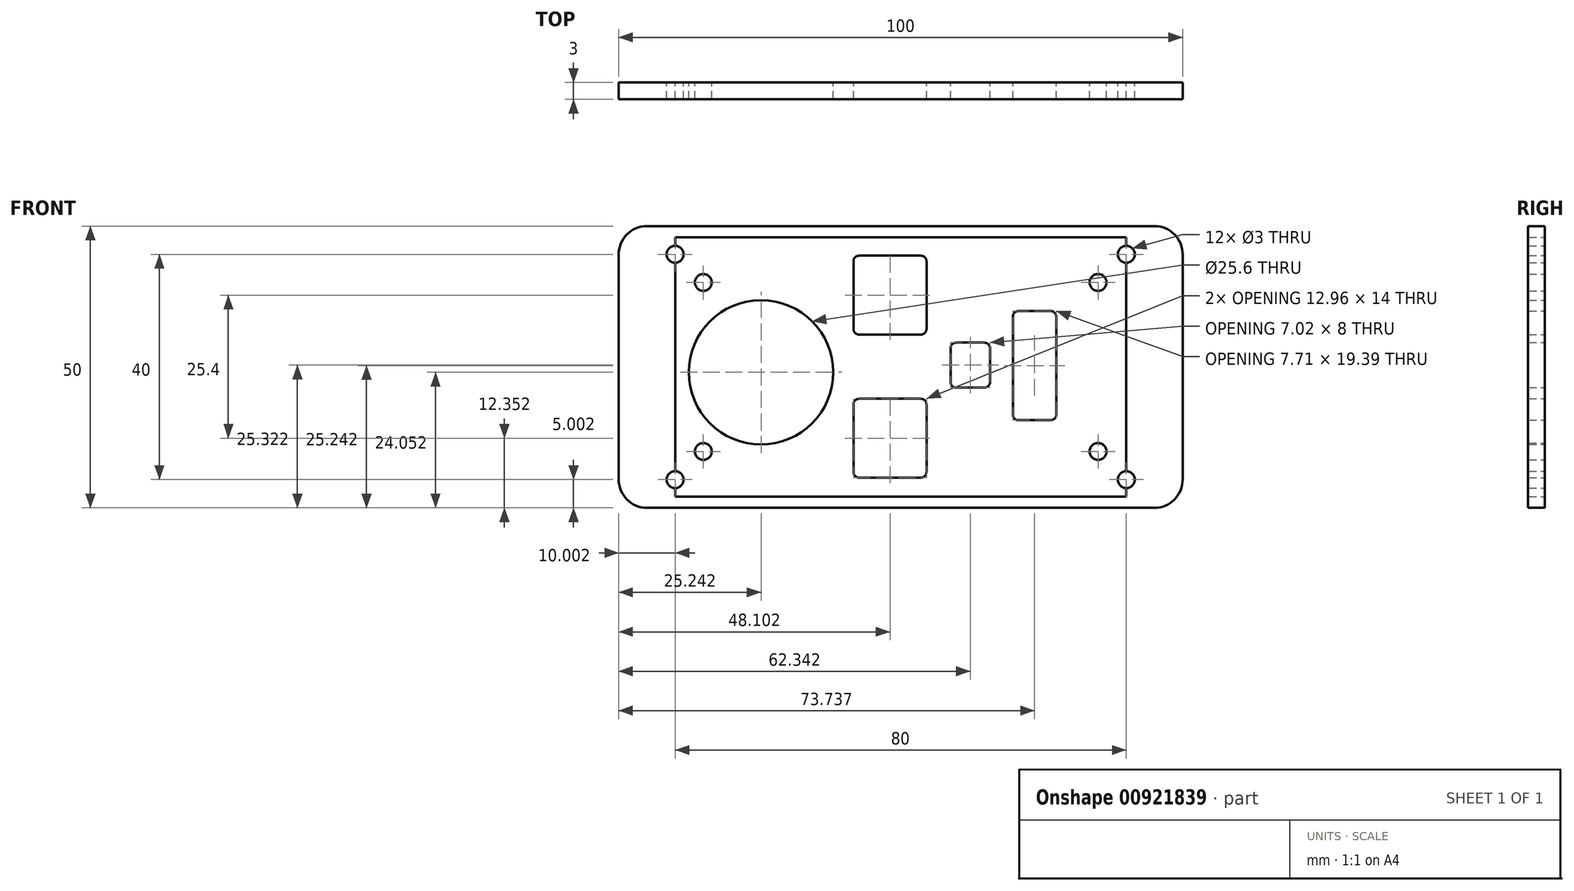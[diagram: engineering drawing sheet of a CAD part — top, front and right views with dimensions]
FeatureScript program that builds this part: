
annotation { "Feature Type Name" : "Feature", "Feature Type Description" : "" }
export const myFeature = defineFeature(function(context is Context, id is Id, definition is map)
    precondition{}
    {
        {
            var Q0;
            Q0=qCreatedBy(makeId("Front.planeOp"),FACE);
            var sketch = newSketch(context, id + "F0", { "sketchPlane" : qUnion([Q0])});
            skLineSegment(sketch, "E0", {"start": v(-79.7, -49.9) * mm, "end": v(-79.7, -9.9) * mm});
            skArc(sketch, "E1", {"start": v(-79.7, -9.9) * mm, "mid": v(-79.9, -9.7) * mm, "end": v(-80.1, -9.9) * mm});
            skLineSegment(sketch, "E2", {"start": v(-80.1, -9.9) * mm, "end": v(-80.1, -49.9) * mm});
            skArc(sketch, "E3", {"start": v(-80.1, -49.9) * mm, "mid": v(-79.9, -50.1) * mm, "end": v(-79.7, -49.9) * mm});
            skLineSegment(sketch, "E4", {"start": v(-79.9, -10.1) * mm, "end": v(0.1, -10.1) * mm});
            skArc(sketch, "E5", {"start": v(0.1, -10.1) * mm, "mid": v(0.3, -9.9) * mm, "end": v(0.1, -9.7) * mm});
            skLineSegment(sketch, "E6", {"start": v(0.1, -9.7) * mm, "end": v(-79.9, -9.7) * mm});
            skArc(sketch, "E7", {"start": v(-79.9, -9.7) * mm, "mid": v(-80.1, -9.9) * mm, "end": v(-79.9, -10.1) * mm});
            skLineSegment(sketch, "E8", {"start": v(-0.1, -9.9) * mm, "end": v(-0.1, -49.9) * mm});
            skArc(sketch, "E9", {"start": v(-0.1, -49.9) * mm, "mid": v(0.1, -50.1) * mm, "end": v(0.3, -49.9) * mm});
            skLineSegment(sketch, "E10", {"start": v(0.3, -49.9) * mm, "end": v(0.3, -9.9) * mm});
            skArc(sketch, "E11", {"start": v(0.3, -9.9) * mm, "mid": v(0.1, -9.7) * mm, "end": v(-0.1, -9.9) * mm});
            skLineSegment(sketch, "E12", {"start": v(0.1, -49.7) * mm, "end": v(-79.9, -49.7) * mm});
            skArc(sketch, "E13", {"start": v(-79.9, -49.7) * mm, "mid": v(-80.1, -49.9) * mm, "end": v(-79.9, -50.1) * mm});
            skLineSegment(sketch, "E14", {"start": v(-79.9, -50.1) * mm, "end": v(0.1, -50.1) * mm});
            skArc(sketch, "E15", {"start": v(0.1, -50.1) * mm, "mid": v(0.3, -49.9) * mm, "end": v(0.1, -49.7) * mm});
            skLineSegment(sketch, "E16", {"start": v(-11.34, -30.22) * mm, "end": v(-11.46, -30.1) * mm});
            skArc(sketch, "E17", {"start": v(-11.46, -30.1) * mm, "mid": v(-11.52, -30.1) * mm, "end": v(-11.52, -30.15) * mm});
            skLineSegment(sketch, "E18", {"start": v(-11.52, -30.15) * mm, "end": v(-11.4, -30.27) * mm});
            skArc(sketch, "E19", {"start": v(-11.4, -30.27) * mm, "mid": v(-11.34, -30.27) * mm, "end": v(-11.34, -30.22) * mm});
            skLineSegment(sketch, "E20", {"start": v(-11.5, -30.09) * mm, "end": v(-11.74, -30.09) * mm});
            skArc(sketch, "E21", {"start": v(-11.74, -30.09) * mm, "mid": v(-11.78, -30.12) * mm, "end": v(-11.74, -30.16) * mm});
            skLineSegment(sketch, "E22", {"start": v(-11.74, -30.16) * mm, "end": v(-11.5, -30.16) * mm});
            skArc(sketch, "E23", {"start": v(-11.5, -30.16) * mm, "mid": v(-11.45, -30.12) * mm, "end": v(-11.5, -30.09) * mm});
            skLineSegment(sketch, "E24", {"start": v(-11.76, -30.1) * mm, "end": v(-11.89, -30.22) * mm});
            skArc(sketch, "E25", {"start": v(-11.89, -30.22) * mm, "mid": v(-11.89, -30.27) * mm, "end": v(-11.83, -30.27) * mm});
            skLineSegment(sketch, "E26", {"start": v(-11.83, -30.27) * mm, "end": v(-11.71, -30.15) * mm});
            skArc(sketch, "E27", {"start": v(-11.71, -30.15) * mm, "mid": v(-11.71, -30.1) * mm, "end": v(-11.76, -30.1) * mm});
            skLineSegment(sketch, "E28", {"start": v(-11.9, -30.25) * mm, "end": v(-11.9, -30.74) * mm});
            skArc(sketch, "E29", {"start": v(-11.9, -30.74) * mm, "mid": v(-11.86, -30.78) * mm, "end": v(-11.82, -30.74) * mm});
            skLineSegment(sketch, "E30", {"start": v(-11.82, -30.74) * mm, "end": v(-11.82, -30.25) * mm});
            skArc(sketch, "E31", {"start": v(-11.82, -30.25) * mm, "mid": v(-11.86, -30.2) * mm, "end": v(-11.9, -30.25) * mm});
            skLineSegment(sketch, "E32", {"start": v(-11.89, -30.76) * mm, "end": v(-11.76, -30.89) * mm});
            skArc(sketch, "E33", {"start": v(-11.76, -30.89) * mm, "mid": v(-11.71, -30.89) * mm, "end": v(-11.71, -30.83) * mm});
            skLineSegment(sketch, "E34", {"start": v(-11.71, -30.83) * mm, "end": v(-11.83, -30.71) * mm});
            skArc(sketch, "E35", {"start": v(-11.83, -30.71) * mm, "mid": v(-11.89, -30.71) * mm, "end": v(-11.89, -30.76) * mm});
            skLineSegment(sketch, "E36", {"start": v(-11.74, -30.9) * mm, "end": v(-11.5, -30.9) * mm});
            skArc(sketch, "E37", {"start": v(-11.5, -30.9) * mm, "mid": v(-11.45, -30.86) * mm, "end": v(-11.5, -30.82) * mm});
            skLineSegment(sketch, "E38", {"start": v(-11.5, -30.82) * mm, "end": v(-11.74, -30.82) * mm});
            skArc(sketch, "E39", {"start": v(-11.74, -30.82) * mm, "mid": v(-11.78, -30.86) * mm, "end": v(-11.74, -30.9) * mm});
            skLineSegment(sketch, "E40", {"start": v(-11.46, -30.89) * mm, "end": v(-11.34, -30.76) * mm});
            skArc(sketch, "E41", {"start": v(-11.34, -30.76) * mm, "mid": v(-11.34, -30.71) * mm, "end": v(-11.4, -30.71) * mm});
            skLineSegment(sketch, "E42", {"start": v(-11.4, -30.71) * mm, "end": v(-11.52, -30.83) * mm});
            skArc(sketch, "E43", {"start": v(-11.52, -30.83) * mm, "mid": v(-11.52, -30.89) * mm, "end": v(-11.46, -30.89) * mm});
            skLineSegment(sketch, "E44", {"start": v(-11.33, -30.74) * mm, "end": v(-11.33, -30.5) * mm});
            skArc(sketch, "E45", {"start": v(-11.33, -30.5) * mm, "mid": v(-11.37, -30.45) * mm, "end": v(-11.4, -30.5) * mm});
            skLineSegment(sketch, "E46", {"start": v(-11.4, -30.5) * mm, "end": v(-11.4, -30.74) * mm});
            skArc(sketch, "E47", {"start": v(-11.4, -30.74) * mm, "mid": v(-11.37, -30.78) * mm, "end": v(-11.33, -30.74) * mm});
            skLineSegment(sketch, "E48", {"start": v(-11.37, -30.45) * mm, "end": v(-11.61, -30.45) * mm});
            skArc(sketch, "E49", {"start": v(-11.61, -30.45) * mm, "mid": v(-11.65, -30.5) * mm, "end": v(-11.61, -30.53) * mm});
            skLineSegment(sketch, "E50", {"start": v(-11.61, -30.53) * mm, "end": v(-11.37, -30.53) * mm});
            skArc(sketch, "E51", {"start": v(-11.37, -30.53) * mm, "mid": v(-11.33, -30.5) * mm, "end": v(-11.37, -30.45) * mm});
            skLineSegment(sketch, "E52", {"start": v(-11.07, -30.86) * mm, "end": v(-11.07, -30.12) * mm});
            skArc(sketch, "E53", {"start": v(-11.07, -30.12) * mm, "mid": v(-11.11, -30.09) * mm, "end": v(-11.15, -30.12) * mm});
            skLineSegment(sketch, "E54", {"start": v(-11.15, -30.12) * mm, "end": v(-11.15, -30.86) * mm});
            skArc(sketch, "E55", {"start": v(-11.15, -30.86) * mm, "mid": v(-11.11, -30.9) * mm, "end": v(-11.07, -30.86) * mm});
            skLineSegment(sketch, "E56", {"start": v(-11.14, -30.14) * mm, "end": v(-10.65, -30.88) * mm});
            skArc(sketch, "E57", {"start": v(-10.65, -30.88) * mm, "mid": v(-10.6, -30.9) * mm, "end": v(-10.59, -30.84) * mm});
            skLineSegment(sketch, "E58", {"start": v(-10.59, -30.84) * mm, "end": v(-11.08, -30.1) * mm});
            skArc(sketch, "E59", {"start": v(-11.08, -30.1) * mm, "mid": v(-11.13, -30.1) * mm, "end": v(-11.14, -30.14) * mm});
            skLineSegment(sketch, "E60", {"start": v(-10.58, -30.86) * mm, "end": v(-10.58, -30.12) * mm});
            skArc(sketch, "E61", {"start": v(-10.58, -30.12) * mm, "mid": v(-10.62, -30.09) * mm, "end": v(-10.66, -30.12) * mm});
            skLineSegment(sketch, "E62", {"start": v(-10.66, -30.12) * mm, "end": v(-10.66, -30.86) * mm});
            skArc(sketch, "E63", {"start": v(-10.66, -30.86) * mm, "mid": v(-10.62, -30.9) * mm, "end": v(-10.58, -30.86) * mm});
            skLineSegment(sketch, "E64", {"start": v(-10.4, -30.12) * mm, "end": v(-10.4, -30.86) * mm});
            skArc(sketch, "E65", {"start": v(-10.4, -30.86) * mm, "mid": v(-10.36, -30.9) * mm, "end": v(-10.33, -30.86) * mm});
            skLineSegment(sketch, "E66", {"start": v(-10.33, -30.86) * mm, "end": v(-10.33, -30.12) * mm});
            skArc(sketch, "E67", {"start": v(-10.33, -30.12) * mm, "mid": v(-10.36, -30.09) * mm, "end": v(-10.4, -30.12) * mm});
            skLineSegment(sketch, "E68", {"start": v(-10.36, -30.9) * mm, "end": v(-10, -30.9) * mm});
            skArc(sketch, "E69", {"start": v(-10, -30.9) * mm, "mid": v(-9.96, -30.86) * mm, "end": v(-10, -30.82) * mm});
            skLineSegment(sketch, "E70", {"start": v(-10, -30.82) * mm, "end": v(-10.36, -30.82) * mm});
            skArc(sketch, "E71", {"start": v(-10.36, -30.82) * mm, "mid": v(-10.4, -30.86) * mm, "end": v(-10.36, -30.9) * mm});
            skLineSegment(sketch, "E72", {"start": v(-9.97, -30.89) * mm, "end": v(-9.84, -30.76) * mm});
            skArc(sketch, "E73", {"start": v(-9.85, -30.76) * mm, "mid": v(-9.85, -30.71) * mm, "end": v(-9.9, -30.71) * mm});
            skLineSegment(sketch, "E74", {"start": v(-9.9, -30.71) * mm, "end": v(-10.02, -30.83) * mm});
            skArc(sketch, "E75", {"start": v(-10.02, -30.83) * mm, "mid": v(-10.02, -30.89) * mm, "end": v(-9.97, -30.89) * mm});
            skLineSegment(sketch, "E76", {"start": v(-9.83, -30.74) * mm, "end": v(-9.83, -30.25) * mm});
            skArc(sketch, "E77", {"start": v(-9.83, -30.25) * mm, "mid": v(-9.87, -30.2) * mm, "end": v(-9.91, -30.25) * mm});
            skLineSegment(sketch, "E78", {"start": v(-9.91, -30.25) * mm, "end": v(-9.91, -30.74) * mm});
            skArc(sketch, "E79", {"start": v(-9.91, -30.74) * mm, "mid": v(-9.87, -30.78) * mm, "end": v(-9.83, -30.74) * mm});
            skLineSegment(sketch, "E80", {"start": v(-9.84, -30.22) * mm, "end": v(-9.97, -30.1) * mm});
            skArc(sketch, "E81", {"start": v(-9.97, -30.1) * mm, "mid": v(-10.02, -30.1) * mm, "end": v(-10.02, -30.15) * mm});
            skLineSegment(sketch, "E82", {"start": v(-10.02, -30.15) * mm, "end": v(-9.9, -30.27) * mm});
            skArc(sketch, "E83", {"start": v(-9.9, -30.27) * mm, "mid": v(-9.85, -30.27) * mm, "end": v(-9.85, -30.22) * mm});
            skLineSegment(sketch, "E84", {"start": v(-10, -30.09) * mm, "end": v(-10.36, -30.09) * mm});
            skArc(sketch, "E85", {"start": v(-10.36, -30.09) * mm, "mid": v(-10.4, -30.12) * mm, "end": v(-10.36, -30.16) * mm});
            skLineSegment(sketch, "E86", {"start": v(-10.36, -30.16) * mm, "end": v(-10, -30.16) * mm});
            skArc(sketch, "E87", {"start": v(-10, -30.16) * mm, "mid": v(-9.96, -30.12) * mm, "end": v(-10, -30.09) * mm});
            skLineSegment(sketch, "E88", {"start": v(-11.9, -22.12) * mm, "end": v(-11.9, -22.61) * mm});
            skArc(sketch, "E89", {"start": v(-11.9, -22.61) * mm, "mid": v(-11.86, -22.65) * mm, "end": v(-11.82, -22.61) * mm});
            skLineSegment(sketch, "E90", {"start": v(-11.82, -22.61) * mm, "end": v(-11.82, -22.12) * mm});
            skArc(sketch, "E91", {"start": v(-11.82, -22.12) * mm, "mid": v(-11.86, -22.09) * mm, "end": v(-11.9, -22.12) * mm});
            skLineSegment(sketch, "E92", {"start": v(-11.89, -22.64) * mm, "end": v(-11.64, -22.89) * mm});
            skArc(sketch, "E93", {"start": v(-11.64, -22.89) * mm, "mid": v(-11.59, -22.89) * mm, "end": v(-11.59, -22.83) * mm});
            skLineSegment(sketch, "E94", {"start": v(-11.59, -22.83) * mm, "end": v(-11.83, -22.59) * mm});
            skArc(sketch, "E95", {"start": v(-11.83, -22.59) * mm, "mid": v(-11.89, -22.59) * mm, "end": v(-11.89, -22.64) * mm});
            skLineSegment(sketch, "E96", {"start": v(-11.59, -22.89) * mm, "end": v(-11.34, -22.64) * mm});
            skArc(sketch, "E97", {"start": v(-11.34, -22.64) * mm, "mid": v(-11.34, -22.59) * mm, "end": v(-11.4, -22.59) * mm});
            skLineSegment(sketch, "E98", {"start": v(-11.4, -22.59) * mm, "end": v(-11.64, -22.83) * mm});
            skArc(sketch, "E99", {"start": v(-11.64, -22.83) * mm, "mid": v(-11.64, -22.89) * mm, "end": v(-11.59, -22.89) * mm});
            skLineSegment(sketch, "E100", {"start": v(-11.33, -22.61) * mm, "end": v(-11.33, -22.12) * mm});
            skArc(sketch, "E101", {"start": v(-11.33, -22.12) * mm, "mid": v(-11.37, -22.09) * mm, "end": v(-11.4, -22.12) * mm});
            skLineSegment(sketch, "E102", {"start": v(-11.4, -22.12) * mm, "end": v(-11.4, -22.61) * mm});
            skArc(sketch, "E103", {"start": v(-11.4, -22.61) * mm, "mid": v(-11.37, -22.65) * mm, "end": v(-11.33, -22.61) * mm});
            skLineSegment(sketch, "E104", {"start": v(-10.6, -22.22) * mm, "end": v(-10.72, -22.1) * mm});
            skArc(sketch, "E105", {"start": v(-10.72, -22.1) * mm, "mid": v(-10.77, -22.1) * mm, "end": v(-10.77, -22.15) * mm});
            skLineSegment(sketch, "E106", {"start": v(-10.77, -22.15) * mm, "end": v(-10.65, -22.27) * mm});
            skArc(sketch, "E107", {"start": v(-10.65, -22.27) * mm, "mid": v(-10.6, -22.27) * mm, "end": v(-10.6, -22.22) * mm});
            skLineSegment(sketch, "E108", {"start": v(-10.74, -22.09) * mm, "end": v(-10.99, -22.09) * mm});
            skArc(sketch, "E109", {"start": v(-10.99, -22.09) * mm, "mid": v(-11.03, -22.12) * mm, "end": v(-10.99, -22.16) * mm});
            skLineSegment(sketch, "E110", {"start": v(-10.99, -22.16) * mm, "end": v(-10.74, -22.16) * mm});
            skArc(sketch, "E111", {"start": v(-10.74, -22.16) * mm, "mid": v(-10.7, -22.12) * mm, "end": v(-10.74, -22.09) * mm});
            skLineSegment(sketch, "E112", {"start": v(-11.02, -22.1) * mm, "end": v(-11.14, -22.22) * mm});
            skArc(sketch, "E113", {"start": v(-11.14, -22.22) * mm, "mid": v(-11.14, -22.27) * mm, "end": v(-11.08, -22.27) * mm});
            skLineSegment(sketch, "E114", {"start": v(-11.08, -22.27) * mm, "end": v(-10.96, -22.15) * mm});
            skArc(sketch, "E115", {"start": v(-10.96, -22.15) * mm, "mid": v(-10.96, -22.1) * mm, "end": v(-11.02, -22.1) * mm});
            skLineSegment(sketch, "E116", {"start": v(-11.15, -22.25) * mm, "end": v(-11.15, -22.74) * mm});
            skArc(sketch, "E117", {"start": v(-11.15, -22.74) * mm, "mid": v(-11.11, -22.78) * mm, "end": v(-11.07, -22.74) * mm});
            skLineSegment(sketch, "E118", {"start": v(-11.07, -22.74) * mm, "end": v(-11.07, -22.25) * mm});
            skArc(sketch, "E119", {"start": v(-11.07, -22.25) * mm, "mid": v(-11.11, -22.2) * mm, "end": v(-11.15, -22.25) * mm});
            skLineSegment(sketch, "E120", {"start": v(-11.14, -22.76) * mm, "end": v(-11.02, -22.89) * mm});
            skArc(sketch, "E121", {"start": v(-11.02, -22.89) * mm, "mid": v(-10.96, -22.89) * mm, "end": v(-10.96, -22.83) * mm});
            skLineSegment(sketch, "E122", {"start": v(-10.96, -22.83) * mm, "end": v(-11.08, -22.71) * mm});
            skArc(sketch, "E123", {"start": v(-11.08, -22.71) * mm, "mid": v(-11.14, -22.71) * mm, "end": v(-11.14, -22.76) * mm});
            skLineSegment(sketch, "E124", {"start": v(-10.99, -22.9) * mm, "end": v(-10.74, -22.9) * mm});
            skArc(sketch, "E125", {"start": v(-10.74, -22.9) * mm, "mid": v(-10.7, -22.86) * mm, "end": v(-10.74, -22.82) * mm});
            skLineSegment(sketch, "E126", {"start": v(-10.74, -22.82) * mm, "end": v(-10.99, -22.82) * mm});
            skArc(sketch, "E127", {"start": v(-10.99, -22.82) * mm, "mid": v(-11.03, -22.86) * mm, "end": v(-10.99, -22.9) * mm});
            skLineSegment(sketch, "E128", {"start": v(-10.72, -22.89) * mm, "end": v(-10.6, -22.76) * mm});
            skArc(sketch, "E129", {"start": v(-10.6, -22.76) * mm, "mid": v(-10.6, -22.71) * mm, "end": v(-10.65, -22.71) * mm});
            skLineSegment(sketch, "E130", {"start": v(-10.65, -22.71) * mm, "end": v(-10.77, -22.83) * mm});
            skArc(sketch, "E131", {"start": v(-10.77, -22.83) * mm, "mid": v(-10.77, -22.89) * mm, "end": v(-10.72, -22.89) * mm});
            skLineSegment(sketch, "E132", {"start": v(-9.84, -22.22) * mm, "end": v(-9.97, -22.1) * mm});
            skArc(sketch, "E133", {"start": v(-9.97, -22.1) * mm, "mid": v(-10.02, -22.1) * mm, "end": v(-10.02, -22.15) * mm});
            skLineSegment(sketch, "E134", {"start": v(-10.02, -22.15) * mm, "end": v(-9.9, -22.27) * mm});
            skArc(sketch, "E135", {"start": v(-9.9, -22.27) * mm, "mid": v(-9.85, -22.27) * mm, "end": v(-9.85, -22.22) * mm});
            skLineSegment(sketch, "E136", {"start": v(-10, -22.09) * mm, "end": v(-10.24, -22.09) * mm});
            skArc(sketch, "E137", {"start": v(-10.24, -22.09) * mm, "mid": v(-10.28, -22.12) * mm, "end": v(-10.24, -22.16) * mm});
            skLineSegment(sketch, "E138", {"start": v(-10.24, -22.16) * mm, "end": v(-10, -22.16) * mm});
            skArc(sketch, "E139", {"start": v(-10, -22.16) * mm, "mid": v(-9.96, -22.12) * mm, "end": v(-10, -22.09) * mm});
            skLineSegment(sketch, "E140", {"start": v(-10.27, -22.1) * mm, "end": v(-10.4, -22.22) * mm});
            skArc(sketch, "E141", {"start": v(-10.4, -22.22) * mm, "mid": v(-10.4, -22.27) * mm, "end": v(-10.34, -22.27) * mm});
            skLineSegment(sketch, "E142", {"start": v(-10.34, -22.27) * mm, "end": v(-10.21, -22.15) * mm});
            skArc(sketch, "E143", {"start": v(-10.21, -22.15) * mm, "mid": v(-10.21, -22.1) * mm, "end": v(-10.27, -22.1) * mm});
            skLineSegment(sketch, "E144", {"start": v(-10.4, -22.25) * mm, "end": v(-10.4, -22.74) * mm});
            skArc(sketch, "E145", {"start": v(-10.4, -22.74) * mm, "mid": v(-10.36, -22.78) * mm, "end": v(-10.33, -22.74) * mm});
            skLineSegment(sketch, "E146", {"start": v(-10.33, -22.74) * mm, "end": v(-10.33, -22.25) * mm});
            skArc(sketch, "E147", {"start": v(-10.33, -22.25) * mm, "mid": v(-10.36, -22.2) * mm, "end": v(-10.4, -22.25) * mm});
            skLineSegment(sketch, "E148", {"start": v(-10.4, -22.76) * mm, "end": v(-10.27, -22.89) * mm});
            skArc(sketch, "E149", {"start": v(-10.27, -22.89) * mm, "mid": v(-10.21, -22.89) * mm, "end": v(-10.21, -22.83) * mm});
            skLineSegment(sketch, "E150", {"start": v(-10.21, -22.83) * mm, "end": v(-10.34, -22.71) * mm});
            skArc(sketch, "E151", {"start": v(-10.34, -22.71) * mm, "mid": v(-10.4, -22.71) * mm, "end": v(-10.4, -22.76) * mm});
            skLineSegment(sketch, "E152", {"start": v(-10.24, -22.9) * mm, "end": v(-10, -22.9) * mm});
            skArc(sketch, "E153", {"start": v(-10, -22.9) * mm, "mid": v(-9.96, -22.86) * mm, "end": v(-10, -22.82) * mm});
            skLineSegment(sketch, "E154", {"start": v(-10, -22.82) * mm, "end": v(-10.24, -22.82) * mm});
            skArc(sketch, "E155", {"start": v(-10.24, -22.82) * mm, "mid": v(-10.28, -22.86) * mm, "end": v(-10.24, -22.9) * mm});
            skLineSegment(sketch, "E156", {"start": v(-9.97, -22.89) * mm, "end": v(-9.84, -22.76) * mm});
            skArc(sketch, "E157", {"start": v(-9.85, -22.76) * mm, "mid": v(-9.85, -22.71) * mm, "end": v(-9.9, -22.71) * mm});
            skLineSegment(sketch, "E158", {"start": v(-9.9, -22.71) * mm, "end": v(-10.02, -22.83) * mm});
            skArc(sketch, "E159", {"start": v(-10.02, -22.83) * mm, "mid": v(-10.02, -22.89) * mm, "end": v(-9.97, -22.89) * mm});
            skLineSegment(sketch, "E160", {"start": v(-11.9, -25.12) * mm, "end": v(-11.9, -25.61) * mm});
            skArc(sketch, "E161", {"start": v(-11.9, -25.61) * mm, "mid": v(-11.86, -25.65) * mm, "end": v(-11.82, -25.61) * mm});
            skLineSegment(sketch, "E162", {"start": v(-11.82, -25.61) * mm, "end": v(-11.82, -25.12) * mm});
            skArc(sketch, "E163", {"start": v(-11.82, -25.12) * mm, "mid": v(-11.86, -25.09) * mm, "end": v(-11.9, -25.12) * mm});
            skLineSegment(sketch, "E164", {"start": v(-11.89, -25.64) * mm, "end": v(-11.64, -25.89) * mm});
            skArc(sketch, "E165", {"start": v(-11.64, -25.89) * mm, "mid": v(-11.59, -25.89) * mm, "end": v(-11.59, -25.83) * mm});
            skLineSegment(sketch, "E166", {"start": v(-11.59, -25.83) * mm, "end": v(-11.83, -25.59) * mm});
            skArc(sketch, "E167", {"start": v(-11.83, -25.59) * mm, "mid": v(-11.89, -25.59) * mm, "end": v(-11.89, -25.64) * mm});
            skLineSegment(sketch, "E168", {"start": v(-11.59, -25.89) * mm, "end": v(-11.34, -25.64) * mm});
            skArc(sketch, "E169", {"start": v(-11.34, -25.64) * mm, "mid": v(-11.34, -25.59) * mm, "end": v(-11.4, -25.59) * mm});
            skLineSegment(sketch, "E170", {"start": v(-11.4, -25.59) * mm, "end": v(-11.64, -25.83) * mm});
            skArc(sketch, "E171", {"start": v(-11.64, -25.83) * mm, "mid": v(-11.64, -25.89) * mm, "end": v(-11.59, -25.89) * mm});
            skLineSegment(sketch, "E172", {"start": v(-11.33, -25.61) * mm, "end": v(-11.33, -25.12) * mm});
            skArc(sketch, "E173", {"start": v(-11.33, -25.12) * mm, "mid": v(-11.37, -25.09) * mm, "end": v(-11.4, -25.12) * mm});
            skLineSegment(sketch, "E174", {"start": v(-11.4, -25.12) * mm, "end": v(-11.4, -25.61) * mm});
            skArc(sketch, "E175", {"start": v(-11.4, -25.61) * mm, "mid": v(-11.37, -25.65) * mm, "end": v(-11.33, -25.61) * mm});
            skLineSegment(sketch, "E176", {"start": v(-10.62, -25.09) * mm, "end": v(-11.11, -25.09) * mm});
            skArc(sketch, "E177", {"start": v(-11.11, -25.09) * mm, "mid": v(-11.15, -25.12) * mm, "end": v(-11.11, -25.16) * mm});
            skLineSegment(sketch, "E178", {"start": v(-11.11, -25.16) * mm, "end": v(-10.62, -25.16) * mm});
            skArc(sketch, "E179", {"start": v(-10.62, -25.16) * mm, "mid": v(-10.58, -25.12) * mm, "end": v(-10.62, -25.09) * mm});
            skLineSegment(sketch, "E180", {"start": v(-11.15, -25.12) * mm, "end": v(-11.15, -25.86) * mm});
            skArc(sketch, "E181", {"start": v(-11.15, -25.86) * mm, "mid": v(-11.11, -25.9) * mm, "end": v(-11.07, -25.86) * mm});
            skLineSegment(sketch, "E182", {"start": v(-11.07, -25.86) * mm, "end": v(-11.07, -25.12) * mm});
            skArc(sketch, "E183", {"start": v(-11.07, -25.12) * mm, "mid": v(-11.11, -25.09) * mm, "end": v(-11.15, -25.12) * mm});
            skLineSegment(sketch, "E184", {"start": v(-11.11, -25.9) * mm, "end": v(-10.62, -25.9) * mm});
            skArc(sketch, "E185", {"start": v(-10.62, -25.9) * mm, "mid": v(-10.58, -25.86) * mm, "end": v(-10.62, -25.82) * mm});
            skLineSegment(sketch, "E186", {"start": v(-10.62, -25.82) * mm, "end": v(-11.11, -25.82) * mm});
            skArc(sketch, "E187", {"start": v(-11.11, -25.82) * mm, "mid": v(-11.15, -25.86) * mm, "end": v(-11.11, -25.9) * mm});
            skLineSegment(sketch, "E188", {"start": v(-11.11, -25.53) * mm, "end": v(-10.87, -25.53) * mm});
            skArc(sketch, "E189", {"start": v(-10.87, -25.53) * mm, "mid": v(-10.83, -25.5) * mm, "end": v(-10.87, -25.45) * mm});
            skLineSegment(sketch, "E190", {"start": v(-10.87, -25.45) * mm, "end": v(-11.11, -25.45) * mm});
            skArc(sketch, "E191", {"start": v(-11.11, -25.45) * mm, "mid": v(-11.15, -25.5) * mm, "end": v(-11.11, -25.53) * mm});
            skLineSegment(sketch, "E192", {"start": v(-10.33, -25.86) * mm, "end": v(-10.33, -25.12) * mm});
            skArc(sketch, "E193", {"start": v(-10.33, -25.12) * mm, "mid": v(-10.36, -25.09) * mm, "end": v(-10.4, -25.12) * mm});
            skLineSegment(sketch, "E194", {"start": v(-10.4, -25.12) * mm, "end": v(-10.4, -25.86) * mm});
            skArc(sketch, "E195", {"start": v(-10.4, -25.86) * mm, "mid": v(-10.36, -25.9) * mm, "end": v(-10.33, -25.86) * mm});
            skLineSegment(sketch, "E196", {"start": v(-10.36, -25.16) * mm, "end": v(-10, -25.16) * mm});
            skArc(sketch, "E197", {"start": v(-10, -25.16) * mm, "mid": v(-9.96, -25.12) * mm, "end": v(-10, -25.09) * mm});
            skLineSegment(sketch, "E198", {"start": v(-10, -25.09) * mm, "end": v(-10.36, -25.09) * mm});
            skArc(sketch, "E199", {"start": v(-10.36, -25.09) * mm, "mid": v(-10.4, -25.12) * mm, "end": v(-10.36, -25.16) * mm});
            skLineSegment(sketch, "E200", {"start": v(-10.02, -25.15) * mm, "end": v(-9.9, -25.27) * mm});
            skArc(sketch, "E201", {"start": v(-9.9, -25.27) * mm, "mid": v(-9.85, -25.27) * mm, "end": v(-9.85, -25.22) * mm});
            skLineSegment(sketch, "E202", {"start": v(-9.84, -25.22) * mm, "end": v(-9.97, -25.1) * mm});
            skArc(sketch, "E203", {"start": v(-9.97, -25.1) * mm, "mid": v(-10.02, -25.1) * mm, "end": v(-10.02, -25.15) * mm});
            skLineSegment(sketch, "E204", {"start": v(-9.91, -25.25) * mm, "end": v(-9.91, -25.5) * mm});
            skArc(sketch, "E205", {"start": v(-9.91, -25.5) * mm, "mid": v(-9.87, -25.53) * mm, "end": v(-9.83, -25.5) * mm});
            skLineSegment(sketch, "E206", {"start": v(-9.83, -25.5) * mm, "end": v(-9.83, -25.25) * mm});
            skArc(sketch, "E207", {"start": v(-9.83, -25.25) * mm, "mid": v(-9.87, -25.2) * mm, "end": v(-9.91, -25.25) * mm});
            skLineSegment(sketch, "E208", {"start": v(-9.9, -25.46) * mm, "end": v(-10.02, -25.59) * mm});
            skArc(sketch, "E209", {"start": v(-10.02, -25.59) * mm, "mid": v(-10.02, -25.64) * mm, "end": v(-9.97, -25.64) * mm});
            skLineSegment(sketch, "E210", {"start": v(-9.97, -25.64) * mm, "end": v(-9.84, -25.52) * mm});
            skArc(sketch, "E211", {"start": v(-9.85, -25.52) * mm, "mid": v(-9.85, -25.46) * mm, "end": v(-9.9, -25.46) * mm});
            skLineSegment(sketch, "E212", {"start": v(-10, -25.58) * mm, "end": v(-10.36, -25.58) * mm});
            skArc(sketch, "E213", {"start": v(-10.36, -25.58) * mm, "mid": v(-10.4, -25.61) * mm, "end": v(-10.36, -25.65) * mm});
            skLineSegment(sketch, "E214", {"start": v(-10.36, -25.65) * mm, "end": v(-10, -25.65) * mm});
            skArc(sketch, "E215", {"start": v(-10, -25.65) * mm, "mid": v(-9.96, -25.61) * mm, "end": v(-10, -25.58) * mm});
            skLineSegment(sketch, "E216", {"start": v(-10.14, -25.64) * mm, "end": v(-9.9, -25.89) * mm});
            skArc(sketch, "E217", {"start": v(-9.9, -25.89) * mm, "mid": v(-9.85, -25.89) * mm, "end": v(-9.84, -25.83) * mm});
            skLineSegment(sketch, "E218", {"start": v(-9.84, -25.83) * mm, "end": v(-10.1, -25.59) * mm});
            skArc(sketch, "E219", {"start": v(-10.1, -25.59) * mm, "mid": v(-10.14, -25.59) * mm, "end": v(-10.14, -25.64) * mm});
            skLineSegment(sketch, "E220", {"start": v(-11.82, -28.86) * mm, "end": v(-11.82, -28.12) * mm});
            skArc(sketch, "E221", {"start": v(-11.82, -28.12) * mm, "mid": v(-11.86, -28.09) * mm, "end": v(-11.9, -28.12) * mm});
            skLineSegment(sketch, "E222", {"start": v(-11.9, -28.12) * mm, "end": v(-11.9, -28.86) * mm});
            skArc(sketch, "E223", {"start": v(-11.9, -28.86) * mm, "mid": v(-11.86, -28.9) * mm, "end": v(-11.82, -28.86) * mm});
            skLineSegment(sketch, "E224", {"start": v(-11.86, -28.53) * mm, "end": v(-11.37, -28.53) * mm});
            skArc(sketch, "E225", {"start": v(-11.37, -28.53) * mm, "mid": v(-11.33, -28.5) * mm, "end": v(-11.37, -28.45) * mm});
            skLineSegment(sketch, "E226", {"start": v(-11.37, -28.45) * mm, "end": v(-11.86, -28.45) * mm});
            skArc(sketch, "E227", {"start": v(-11.86, -28.45) * mm, "mid": v(-11.9, -28.5) * mm, "end": v(-11.86, -28.53) * mm});
            skLineSegment(sketch, "E228", {"start": v(-11.4, -28.12) * mm, "end": v(-11.4, -28.86) * mm});
            skArc(sketch, "E229", {"start": v(-11.4, -28.86) * mm, "mid": v(-11.37, -28.9) * mm, "end": v(-11.33, -28.86) * mm});
            skLineSegment(sketch, "E230", {"start": v(-11.33, -28.86) * mm, "end": v(-11.33, -28.12) * mm});
            skArc(sketch, "E231", {"start": v(-11.33, -28.12) * mm, "mid": v(-11.37, -28.09) * mm, "end": v(-11.4, -28.12) * mm});
            skLineSegment(sketch, "E232", {"start": v(-10.74, -28.09) * mm, "end": v(-10.99, -28.09) * mm});
            skArc(sketch, "E233", {"start": v(-10.99, -28.09) * mm, "mid": v(-11.03, -28.12) * mm, "end": v(-10.99, -28.16) * mm});
            skLineSegment(sketch, "E234", {"start": v(-10.99, -28.16) * mm, "end": v(-10.74, -28.16) * mm});
            skArc(sketch, "E235", {"start": v(-10.74, -28.16) * mm, "mid": v(-10.7, -28.12) * mm, "end": v(-10.74, -28.09) * mm});
            skLineSegment(sketch, "E236", {"start": v(-11.02, -28.1) * mm, "end": v(-11.14, -28.22) * mm});
            skArc(sketch, "E237", {"start": v(-11.14, -28.22) * mm, "mid": v(-11.14, -28.27) * mm, "end": v(-11.08, -28.27) * mm});
            skLineSegment(sketch, "E238", {"start": v(-11.08, -28.27) * mm, "end": v(-10.96, -28.15) * mm});
            skArc(sketch, "E239", {"start": v(-10.96, -28.15) * mm, "mid": v(-10.96, -28.1) * mm, "end": v(-11.02, -28.1) * mm});
            skLineSegment(sketch, "E240", {"start": v(-11.15, -28.25) * mm, "end": v(-11.15, -28.74) * mm});
            skArc(sketch, "E241", {"start": v(-11.15, -28.74) * mm, "mid": v(-11.11, -28.78) * mm, "end": v(-11.07, -28.74) * mm});
            skLineSegment(sketch, "E242", {"start": v(-11.07, -28.74) * mm, "end": v(-11.07, -28.25) * mm});
            skArc(sketch, "E243", {"start": v(-11.07, -28.25) * mm, "mid": v(-11.11, -28.2) * mm, "end": v(-11.15, -28.25) * mm});
            skLineSegment(sketch, "E244", {"start": v(-11.14, -28.76) * mm, "end": v(-11.02, -28.89) * mm});
            skArc(sketch, "E245", {"start": v(-11.02, -28.89) * mm, "mid": v(-10.96, -28.89) * mm, "end": v(-10.96, -28.83) * mm});
            skLineSegment(sketch, "E246", {"start": v(-10.96, -28.83) * mm, "end": v(-11.08, -28.71) * mm});
            skArc(sketch, "E247", {"start": v(-11.08, -28.71) * mm, "mid": v(-11.14, -28.71) * mm, "end": v(-11.14, -28.76) * mm});
            skLineSegment(sketch, "E248", {"start": v(-10.99, -28.9) * mm, "end": v(-10.74, -28.9) * mm});
            skArc(sketch, "E249", {"start": v(-10.74, -28.9) * mm, "mid": v(-10.7, -28.86) * mm, "end": v(-10.74, -28.82) * mm});
            skLineSegment(sketch, "E250", {"start": v(-10.74, -28.82) * mm, "end": v(-10.99, -28.82) * mm});
            skArc(sketch, "E251", {"start": v(-10.99, -28.82) * mm, "mid": v(-11.03, -28.86) * mm, "end": v(-10.99, -28.9) * mm});
            skLineSegment(sketch, "E252", {"start": v(-10.72, -28.89) * mm, "end": v(-10.6, -28.76) * mm});
            skArc(sketch, "E253", {"start": v(-10.6, -28.76) * mm, "mid": v(-10.6, -28.71) * mm, "end": v(-10.65, -28.71) * mm});
            skLineSegment(sketch, "E254", {"start": v(-10.65, -28.71) * mm, "end": v(-10.77, -28.83) * mm});
            skArc(sketch, "E255", {"start": v(-10.77, -28.83) * mm, "mid": v(-10.77, -28.89) * mm, "end": v(-10.72, -28.89) * mm});
            skLineSegment(sketch, "E256", {"start": v(-10.58, -28.74) * mm, "end": v(-10.58, -28.25) * mm});
            skArc(sketch, "E257", {"start": v(-10.58, -28.25) * mm, "mid": v(-10.62, -28.2) * mm, "end": v(-10.66, -28.25) * mm});
            skLineSegment(sketch, "E258", {"start": v(-10.66, -28.25) * mm, "end": v(-10.66, -28.74) * mm});
            skArc(sketch, "E259", {"start": v(-10.66, -28.74) * mm, "mid": v(-10.62, -28.78) * mm, "end": v(-10.58, -28.74) * mm});
            skLineSegment(sketch, "E260", {"start": v(-10.6, -28.22) * mm, "end": v(-10.72, -28.1) * mm});
            skArc(sketch, "E261", {"start": v(-10.72, -28.1) * mm, "mid": v(-10.77, -28.1) * mm, "end": v(-10.77, -28.15) * mm});
            skLineSegment(sketch, "E262", {"start": v(-10.77, -28.15) * mm, "end": v(-10.65, -28.27) * mm});
            skArc(sketch, "E263", {"start": v(-10.65, -28.27) * mm, "mid": v(-10.6, -28.27) * mm, "end": v(-10.6, -28.22) * mm});
            skLineSegment(sketch, "E264", {"start": v(-10.33, -28.86) * mm, "end": v(-10.33, -28.12) * mm});
            skArc(sketch, "E265", {"start": v(-10.33, -28.12) * mm, "mid": v(-10.36, -28.09) * mm, "end": v(-10.4, -28.12) * mm});
            skLineSegment(sketch, "E266", {"start": v(-10.4, -28.12) * mm, "end": v(-10.4, -28.86) * mm});
            skArc(sketch, "E267", {"start": v(-10.4, -28.86) * mm, "mid": v(-10.36, -28.9) * mm, "end": v(-10.33, -28.86) * mm});
            skLineSegment(sketch, "E268", {"start": v(-10.36, -28.16) * mm, "end": v(-10, -28.16) * mm});
            skArc(sketch, "E269", {"start": v(-10, -28.16) * mm, "mid": v(-9.96, -28.12) * mm, "end": v(-10, -28.09) * mm});
            skLineSegment(sketch, "E270", {"start": v(-10, -28.09) * mm, "end": v(-10.36, -28.09) * mm});
            skArc(sketch, "E271", {"start": v(-10.36, -28.09) * mm, "mid": v(-10.4, -28.12) * mm, "end": v(-10.36, -28.16) * mm});
            skLineSegment(sketch, "E272", {"start": v(-10.02, -28.15) * mm, "end": v(-9.9, -28.27) * mm});
            skArc(sketch, "E273", {"start": v(-9.9, -28.27) * mm, "mid": v(-9.85, -28.27) * mm, "end": v(-9.85, -28.22) * mm});
            skLineSegment(sketch, "E274", {"start": v(-9.84, -28.22) * mm, "end": v(-9.97, -28.1) * mm});
            skArc(sketch, "E275", {"start": v(-9.97, -28.1) * mm, "mid": v(-10.02, -28.1) * mm, "end": v(-10.02, -28.15) * mm});
            skLineSegment(sketch, "E276", {"start": v(-9.91, -28.25) * mm, "end": v(-9.91, -28.5) * mm});
            skArc(sketch, "E277", {"start": v(-9.91, -28.5) * mm, "mid": v(-9.87, -28.53) * mm, "end": v(-9.83, -28.5) * mm});
            skLineSegment(sketch, "E278", {"start": v(-9.83, -28.5) * mm, "end": v(-9.83, -28.25) * mm});
            skArc(sketch, "E279", {"start": v(-9.83, -28.25) * mm, "mid": v(-9.87, -28.2) * mm, "end": v(-9.91, -28.25) * mm});
            skLineSegment(sketch, "E280", {"start": v(-9.9, -28.46) * mm, "end": v(-10.02, -28.59) * mm});
            skArc(sketch, "E281", {"start": v(-10.02, -28.59) * mm, "mid": v(-10.02, -28.64) * mm, "end": v(-9.97, -28.64) * mm});
            skLineSegment(sketch, "E282", {"start": v(-9.97, -28.64) * mm, "end": v(-9.84, -28.52) * mm});
            skArc(sketch, "E283", {"start": v(-9.85, -28.52) * mm, "mid": v(-9.85, -28.46) * mm, "end": v(-9.9, -28.46) * mm});
            skLineSegment(sketch, "E284", {"start": v(-10, -28.58) * mm, "end": v(-10.36, -28.58) * mm});
            skArc(sketch, "E285", {"start": v(-10.36, -28.58) * mm, "mid": v(-10.4, -28.61) * mm, "end": v(-10.36, -28.65) * mm});
            skLineSegment(sketch, "E286", {"start": v(-10.36, -28.65) * mm, "end": v(-10, -28.65) * mm});
            skArc(sketch, "E287", {"start": v(-10, -28.65) * mm, "mid": v(-9.96, -28.61) * mm, "end": v(-10, -28.58) * mm});
            skLineSegment(sketch, "E288", {"start": v(-10.14, -28.64) * mm, "end": v(-9.9, -28.89) * mm});
            skArc(sketch, "E289", {"start": v(-9.9, -28.89) * mm, "mid": v(-9.85, -28.89) * mm, "end": v(-9.84, -28.83) * mm});
            skLineSegment(sketch, "E290", {"start": v(-9.84, -28.83) * mm, "end": v(-10.1, -28.59) * mm});
            skArc(sketch, "E291", {"start": v(-10.1, -28.59) * mm, "mid": v(-10.14, -28.59) * mm, "end": v(-10.14, -28.64) * mm});
            skLineSegment(sketch, "E292", {"start": v(-11.34, -36.22) * mm, "end": v(-11.46, -36.1) * mm});
            skArc(sketch, "E293", {"start": v(-11.46, -36.1) * mm, "mid": v(-11.52, -36.1) * mm, "end": v(-11.52, -36.15) * mm});
            skLineSegment(sketch, "E294", {"start": v(-11.52, -36.15) * mm, "end": v(-11.4, -36.27) * mm});
            skArc(sketch, "E295", {"start": v(-11.4, -36.27) * mm, "mid": v(-11.34, -36.27) * mm, "end": v(-11.34, -36.22) * mm});
            skLineSegment(sketch, "E296", {"start": v(-11.5, -36.09) * mm, "end": v(-11.74, -36.09) * mm});
            skArc(sketch, "E297", {"start": v(-11.74, -36.09) * mm, "mid": v(-11.78, -36.12) * mm, "end": v(-11.74, -36.16) * mm});
            skLineSegment(sketch, "E298", {"start": v(-11.74, -36.16) * mm, "end": v(-11.5, -36.16) * mm});
            skArc(sketch, "E299", {"start": v(-11.5, -36.16) * mm, "mid": v(-11.45, -36.12) * mm, "end": v(-11.5, -36.09) * mm});
            skLineSegment(sketch, "E300", {"start": v(-11.76, -36.1) * mm, "end": v(-11.89, -36.22) * mm});
            skArc(sketch, "E301", {"start": v(-11.89, -36.22) * mm, "mid": v(-11.89, -36.27) * mm, "end": v(-11.83, -36.27) * mm});
            skLineSegment(sketch, "E302", {"start": v(-11.83, -36.27) * mm, "end": v(-11.71, -36.15) * mm});
            skArc(sketch, "E303", {"start": v(-11.71, -36.15) * mm, "mid": v(-11.71, -36.1) * mm, "end": v(-11.76, -36.1) * mm});
            skLineSegment(sketch, "E304", {"start": v(-11.9, -36.25) * mm, "end": v(-11.9, -36.37) * mm});
            skArc(sketch, "E305", {"start": v(-11.9, -36.37) * mm, "mid": v(-11.86, -36.4) * mm, "end": v(-11.82, -36.37) * mm});
            skLineSegment(sketch, "E306", {"start": v(-11.82, -36.37) * mm, "end": v(-11.82, -36.25) * mm});
            skArc(sketch, "E307", {"start": v(-11.82, -36.25) * mm, "mid": v(-11.86, -36.2) * mm, "end": v(-11.9, -36.25) * mm});
            skLineSegment(sketch, "E308", {"start": v(-11.89, -36.4) * mm, "end": v(-11.76, -36.52) * mm});
            skArc(sketch, "E309", {"start": v(-11.76, -36.52) * mm, "mid": v(-11.71, -36.52) * mm, "end": v(-11.71, -36.46) * mm});
            skLineSegment(sketch, "E310", {"start": v(-11.71, -36.46) * mm, "end": v(-11.83, -36.34) * mm});
            skArc(sketch, "E311", {"start": v(-11.83, -36.34) * mm, "mid": v(-11.89, -36.34) * mm, "end": v(-11.89, -36.4) * mm});
            skLineSegment(sketch, "E312", {"start": v(-11.74, -36.53) * mm, "end": v(-11.5, -36.53) * mm});
            skArc(sketch, "E313", {"start": v(-11.5, -36.53) * mm, "mid": v(-11.45, -36.5) * mm, "end": v(-11.5, -36.45) * mm});
            skLineSegment(sketch, "E314", {"start": v(-11.5, -36.45) * mm, "end": v(-11.74, -36.45) * mm});
            skArc(sketch, "E315", {"start": v(-11.74, -36.45) * mm, "mid": v(-11.78, -36.5) * mm, "end": v(-11.74, -36.53) * mm});
            skLineSegment(sketch, "E316", {"start": v(-11.52, -36.52) * mm, "end": v(-11.4, -36.64) * mm});
            skArc(sketch, "E317", {"start": v(-11.4, -36.64) * mm, "mid": v(-11.34, -36.64) * mm, "end": v(-11.34, -36.59) * mm});
            skLineSegment(sketch, "E318", {"start": v(-11.34, -36.59) * mm, "end": v(-11.46, -36.46) * mm});
            skArc(sketch, "E319", {"start": v(-11.46, -36.46) * mm, "mid": v(-11.52, -36.46) * mm, "end": v(-11.52, -36.52) * mm});
            skLineSegment(sketch, "E320", {"start": v(-11.4, -36.61) * mm, "end": v(-11.4, -36.74) * mm});
            skArc(sketch, "E321", {"start": v(-11.4, -36.74) * mm, "mid": v(-11.37, -36.78) * mm, "end": v(-11.33, -36.74) * mm});
            skLineSegment(sketch, "E322", {"start": v(-11.33, -36.74) * mm, "end": v(-11.33, -36.61) * mm});
            skArc(sketch, "E323", {"start": v(-11.33, -36.61) * mm, "mid": v(-11.37, -36.58) * mm, "end": v(-11.4, -36.61) * mm});
            skLineSegment(sketch, "E324", {"start": v(-11.4, -36.71) * mm, "end": v(-11.52, -36.83) * mm});
            skArc(sketch, "E325", {"start": v(-11.52, -36.83) * mm, "mid": v(-11.52, -36.89) * mm, "end": v(-11.46, -36.89) * mm});
            skLineSegment(sketch, "E326", {"start": v(-11.46, -36.89) * mm, "end": v(-11.34, -36.76) * mm});
            skArc(sketch, "E327", {"start": v(-11.34, -36.76) * mm, "mid": v(-11.34, -36.71) * mm, "end": v(-11.4, -36.71) * mm});
            skLineSegment(sketch, "E328", {"start": v(-11.5, -36.82) * mm, "end": v(-11.74, -36.82) * mm});
            skArc(sketch, "E329", {"start": v(-11.74, -36.82) * mm, "mid": v(-11.78, -36.86) * mm, "end": v(-11.74, -36.9) * mm});
            skLineSegment(sketch, "E330", {"start": v(-11.74, -36.9) * mm, "end": v(-11.5, -36.9) * mm});
            skArc(sketch, "E331", {"start": v(-11.5, -36.9) * mm, "mid": v(-11.45, -36.86) * mm, "end": v(-11.5, -36.82) * mm});
            skLineSegment(sketch, "E332", {"start": v(-11.71, -36.83) * mm, "end": v(-11.83, -36.71) * mm});
            skArc(sketch, "E333", {"start": v(-11.83, -36.71) * mm, "mid": v(-11.89, -36.71) * mm, "end": v(-11.89, -36.76) * mm});
            skLineSegment(sketch, "E334", {"start": v(-11.89, -36.76) * mm, "end": v(-11.76, -36.89) * mm});
            skArc(sketch, "E335", {"start": v(-11.76, -36.89) * mm, "mid": v(-11.71, -36.89) * mm, "end": v(-11.71, -36.83) * mm});
            skLineSegment(sketch, "E336", {"start": v(-10.83, -36.86) * mm, "end": v(-10.83, -36.12) * mm});
            skArc(sketch, "E337", {"start": v(-10.83, -36.12) * mm, "mid": v(-10.87, -36.09) * mm, "end": v(-10.9, -36.12) * mm});
            skLineSegment(sketch, "E338", {"start": v(-10.9, -36.12) * mm, "end": v(-10.9, -36.86) * mm});
            skArc(sketch, "E339", {"start": v(-10.9, -36.86) * mm, "mid": v(-10.87, -36.9) * mm, "end": v(-10.83, -36.86) * mm});
            skLineSegment(sketch, "E340", {"start": v(-11.11, -36.16) * mm, "end": v(-10.62, -36.16) * mm});
            skArc(sketch, "E341", {"start": v(-10.62, -36.16) * mm, "mid": v(-10.58, -36.12) * mm, "end": v(-10.62, -36.09) * mm});
            skLineSegment(sketch, "E342", {"start": v(-10.62, -36.09) * mm, "end": v(-11.11, -36.09) * mm});
            skArc(sketch, "E343", {"start": v(-11.11, -36.09) * mm, "mid": v(-11.15, -36.12) * mm, "end": v(-11.11, -36.16) * mm});
            skLineSegment(sketch, "E344", {"start": v(-10, -36.09) * mm, "end": v(-10.24, -36.09) * mm});
            skArc(sketch, "E345", {"start": v(-10.24, -36.09) * mm, "mid": v(-10.28, -36.12) * mm, "end": v(-10.24, -36.16) * mm});
            skLineSegment(sketch, "E346", {"start": v(-10.24, -36.16) * mm, "end": v(-10, -36.16) * mm});
            skArc(sketch, "E347", {"start": v(-10, -36.16) * mm, "mid": v(-9.96, -36.12) * mm, "end": v(-10, -36.09) * mm});
            skLineSegment(sketch, "E348", {"start": v(-10.27, -36.1) * mm, "end": v(-10.4, -36.22) * mm});
            skArc(sketch, "E349", {"start": v(-10.4, -36.22) * mm, "mid": v(-10.4, -36.27) * mm, "end": v(-10.34, -36.27) * mm});
            skLineSegment(sketch, "E350", {"start": v(-10.34, -36.27) * mm, "end": v(-10.21, -36.15) * mm});
            skArc(sketch, "E351", {"start": v(-10.21, -36.15) * mm, "mid": v(-10.21, -36.1) * mm, "end": v(-10.27, -36.1) * mm});
            skLineSegment(sketch, "E352", {"start": v(-10.4, -36.25) * mm, "end": v(-10.4, -36.74) * mm});
            skArc(sketch, "E353", {"start": v(-10.4, -36.74) * mm, "mid": v(-10.36, -36.78) * mm, "end": v(-10.33, -36.74) * mm});
            skLineSegment(sketch, "E354", {"start": v(-10.33, -36.74) * mm, "end": v(-10.33, -36.25) * mm});
            skArc(sketch, "E355", {"start": v(-10.33, -36.25) * mm, "mid": v(-10.36, -36.2) * mm, "end": v(-10.4, -36.25) * mm});
            skLineSegment(sketch, "E356", {"start": v(-10.4, -36.76) * mm, "end": v(-10.27, -36.89) * mm});
            skArc(sketch, "E357", {"start": v(-10.27, -36.89) * mm, "mid": v(-10.21, -36.89) * mm, "end": v(-10.21, -36.83) * mm});
            skLineSegment(sketch, "E358", {"start": v(-10.21, -36.83) * mm, "end": v(-10.34, -36.71) * mm});
            skArc(sketch, "E359", {"start": v(-10.34, -36.71) * mm, "mid": v(-10.4, -36.71) * mm, "end": v(-10.4, -36.76) * mm});
            skLineSegment(sketch, "E360", {"start": v(-10.24, -36.9) * mm, "end": v(-10, -36.9) * mm});
            skArc(sketch, "E361", {"start": v(-10, -36.9) * mm, "mid": v(-9.96, -36.86) * mm, "end": v(-10, -36.82) * mm});
            skLineSegment(sketch, "E362", {"start": v(-10, -36.82) * mm, "end": v(-10.24, -36.82) * mm});
            skArc(sketch, "E363", {"start": v(-10.24, -36.82) * mm, "mid": v(-10.28, -36.86) * mm, "end": v(-10.24, -36.9) * mm});
            skLineSegment(sketch, "E364", {"start": v(-9.97, -36.89) * mm, "end": v(-9.84, -36.76) * mm});
            skArc(sketch, "E365", {"start": v(-9.85, -36.76) * mm, "mid": v(-9.85, -36.71) * mm, "end": v(-9.9, -36.71) * mm});
            skLineSegment(sketch, "E366", {"start": v(-9.9, -36.71) * mm, "end": v(-10.02, -36.83) * mm});
            skArc(sketch, "E367", {"start": v(-10.02, -36.83) * mm, "mid": v(-10.02, -36.89) * mm, "end": v(-9.97, -36.89) * mm});
            skLineSegment(sketch, "E368", {"start": v(-9.83, -36.74) * mm, "end": v(-9.83, -36.25) * mm});
            skArc(sketch, "E369", {"start": v(-9.83, -36.25) * mm, "mid": v(-9.87, -36.2) * mm, "end": v(-9.91, -36.25) * mm});
            skLineSegment(sketch, "E370", {"start": v(-9.91, -36.25) * mm, "end": v(-9.91, -36.74) * mm});
            skArc(sketch, "E371", {"start": v(-9.91, -36.74) * mm, "mid": v(-9.87, -36.78) * mm, "end": v(-9.83, -36.74) * mm});
            skLineSegment(sketch, "E372", {"start": v(-9.84, -36.22) * mm, "end": v(-9.97, -36.1) * mm});
            skArc(sketch, "E373", {"start": v(-9.97, -36.1) * mm, "mid": v(-10.02, -36.1) * mm, "end": v(-10.02, -36.15) * mm});
            skLineSegment(sketch, "E374", {"start": v(-10.02, -36.15) * mm, "end": v(-9.9, -36.27) * mm});
            skArc(sketch, "E375", {"start": v(-9.9, -36.27) * mm, "mid": v(-9.85, -36.27) * mm, "end": v(-9.85, -36.22) * mm});
            skLineSegment(sketch, "E376", {"start": v(-9.58, -36.86) * mm, "end": v(-9.58, -36.12) * mm});
            skArc(sketch, "E377", {"start": v(-9.58, -36.12) * mm, "mid": v(-9.62, -36.09) * mm, "end": v(-9.65, -36.12) * mm});
            skLineSegment(sketch, "E378", {"start": v(-9.65, -36.12) * mm, "end": v(-9.65, -36.86) * mm});
            skArc(sketch, "E379", {"start": v(-9.65, -36.86) * mm, "mid": v(-9.62, -36.9) * mm, "end": v(-9.58, -36.86) * mm});
            skLineSegment(sketch, "E380", {"start": v(-9.62, -36.16) * mm, "end": v(-9.25, -36.16) * mm});
            skArc(sketch, "E381", {"start": v(-9.25, -36.16) * mm, "mid": v(-9.2, -36.12) * mm, "end": v(-9.25, -36.09) * mm});
            skLineSegment(sketch, "E382", {"start": v(-9.25, -36.09) * mm, "end": v(-9.62, -36.09) * mm});
            skArc(sketch, "E383", {"start": v(-9.62, -36.09) * mm, "mid": v(-9.65, -36.12) * mm, "end": v(-9.62, -36.16) * mm});
            skLineSegment(sketch, "E384", {"start": v(-9.27, -36.15) * mm, "end": v(-9.15, -36.27) * mm});
            skArc(sketch, "E385", {"start": v(-9.15, -36.27) * mm, "mid": v(-9.1, -36.27) * mm, "end": v(-9.1, -36.22) * mm});
            skLineSegment(sketch, "E386", {"start": v(-9.1, -36.22) * mm, "end": v(-9.22, -36.1) * mm});
            skArc(sketch, "E387", {"start": v(-9.22, -36.1) * mm, "mid": v(-9.27, -36.1) * mm, "end": v(-9.27, -36.15) * mm});
            skLineSegment(sketch, "E388", {"start": v(-9.16, -36.25) * mm, "end": v(-9.16, -36.5) * mm});
            skArc(sketch, "E389", {"start": v(-9.16, -36.5) * mm, "mid": v(-9.12, -36.53) * mm, "end": v(-9.09, -36.5) * mm});
            skLineSegment(sketch, "E390", {"start": v(-9.09, -36.5) * mm, "end": v(-9.09, -36.25) * mm});
            skArc(sketch, "E391", {"start": v(-9.09, -36.25) * mm, "mid": v(-9.12, -36.2) * mm, "end": v(-9.16, -36.25) * mm});
            skLineSegment(sketch, "E392", {"start": v(-9.15, -36.46) * mm, "end": v(-9.27, -36.59) * mm});
            skArc(sketch, "E393", {"start": v(-9.27, -36.59) * mm, "mid": v(-9.27, -36.64) * mm, "end": v(-9.22, -36.64) * mm});
            skLineSegment(sketch, "E394", {"start": v(-9.22, -36.64) * mm, "end": v(-9.1, -36.52) * mm});
            skArc(sketch, "E395", {"start": v(-9.1, -36.52) * mm, "mid": v(-9.1, -36.46) * mm, "end": v(-9.15, -36.46) * mm});
            skLineSegment(sketch, "E396", {"start": v(-9.25, -36.58) * mm, "end": v(-9.62, -36.58) * mm});
            skArc(sketch, "E397", {"start": v(-9.62, -36.58) * mm, "mid": v(-9.65, -36.61) * mm, "end": v(-9.62, -36.65) * mm});
            skLineSegment(sketch, "E398", {"start": v(-9.62, -36.65) * mm, "end": v(-9.25, -36.65) * mm});
            skArc(sketch, "E399", {"start": v(-9.25, -36.65) * mm, "mid": v(-9.2, -36.61) * mm, "end": v(-9.25, -36.58) * mm});
            skLineSegment(sketch, "E400", {"start": v(-11.82, -34.86) * mm, "end": v(-11.82, -34.12) * mm});
            skArc(sketch, "E401", {"start": v(-11.82, -34.12) * mm, "mid": v(-11.86, -34.09) * mm, "end": v(-11.9, -34.12) * mm});
            skLineSegment(sketch, "E402", {"start": v(-11.9, -34.12) * mm, "end": v(-11.9, -34.86) * mm});
            skArc(sketch, "E403", {"start": v(-11.9, -34.86) * mm, "mid": v(-11.86, -34.9) * mm, "end": v(-11.82, -34.86) * mm});
            skLineSegment(sketch, "E404", {"start": v(-11.9, -34.14) * mm, "end": v(-11.4, -34.88) * mm});
            skArc(sketch, "E405", {"start": v(-11.4, -34.88) * mm, "mid": v(-11.35, -34.9) * mm, "end": v(-11.34, -34.84) * mm});
            skLineSegment(sketch, "E406", {"start": v(-11.34, -34.84) * mm, "end": v(-11.83, -34.1) * mm});
            skArc(sketch, "E407", {"start": v(-11.83, -34.1) * mm, "mid": v(-11.88, -34.1) * mm, "end": v(-11.9, -34.14) * mm});
            skLineSegment(sketch, "E408", {"start": v(-11.33, -34.86) * mm, "end": v(-11.33, -34.12) * mm});
            skArc(sketch, "E409", {"start": v(-11.33, -34.12) * mm, "mid": v(-11.37, -34.09) * mm, "end": v(-11.4, -34.12) * mm});
            skLineSegment(sketch, "E410", {"start": v(-11.4, -34.12) * mm, "end": v(-11.4, -34.86) * mm});
            skArc(sketch, "E411", {"start": v(-11.4, -34.86) * mm, "mid": v(-11.37, -34.9) * mm, "end": v(-11.33, -34.86) * mm});
            skLineSegment(sketch, "E412", {"start": v(-11.07, -34.86) * mm, "end": v(-11.07, -34.37) * mm});
            skArc(sketch, "E413", {"start": v(-11.07, -34.37) * mm, "mid": v(-11.11, -34.33) * mm, "end": v(-11.15, -34.37) * mm});
            skLineSegment(sketch, "E414", {"start": v(-11.15, -34.37) * mm, "end": v(-11.15, -34.86) * mm});
            skArc(sketch, "E415", {"start": v(-11.15, -34.86) * mm, "mid": v(-11.11, -34.9) * mm, "end": v(-11.07, -34.86) * mm});
            skLineSegment(sketch, "E416", {"start": v(-11.08, -34.4) * mm, "end": v(-10.84, -34.15) * mm});
            skArc(sketch, "E417", {"start": v(-10.84, -34.15) * mm, "mid": v(-10.84, -34.1) * mm, "end": v(-10.9, -34.1) * mm});
            skLineSegment(sketch, "E418", {"start": v(-10.9, -34.1) * mm, "end": v(-11.14, -34.34) * mm});
            skArc(sketch, "E419", {"start": v(-11.14, -34.34) * mm, "mid": v(-11.14, -34.4) * mm, "end": v(-11.08, -34.4) * mm});
            skLineSegment(sketch, "E420", {"start": v(-10.9, -34.15) * mm, "end": v(-10.65, -34.4) * mm});
            skArc(sketch, "E421", {"start": v(-10.65, -34.4) * mm, "mid": v(-10.6, -34.4) * mm, "end": v(-10.6, -34.34) * mm});
            skLineSegment(sketch, "E422", {"start": v(-10.6, -34.34) * mm, "end": v(-10.84, -34.1) * mm});
            skArc(sketch, "E423", {"start": v(-10.84, -34.1) * mm, "mid": v(-10.9, -34.1) * mm, "end": v(-10.9, -34.15) * mm});
            skLineSegment(sketch, "E424", {"start": v(-10.66, -34.37) * mm, "end": v(-10.66, -34.86) * mm});
            skArc(sketch, "E425", {"start": v(-10.66, -34.86) * mm, "mid": v(-10.62, -34.9) * mm, "end": v(-10.58, -34.86) * mm});
            skLineSegment(sketch, "E426", {"start": v(-10.58, -34.86) * mm, "end": v(-10.58, -34.37) * mm});
            skArc(sketch, "E427", {"start": v(-10.58, -34.37) * mm, "mid": v(-10.62, -34.33) * mm, "end": v(-10.66, -34.37) * mm});
            skLineSegment(sketch, "E428", {"start": v(-11.11, -34.53) * mm, "end": v(-10.62, -34.53) * mm});
            skArc(sketch, "E429", {"start": v(-10.62, -34.53) * mm, "mid": v(-10.58, -34.5) * mm, "end": v(-10.62, -34.45) * mm});
            skLineSegment(sketch, "E430", {"start": v(-10.62, -34.45) * mm, "end": v(-11.11, -34.45) * mm});
            skArc(sketch, "E431", {"start": v(-11.11, -34.45) * mm, "mid": v(-11.15, -34.5) * mm, "end": v(-11.11, -34.53) * mm});
            skLineSegment(sketch, "E432", {"start": v(-10.36, -34.9) * mm, "end": v(-10.12, -34.9) * mm});
            skArc(sketch, "E433", {"start": v(-10.12, -34.9) * mm, "mid": v(-10.08, -34.86) * mm, "end": v(-10.12, -34.82) * mm});
            skLineSegment(sketch, "E434", {"start": v(-10.12, -34.82) * mm, "end": v(-10.36, -34.82) * mm});
            skArc(sketch, "E435", {"start": v(-10.36, -34.82) * mm, "mid": v(-10.4, -34.86) * mm, "end": v(-10.36, -34.9) * mm});
            skLineSegment(sketch, "E436", {"start": v(-10.2, -34.86) * mm, "end": v(-10.2, -34.12) * mm});
            skArc(sketch, "E437", {"start": v(-10.2, -34.12) * mm, "mid": v(-10.24, -34.09) * mm, "end": v(-10.28, -34.12) * mm});
            skLineSegment(sketch, "E438", {"start": v(-10.28, -34.12) * mm, "end": v(-10.28, -34.86) * mm});
            skArc(sketch, "E439", {"start": v(-10.28, -34.86) * mm, "mid": v(-10.24, -34.9) * mm, "end": v(-10.2, -34.86) * mm});
            skLineSegment(sketch, "E440", {"start": v(-10.36, -34.16) * mm, "end": v(-10.12, -34.16) * mm});
            skArc(sketch, "E441", {"start": v(-10.12, -34.16) * mm, "mid": v(-10.08, -34.12) * mm, "end": v(-10.12, -34.09) * mm});
            skLineSegment(sketch, "E442", {"start": v(-10.12, -34.09) * mm, "end": v(-10.36, -34.09) * mm});
            skArc(sketch, "E443", {"start": v(-10.36, -34.09) * mm, "mid": v(-10.4, -34.12) * mm, "end": v(-10.36, -34.16) * mm});
            skLineSegment(sketch, "E444", {"start": v(-9.9, -34.12) * mm, "end": v(-9.9, -34.86) * mm});
            skArc(sketch, "E445", {"start": v(-9.9, -34.86) * mm, "mid": v(-9.86, -34.9) * mm, "end": v(-9.83, -34.86) * mm});
            skLineSegment(sketch, "E446", {"start": v(-9.83, -34.86) * mm, "end": v(-9.83, -34.12) * mm});
            skArc(sketch, "E447", {"start": v(-9.83, -34.12) * mm, "mid": v(-9.86, -34.09) * mm, "end": v(-9.9, -34.12) * mm});
            skLineSegment(sketch, "E448", {"start": v(-9.84, -34.64) * mm, "end": v(-9.35, -34.15) * mm});
            skArc(sketch, "E449", {"start": v(-9.35, -34.15) * mm, "mid": v(-9.35, -34.1) * mm, "end": v(-9.4, -34.1) * mm});
            skLineSegment(sketch, "E450", {"start": v(-9.4, -34.1) * mm, "end": v(-9.9, -34.59) * mm});
            skArc(sketch, "E451", {"start": v(-9.9, -34.59) * mm, "mid": v(-9.9, -34.64) * mm, "end": v(-9.84, -34.64) * mm});
            skLineSegment(sketch, "E452", {"start": v(-9.77, -34.52) * mm, "end": v(-9.4, -34.89) * mm});
            skArc(sketch, "E453", {"start": v(-9.4, -34.89) * mm, "mid": v(-9.35, -34.89) * mm, "end": v(-9.35, -34.83) * mm});
            skLineSegment(sketch, "E454", {"start": v(-9.35, -34.83) * mm, "end": v(-9.71, -34.46) * mm});
            skArc(sketch, "E455", {"start": v(-9.71, -34.46) * mm, "mid": v(-9.77, -34.46) * mm, "end": v(-9.77, -34.52) * mm});
            skLineSegment(sketch, "E456", {"start": v(-37.99, -25.78) * mm, "end": v(-38.88, -25.78) * mm});
            skArc(sketch, "E457", {"start": v(-38.88, -25.78) * mm, "mid": v(-39.13, -26.04) * mm, "end": v(-38.88, -26.3) * mm});
            skLineSegment(sketch, "E458", {"start": v(-38.88, -26.3) * mm, "end": v(-37.99, -26.3) * mm});
            skArc(sketch, "E459", {"start": v(-37.99, -26.3) * mm, "mid": v(-37.73, -26.04) * mm, "end": v(-37.99, -25.78) * mm});
            skLineSegment(sketch, "E460", {"start": v(-45.6, -26.3) * mm, "end": v(-44.72, -26.3) * mm});
            skArc(sketch, "E461", {"start": v(-44.72, -26.3) * mm, "mid": v(-44.47, -26.04) * mm, "end": v(-44.72, -25.78) * mm});
            skLineSegment(sketch, "E462", {"start": v(-44.72, -25.78) * mm, "end": v(-45.6, -25.78) * mm});
            skArc(sketch, "E463", {"start": v(-45.6, -25.78) * mm, "mid": v(-45.86, -26.04) * mm, "end": v(-45.6, -26.3) * mm});
            skArc(sketch, "E464", {"start": v(-44.08, -25.1) * mm, "mid": v(-44, -25.02) * mm, "end": v(-44.08, -24.95) * mm});
            skArc(sketch, "E465", {"start": v(-44.08, -24.95) * mm, "mid": v(-44.32, -25.04) * mm, "end": v(-44.41, -25.28) * mm});
            skArc(sketch, "E466", {"start": v(-44.41, -25.28) * mm, "mid": v(-44.34, -25.35) * mm, "end": v(-44.26, -25.28) * mm});
            skArc(sketch, "E467", {"start": v(-44.26, -25.28) * mm, "mid": v(-44.21, -25.15) * mm, "end": v(-44.08, -25.1) * mm});
            skArc(sketch, "E468", {"start": v(-44.26, -26.8) * mm, "mid": v(-44.34, -26.72) * mm, "end": v(-44.41, -26.8) * mm});
            skArc(sketch, "E469", {"start": v(-44.41, -26.8) * mm, "mid": v(-44.32, -27.03) * mm, "end": v(-44.08, -27.13) * mm});
            skArc(sketch, "E470", {"start": v(-44.08, -27.13) * mm, "mid": v(-44, -27.05) * mm, "end": v(-44.08, -26.98) * mm});
            skArc(sketch, "E471", {"start": v(-44.08, -26.98) * mm, "mid": v(-44.21, -26.93) * mm, "end": v(-44.26, -26.8) * mm});
            skArc(sketch, "E472", {"start": v(-39.51, -26.98) * mm, "mid": v(-39.59, -27.05) * mm, "end": v(-39.51, -27.13) * mm});
            skArc(sketch, "E473", {"start": v(-39.51, -27.13) * mm, "mid": v(-39.28, -27.03) * mm, "end": v(-39.18, -26.8) * mm});
            skArc(sketch, "E474", {"start": v(-39.18, -26.8) * mm, "mid": v(-39.26, -26.72) * mm, "end": v(-39.33, -26.8) * mm});
            skArc(sketch, "E475", {"start": v(-39.33, -26.8) * mm, "mid": v(-39.39, -26.93) * mm, "end": v(-39.51, -26.98) * mm});
            skArc(sketch, "E476", {"start": v(-39.33, -25.28) * mm, "mid": v(-39.26, -25.35) * mm, "end": v(-39.18, -25.28) * mm});
            skArc(sketch, "E477", {"start": v(-39.18, -25.28) * mm, "mid": v(-39.28, -25.04) * mm, "end": v(-39.51, -24.95) * mm});
            skArc(sketch, "E478", {"start": v(-39.51, -24.95) * mm, "mid": v(-39.59, -25.02) * mm, "end": v(-39.51, -25.1) * mm});
            skArc(sketch, "E479", {"start": v(-39.51, -25.1) * mm, "mid": v(-39.39, -25.15) * mm, "end": v(-39.33, -25.28) * mm});
            skLineSegment(sketch, "E480", {"start": v(-44.26, -26.8) * mm, "end": v(-44.26, -25.28) * mm});
            skArc(sketch, "E481", {"start": v(-44.26, -25.28) * mm, "mid": v(-44.34, -25.2) * mm, "end": v(-44.41, -25.28) * mm});
            skLineSegment(sketch, "E482", {"start": v(-44.41, -25.28) * mm, "end": v(-44.41, -26.8) * mm});
            skArc(sketch, "E483", {"start": v(-44.41, -26.8) * mm, "mid": v(-44.34, -26.88) * mm, "end": v(-44.26, -26.8) * mm});
            skLineSegment(sketch, "E484", {"start": v(-44.08, -25.1) * mm, "end": v(-43.7, -25.1) * mm});
            skArc(sketch, "E485", {"start": v(-43.7, -25.1) * mm, "mid": v(-43.63, -25.02) * mm, "end": v(-43.7, -24.95) * mm});
            skLineSegment(sketch, "E486", {"start": v(-43.7, -24.95) * mm, "end": v(-44.08, -24.95) * mm});
            skArc(sketch, "E487", {"start": v(-44.08, -24.95) * mm, "mid": v(-44.16, -25.02) * mm, "end": v(-44.08, -25.1) * mm});
            skLineSegment(sketch, "E488", {"start": v(-43.52, -25.1) * mm, "end": v(-43.65, -24.97) * mm});
            skArc(sketch, "E489", {"start": v(-43.65, -24.97) * mm, "mid": v(-43.76, -24.97) * mm, "end": v(-43.76, -25.08) * mm});
            skLineSegment(sketch, "E490", {"start": v(-43.76, -25.08) * mm, "end": v(-43.63, -25.2) * mm});
            skArc(sketch, "E491", {"start": v(-43.63, -25.2) * mm, "mid": v(-43.52, -25.2) * mm, "end": v(-43.52, -25.1) * mm});
            skLineSegment(sketch, "E492", {"start": v(-44.08, -27.13) * mm, "end": v(-43.7, -27.13) * mm});
            skArc(sketch, "E493", {"start": v(-43.7, -27.13) * mm, "mid": v(-43.63, -27.05) * mm, "end": v(-43.7, -26.98) * mm});
            skLineSegment(sketch, "E494", {"start": v(-43.7, -26.98) * mm, "end": v(-44.08, -26.98) * mm});
            skArc(sketch, "E495", {"start": v(-44.08, -26.98) * mm, "mid": v(-44.16, -27.05) * mm, "end": v(-44.08, -27.13) * mm});
            skLineSegment(sketch, "E496", {"start": v(-43.63, -26.87) * mm, "end": v(-43.76, -27) * mm});
            skArc(sketch, "E497", {"start": v(-43.76, -27) * mm, "mid": v(-43.76, -27.1) * mm, "end": v(-43.65, -27.1) * mm});
            skLineSegment(sketch, "E498", {"start": v(-43.65, -27.1) * mm, "end": v(-43.52, -26.98) * mm});
            skArc(sketch, "E499", {"start": v(-43.52, -26.98) * mm, "mid": v(-43.52, -26.87) * mm, "end": v(-43.63, -26.87) * mm});
            skLineSegment(sketch, "E500", {"start": v(-39.97, -25.2) * mm, "end": v(-39.84, -25.08) * mm});
            skArc(sketch, "E501", {"start": v(-39.84, -25.08) * mm, "mid": v(-39.84, -24.97) * mm, "end": v(-39.95, -24.97) * mm});
            skLineSegment(sketch, "E502", {"start": v(-39.95, -24.97) * mm, "end": v(-40.07, -25.1) * mm});
            skArc(sketch, "E503", {"start": v(-40.07, -25.1) * mm, "mid": v(-40.07, -25.2) * mm, "end": v(-39.97, -25.2) * mm});
            skLineSegment(sketch, "E504", {"start": v(-40.02, -25.07) * mm, "end": v(-43.58, -25.07) * mm});
            skArc(sketch, "E505", {"start": v(-43.58, -25.07) * mm, "mid": v(-43.65, -25.15) * mm, "end": v(-43.58, -25.23) * mm});
            skLineSegment(sketch, "E506", {"start": v(-43.58, -25.23) * mm, "end": v(-40.02, -25.23) * mm});
            skArc(sketch, "E507", {"start": v(-40.02, -25.23) * mm, "mid": v(-39.94, -25.15) * mm, "end": v(-40.02, -25.07) * mm});
            skLineSegment(sketch, "E508", {"start": v(-40.07, -26.98) * mm, "end": v(-39.95, -27.1) * mm});
            skArc(sketch, "E509", {"start": v(-39.95, -27.1) * mm, "mid": v(-39.84, -27.1) * mm, "end": v(-39.84, -27) * mm});
            skLineSegment(sketch, "E510", {"start": v(-39.84, -27) * mm, "end": v(-39.97, -26.87) * mm});
            skArc(sketch, "E511", {"start": v(-39.97, -26.87) * mm, "mid": v(-40.07, -26.87) * mm, "end": v(-40.07, -26.98) * mm});
            skLineSegment(sketch, "E512", {"start": v(-40.02, -26.85) * mm, "end": v(-43.58, -26.85) * mm});
            skArc(sketch, "E513", {"start": v(-43.58, -26.85) * mm, "mid": v(-43.65, -26.93) * mm, "end": v(-43.58, -27) * mm});
            skLineSegment(sketch, "E514", {"start": v(-43.58, -27) * mm, "end": v(-40.02, -27) * mm});
            skArc(sketch, "E515", {"start": v(-40.02, -27) * mm, "mid": v(-39.94, -26.93) * mm, "end": v(-40.02, -26.85) * mm});
            skLineSegment(sketch, "E516", {"start": v(-39.51, -24.95) * mm, "end": v(-39.9, -24.95) * mm});
            skArc(sketch, "E517", {"start": v(-39.9, -24.95) * mm, "mid": v(-39.97, -25.02) * mm, "end": v(-39.9, -25.1) * mm});
            skLineSegment(sketch, "E518", {"start": v(-39.9, -25.1) * mm, "end": v(-39.51, -25.1) * mm});
            skArc(sketch, "E519", {"start": v(-39.51, -25.1) * mm, "mid": v(-39.44, -25.02) * mm, "end": v(-39.51, -24.95) * mm});
            skLineSegment(sketch, "E520", {"start": v(-39.51, -26.98) * mm, "end": v(-39.9, -26.98) * mm});
            skArc(sketch, "E521", {"start": v(-39.9, -26.98) * mm, "mid": v(-39.97, -27.05) * mm, "end": v(-39.9, -27.13) * mm});
            skLineSegment(sketch, "E522", {"start": v(-39.9, -27.13) * mm, "end": v(-39.51, -27.13) * mm});
            skArc(sketch, "E523", {"start": v(-39.51, -27.13) * mm, "mid": v(-39.44, -27.05) * mm, "end": v(-39.51, -26.98) * mm});
            skLineSegment(sketch, "E524", {"start": v(-39.18, -26.8) * mm, "end": v(-39.18, -25.28) * mm});
            skArc(sketch, "E525", {"start": v(-39.18, -25.28) * mm, "mid": v(-39.26, -25.2) * mm, "end": v(-39.33, -25.28) * mm});
            skLineSegment(sketch, "E526", {"start": v(-39.33, -25.28) * mm, "end": v(-39.33, -26.8) * mm});
            skArc(sketch, "E527", {"start": v(-39.33, -26.8) * mm, "mid": v(-39.26, -26.88) * mm, "end": v(-39.18, -26.8) * mm});
            skLineSegment(sketch, "E528", {"start": v(-46.27, -26.31) * mm, "end": v(-46.27, -25.76) * mm});
            skLineSegment(sketch, "E529", {"start": v(-46.27, -25.76) * mm, "end": v(-45.88, -25.38) * mm});
            skLineSegment(sketch, "E530", {"start": v(-45.88, -25.38) * mm, "end": v(-45.33, -25.38) * mm});
            skLineSegment(sketch, "E531", {"start": v(-45.33, -25.38) * mm, "end": v(-44.95, -25.76) * mm});
            skLineSegment(sketch, "E532", {"start": v(-44.95, -25.76) * mm, "end": v(-44.95, -26.31) * mm});
            skLineSegment(sketch, "E533", {"start": v(-44.95, -26.31) * mm, "end": v(-45.33, -26.7) * mm});
            skLineSegment(sketch, "E534", {"start": v(-45.33, -26.7) * mm, "end": v(-45.88, -26.7) * mm});
            skLineSegment(sketch, "E535", {"start": v(-45.88, -26.7) * mm, "end": v(-46.27, -26.31) * mm});
            skLineSegment(sketch, "E536", {"start": v(-38.65, -26.31) * mm, "end": v(-38.65, -25.76) * mm});
            skLineSegment(sketch, "E537", {"start": v(-38.65, -25.76) * mm, "end": v(-38.26, -25.38) * mm});
            skLineSegment(sketch, "E538", {"start": v(-38.26, -25.38) * mm, "end": v(-37.71, -25.38) * mm});
            skLineSegment(sketch, "E539", {"start": v(-37.71, -25.38) * mm, "end": v(-37.33, -25.76) * mm});
            skLineSegment(sketch, "E540", {"start": v(-37.33, -25.76) * mm, "end": v(-37.33, -26.31) * mm});
            skLineSegment(sketch, "E541", {"start": v(-37.33, -26.31) * mm, "end": v(-37.71, -26.7) * mm});
            skLineSegment(sketch, "E542", {"start": v(-37.71, -26.7) * mm, "end": v(-38.26, -26.7) * mm});
            skLineSegment(sketch, "E543", {"start": v(-38.26, -26.7) * mm, "end": v(-38.65, -26.31) * mm});
            skLineSegment(sketch, "E544", {"start": v(-37.99, -29.6) * mm, "end": v(-38.88, -29.6) * mm});
            skArc(sketch, "E545", {"start": v(-38.88, -29.6) * mm, "mid": v(-39.13, -29.85) * mm, "end": v(-38.88, -30.1) * mm});
            skLineSegment(sketch, "E546", {"start": v(-38.88, -30.1) * mm, "end": v(-37.99, -30.1) * mm});
            skArc(sketch, "E547", {"start": v(-37.99, -30.1) * mm, "mid": v(-37.73, -29.85) * mm, "end": v(-37.99, -29.6) * mm});
            skLineSegment(sketch, "E548", {"start": v(-45.6, -30.1) * mm, "end": v(-44.72, -30.1) * mm});
            skArc(sketch, "E549", {"start": v(-44.72, -30.1) * mm, "mid": v(-44.47, -29.85) * mm, "end": v(-44.72, -29.6) * mm});
            skLineSegment(sketch, "E550", {"start": v(-44.72, -29.6) * mm, "end": v(-45.6, -29.6) * mm});
            skArc(sketch, "E551", {"start": v(-45.6, -29.6) * mm, "mid": v(-45.86, -29.85) * mm, "end": v(-45.6, -30.1) * mm});
            skArc(sketch, "E552", {"start": v(-44.08, -28.9) * mm, "mid": v(-44, -28.83) * mm, "end": v(-44.08, -28.76) * mm});
            skArc(sketch, "E553", {"start": v(-44.08, -28.76) * mm, "mid": v(-44.32, -28.85) * mm, "end": v(-44.41, -29.09) * mm});
            skArc(sketch, "E554", {"start": v(-44.41, -29.09) * mm, "mid": v(-44.34, -29.16) * mm, "end": v(-44.26, -29.09) * mm});
            skArc(sketch, "E555", {"start": v(-44.26, -29.09) * mm, "mid": v(-44.21, -28.96) * mm, "end": v(-44.08, -28.9) * mm});
            skArc(sketch, "E556", {"start": v(-44.26, -30.61) * mm, "mid": v(-44.34, -30.53) * mm, "end": v(-44.41, -30.61) * mm});
            skArc(sketch, "E557", {"start": v(-44.41, -30.61) * mm, "mid": v(-44.32, -30.84) * mm, "end": v(-44.08, -30.94) * mm});
            skArc(sketch, "E558", {"start": v(-44.08, -30.94) * mm, "mid": v(-44, -30.86) * mm, "end": v(-44.08, -30.79) * mm});
            skArc(sketch, "E559", {"start": v(-44.08, -30.79) * mm, "mid": v(-44.21, -30.74) * mm, "end": v(-44.26, -30.61) * mm});
            skArc(sketch, "E560", {"start": v(-39.51, -30.79) * mm, "mid": v(-39.59, -30.86) * mm, "end": v(-39.51, -30.94) * mm});
            skArc(sketch, "E561", {"start": v(-39.51, -30.94) * mm, "mid": v(-39.28, -30.84) * mm, "end": v(-39.18, -30.61) * mm});
            skArc(sketch, "E562", {"start": v(-39.18, -30.61) * mm, "mid": v(-39.26, -30.53) * mm, "end": v(-39.33, -30.61) * mm});
            skArc(sketch, "E563", {"start": v(-39.33, -30.61) * mm, "mid": v(-39.39, -30.74) * mm, "end": v(-39.51, -30.79) * mm});
            skArc(sketch, "E564", {"start": v(-39.33, -29.09) * mm, "mid": v(-39.26, -29.16) * mm, "end": v(-39.18, -29.09) * mm});
            skArc(sketch, "E565", {"start": v(-39.18, -29.09) * mm, "mid": v(-39.28, -28.85) * mm, "end": v(-39.51, -28.76) * mm});
            skArc(sketch, "E566", {"start": v(-39.51, -28.76) * mm, "mid": v(-39.59, -28.83) * mm, "end": v(-39.51, -28.9) * mm});
            skArc(sketch, "E567", {"start": v(-39.51, -28.9) * mm, "mid": v(-39.39, -28.96) * mm, "end": v(-39.33, -29.09) * mm});
            skLineSegment(sketch, "E568", {"start": v(-44.26, -30.61) * mm, "end": v(-44.26, -29.09) * mm});
            skArc(sketch, "E569", {"start": v(-44.26, -29.09) * mm, "mid": v(-44.34, -29.01) * mm, "end": v(-44.41, -29.09) * mm});
            skLineSegment(sketch, "E570", {"start": v(-44.41, -29.09) * mm, "end": v(-44.41, -30.61) * mm});
            skArc(sketch, "E571", {"start": v(-44.41, -30.61) * mm, "mid": v(-44.34, -30.69) * mm, "end": v(-44.26, -30.61) * mm});
            skLineSegment(sketch, "E572", {"start": v(-44.08, -28.9) * mm, "end": v(-43.7, -28.9) * mm});
            skArc(sketch, "E573", {"start": v(-43.7, -28.9) * mm, "mid": v(-43.63, -28.83) * mm, "end": v(-43.7, -28.76) * mm});
            skLineSegment(sketch, "E574", {"start": v(-43.7, -28.76) * mm, "end": v(-44.08, -28.76) * mm});
            skArc(sketch, "E575", {"start": v(-44.08, -28.76) * mm, "mid": v(-44.16, -28.83) * mm, "end": v(-44.08, -28.9) * mm});
            skLineSegment(sketch, "E576", {"start": v(-43.52, -28.9) * mm, "end": v(-43.65, -28.78) * mm});
            skArc(sketch, "E577", {"start": v(-43.65, -28.78) * mm, "mid": v(-43.76, -28.78) * mm, "end": v(-43.76, -28.89) * mm});
            skLineSegment(sketch, "E578", {"start": v(-43.76, -28.89) * mm, "end": v(-43.63, -29.01) * mm});
            skArc(sketch, "E579", {"start": v(-43.63, -29.01) * mm, "mid": v(-43.52, -29.01) * mm, "end": v(-43.52, -28.9) * mm});
            skLineSegment(sketch, "E580", {"start": v(-44.08, -30.94) * mm, "end": v(-43.7, -30.94) * mm});
            skArc(sketch, "E581", {"start": v(-43.7, -30.94) * mm, "mid": v(-43.63, -30.86) * mm, "end": v(-43.7, -30.79) * mm});
            skLineSegment(sketch, "E582", {"start": v(-43.7, -30.79) * mm, "end": v(-44.08, -30.79) * mm});
            skArc(sketch, "E583", {"start": v(-44.08, -30.79) * mm, "mid": v(-44.16, -30.86) * mm, "end": v(-44.08, -30.94) * mm});
            skLineSegment(sketch, "E584", {"start": v(-43.63, -30.68) * mm, "end": v(-43.76, -30.81) * mm});
            skArc(sketch, "E585", {"start": v(-43.76, -30.81) * mm, "mid": v(-43.76, -30.92) * mm, "end": v(-43.65, -30.92) * mm});
            skLineSegment(sketch, "E586", {"start": v(-43.65, -30.92) * mm, "end": v(-43.52, -30.8) * mm});
            skArc(sketch, "E587", {"start": v(-43.52, -30.8) * mm, "mid": v(-43.52, -30.68) * mm, "end": v(-43.63, -30.68) * mm});
            skLineSegment(sketch, "E588", {"start": v(-39.97, -29.01) * mm, "end": v(-39.84, -28.89) * mm});
            skArc(sketch, "E589", {"start": v(-39.84, -28.89) * mm, "mid": v(-39.84, -28.78) * mm, "end": v(-39.95, -28.78) * mm});
            skLineSegment(sketch, "E590", {"start": v(-39.95, -28.78) * mm, "end": v(-40.07, -28.9) * mm});
            skArc(sketch, "E591", {"start": v(-40.07, -28.9) * mm, "mid": v(-40.07, -29.01) * mm, "end": v(-39.97, -29.01) * mm});
            skLineSegment(sketch, "E592", {"start": v(-40.02, -28.88) * mm, "end": v(-43.58, -28.88) * mm});
            skArc(sketch, "E593", {"start": v(-43.58, -28.88) * mm, "mid": v(-43.65, -28.96) * mm, "end": v(-43.58, -29.04) * mm});
            skLineSegment(sketch, "E594", {"start": v(-43.58, -29.04) * mm, "end": v(-40.02, -29.04) * mm});
            skArc(sketch, "E595", {"start": v(-40.02, -29.04) * mm, "mid": v(-39.94, -28.96) * mm, "end": v(-40.02, -28.88) * mm});
            skLineSegment(sketch, "E596", {"start": v(-40.07, -30.8) * mm, "end": v(-39.95, -30.92) * mm});
            skArc(sketch, "E597", {"start": v(-39.95, -30.92) * mm, "mid": v(-39.84, -30.92) * mm, "end": v(-39.84, -30.81) * mm});
            skLineSegment(sketch, "E598", {"start": v(-39.84, -30.81) * mm, "end": v(-39.97, -30.68) * mm});
            skArc(sketch, "E599", {"start": v(-39.97, -30.68) * mm, "mid": v(-40.07, -30.68) * mm, "end": v(-40.07, -30.8) * mm});
            skLineSegment(sketch, "E600", {"start": v(-40.02, -30.66) * mm, "end": v(-43.58, -30.66) * mm});
            skArc(sketch, "E601", {"start": v(-43.58, -30.66) * mm, "mid": v(-43.65, -30.74) * mm, "end": v(-43.58, -30.81) * mm});
            skLineSegment(sketch, "E602", {"start": v(-43.58, -30.81) * mm, "end": v(-40.02, -30.81) * mm});
            skArc(sketch, "E603", {"start": v(-40.02, -30.81) * mm, "mid": v(-39.94, -30.74) * mm, "end": v(-40.02, -30.66) * mm});
            skLineSegment(sketch, "E604", {"start": v(-39.51, -28.76) * mm, "end": v(-39.9, -28.76) * mm});
            skArc(sketch, "E605", {"start": v(-39.9, -28.76) * mm, "mid": v(-39.97, -28.83) * mm, "end": v(-39.9, -28.9) * mm});
            skLineSegment(sketch, "E606", {"start": v(-39.9, -28.9) * mm, "end": v(-39.51, -28.9) * mm});
            skArc(sketch, "E607", {"start": v(-39.51, -28.9) * mm, "mid": v(-39.44, -28.83) * mm, "end": v(-39.51, -28.76) * mm});
            skLineSegment(sketch, "E608", {"start": v(-39.51, -30.79) * mm, "end": v(-39.9, -30.79) * mm});
            skArc(sketch, "E609", {"start": v(-39.9, -30.79) * mm, "mid": v(-39.97, -30.86) * mm, "end": v(-39.9, -30.94) * mm});
            skLineSegment(sketch, "E610", {"start": v(-39.9, -30.94) * mm, "end": v(-39.51, -30.94) * mm});
            skArc(sketch, "E611", {"start": v(-39.51, -30.94) * mm, "mid": v(-39.44, -30.86) * mm, "end": v(-39.51, -30.79) * mm});
            skLineSegment(sketch, "E612", {"start": v(-39.18, -30.61) * mm, "end": v(-39.18, -29.09) * mm});
            skArc(sketch, "E613", {"start": v(-39.18, -29.09) * mm, "mid": v(-39.26, -29.01) * mm, "end": v(-39.33, -29.09) * mm});
            skLineSegment(sketch, "E614", {"start": v(-39.33, -29.09) * mm, "end": v(-39.33, -30.61) * mm});
            skArc(sketch, "E615", {"start": v(-39.33, -30.61) * mm, "mid": v(-39.26, -30.69) * mm, "end": v(-39.18, -30.61) * mm});
            skLineSegment(sketch, "E616", {"start": v(-46.27, -30.12) * mm, "end": v(-46.27, -29.57) * mm});
            skLineSegment(sketch, "E617", {"start": v(-46.27, -29.57) * mm, "end": v(-45.88, -29.19) * mm});
            skLineSegment(sketch, "E618", {"start": v(-45.88, -29.19) * mm, "end": v(-45.33, -29.19) * mm});
            skLineSegment(sketch, "E619", {"start": v(-45.33, -29.19) * mm, "end": v(-44.95, -29.57) * mm});
            skLineSegment(sketch, "E620", {"start": v(-44.95, -29.57) * mm, "end": v(-44.95, -30.12) * mm});
            skLineSegment(sketch, "E621", {"start": v(-44.95, -30.12) * mm, "end": v(-45.33, -30.5) * mm});
            skLineSegment(sketch, "E622", {"start": v(-45.33, -30.5) * mm, "end": v(-45.88, -30.5) * mm});
            skLineSegment(sketch, "E623", {"start": v(-45.88, -30.5) * mm, "end": v(-46.27, -30.12) * mm});
            skLineSegment(sketch, "E624", {"start": v(-38.65, -30.12) * mm, "end": v(-38.65, -29.57) * mm});
            skLineSegment(sketch, "E625", {"start": v(-38.65, -29.57) * mm, "end": v(-38.26, -29.19) * mm});
            skLineSegment(sketch, "E626", {"start": v(-38.26, -29.19) * mm, "end": v(-37.71, -29.19) * mm});
            skLineSegment(sketch, "E627", {"start": v(-37.71, -29.19) * mm, "end": v(-37.33, -29.57) * mm});
            skLineSegment(sketch, "E628", {"start": v(-37.33, -29.57) * mm, "end": v(-37.33, -30.12) * mm});
            skLineSegment(sketch, "E629", {"start": v(-37.33, -30.12) * mm, "end": v(-37.71, -30.5) * mm});
            skLineSegment(sketch, "E630", {"start": v(-37.71, -30.5) * mm, "end": v(-38.26, -30.5) * mm});
            skLineSegment(sketch, "E631", {"start": v(-38.26, -30.5) * mm, "end": v(-38.65, -30.12) * mm});
            skLineSegment(sketch, "E632", {"start": v(-37.99, -33.4) * mm, "end": v(-38.88, -33.4) * mm});
            skArc(sketch, "E633", {"start": v(-38.88, -33.4) * mm, "mid": v(-39.13, -33.66) * mm, "end": v(-38.88, -33.91) * mm});
            skLineSegment(sketch, "E634", {"start": v(-38.88, -33.91) * mm, "end": v(-37.99, -33.91) * mm});
            skArc(sketch, "E635", {"start": v(-37.99, -33.91) * mm, "mid": v(-37.73, -33.66) * mm, "end": v(-37.99, -33.4) * mm});
            skLineSegment(sketch, "E636", {"start": v(-45.6, -33.91) * mm, "end": v(-44.72, -33.91) * mm});
            skArc(sketch, "E637", {"start": v(-44.72, -33.91) * mm, "mid": v(-44.47, -33.66) * mm, "end": v(-44.72, -33.4) * mm});
            skLineSegment(sketch, "E638", {"start": v(-44.72, -33.4) * mm, "end": v(-45.6, -33.4) * mm});
            skArc(sketch, "E639", {"start": v(-45.6, -33.4) * mm, "mid": v(-45.86, -33.66) * mm, "end": v(-45.6, -33.91) * mm});
            skArc(sketch, "E640", {"start": v(-44.08, -32.72) * mm, "mid": v(-44, -32.64) * mm, "end": v(-44.08, -32.57) * mm});
            skArc(sketch, "E641", {"start": v(-44.08, -32.57) * mm, "mid": v(-44.32, -32.66) * mm, "end": v(-44.41, -32.9) * mm});
            skArc(sketch, "E642", {"start": v(-44.41, -32.9) * mm, "mid": v(-44.34, -32.97) * mm, "end": v(-44.26, -32.9) * mm});
            skArc(sketch, "E643", {"start": v(-44.26, -32.9) * mm, "mid": v(-44.21, -32.77) * mm, "end": v(-44.08, -32.72) * mm});
            skArc(sketch, "E644", {"start": v(-44.26, -34.42) * mm, "mid": v(-44.34, -34.34) * mm, "end": v(-44.41, -34.42) * mm});
            skArc(sketch, "E645", {"start": v(-44.41, -34.42) * mm, "mid": v(-44.32, -34.65) * mm, "end": v(-44.08, -34.75) * mm});
            skArc(sketch, "E646", {"start": v(-44.08, -34.75) * mm, "mid": v(-44, -34.67) * mm, "end": v(-44.08, -34.6) * mm});
            skArc(sketch, "E647", {"start": v(-44.08, -34.6) * mm, "mid": v(-44.21, -34.55) * mm, "end": v(-44.26, -34.42) * mm});
            skArc(sketch, "E648", {"start": v(-39.51, -34.6) * mm, "mid": v(-39.59, -34.67) * mm, "end": v(-39.51, -34.75) * mm});
            skArc(sketch, "E649", {"start": v(-39.51, -34.75) * mm, "mid": v(-39.28, -34.65) * mm, "end": v(-39.18, -34.42) * mm});
            skArc(sketch, "E650", {"start": v(-39.18, -34.42) * mm, "mid": v(-39.26, -34.34) * mm, "end": v(-39.33, -34.42) * mm});
            skArc(sketch, "E651", {"start": v(-39.33, -34.42) * mm, "mid": v(-39.39, -34.55) * mm, "end": v(-39.51, -34.6) * mm});
            skArc(sketch, "E652", {"start": v(-39.33, -32.9) * mm, "mid": v(-39.26, -32.97) * mm, "end": v(-39.18, -32.9) * mm});
            skArc(sketch, "E653", {"start": v(-39.18, -32.9) * mm, "mid": v(-39.28, -32.66) * mm, "end": v(-39.51, -32.57) * mm});
            skArc(sketch, "E654", {"start": v(-39.51, -32.57) * mm, "mid": v(-39.59, -32.64) * mm, "end": v(-39.51, -32.72) * mm});
            skArc(sketch, "E655", {"start": v(-39.51, -32.72) * mm, "mid": v(-39.39, -32.77) * mm, "end": v(-39.33, -32.9) * mm});
            skLineSegment(sketch, "E656", {"start": v(-44.26, -34.42) * mm, "end": v(-44.26, -32.9) * mm});
            skArc(sketch, "E657", {"start": v(-44.26, -32.9) * mm, "mid": v(-44.34, -32.82) * mm, "end": v(-44.41, -32.9) * mm});
            skLineSegment(sketch, "E658", {"start": v(-44.41, -32.9) * mm, "end": v(-44.41, -34.42) * mm});
            skArc(sketch, "E659", {"start": v(-44.41, -34.42) * mm, "mid": v(-44.34, -34.5) * mm, "end": v(-44.26, -34.42) * mm});
            skLineSegment(sketch, "E660", {"start": v(-44.08, -32.72) * mm, "end": v(-43.7, -32.72) * mm});
            skArc(sketch, "E661", {"start": v(-43.7, -32.72) * mm, "mid": v(-43.63, -32.64) * mm, "end": v(-43.7, -32.57) * mm});
            skLineSegment(sketch, "E662", {"start": v(-43.7, -32.57) * mm, "end": v(-44.08, -32.57) * mm});
            skArc(sketch, "E663", {"start": v(-44.08, -32.57) * mm, "mid": v(-44.16, -32.64) * mm, "end": v(-44.08, -32.72) * mm});
            skLineSegment(sketch, "E664", {"start": v(-43.52, -32.72) * mm, "end": v(-43.65, -32.59) * mm});
            skArc(sketch, "E665", {"start": v(-43.65, -32.59) * mm, "mid": v(-43.76, -32.59) * mm, "end": v(-43.76, -32.7) * mm});
            skLineSegment(sketch, "E666", {"start": v(-43.76, -32.7) * mm, "end": v(-43.63, -32.82) * mm});
            skArc(sketch, "E667", {"start": v(-43.63, -32.82) * mm, "mid": v(-43.52, -32.82) * mm, "end": v(-43.52, -32.72) * mm});
            skLineSegment(sketch, "E668", {"start": v(-44.08, -34.75) * mm, "end": v(-43.7, -34.75) * mm});
            skArc(sketch, "E669", {"start": v(-43.7, -34.75) * mm, "mid": v(-43.63, -34.67) * mm, "end": v(-43.7, -34.6) * mm});
            skLineSegment(sketch, "E670", {"start": v(-43.7, -34.6) * mm, "end": v(-44.08, -34.6) * mm});
            skArc(sketch, "E671", {"start": v(-44.08, -34.6) * mm, "mid": v(-44.16, -34.67) * mm, "end": v(-44.08, -34.75) * mm});
            skLineSegment(sketch, "E672", {"start": v(-43.63, -34.5) * mm, "end": v(-43.76, -34.62) * mm});
            skArc(sketch, "E673", {"start": v(-43.76, -34.62) * mm, "mid": v(-43.76, -34.73) * mm, "end": v(-43.65, -34.73) * mm});
            skLineSegment(sketch, "E674", {"start": v(-43.65, -34.73) * mm, "end": v(-43.52, -34.6) * mm});
            skArc(sketch, "E675", {"start": v(-43.52, -34.6) * mm, "mid": v(-43.52, -34.5) * mm, "end": v(-43.63, -34.5) * mm});
            skLineSegment(sketch, "E676", {"start": v(-39.97, -32.82) * mm, "end": v(-39.84, -32.7) * mm});
            skArc(sketch, "E677", {"start": v(-39.84, -32.7) * mm, "mid": v(-39.84, -32.59) * mm, "end": v(-39.95, -32.59) * mm});
            skLineSegment(sketch, "E678", {"start": v(-39.95, -32.59) * mm, "end": v(-40.07, -32.72) * mm});
            skArc(sketch, "E679", {"start": v(-40.07, -32.72) * mm, "mid": v(-40.07, -32.82) * mm, "end": v(-39.97, -32.82) * mm});
            skLineSegment(sketch, "E680", {"start": v(-40.02, -32.7) * mm, "end": v(-43.58, -32.7) * mm});
            skArc(sketch, "E681", {"start": v(-43.58, -32.7) * mm, "mid": v(-43.65, -32.77) * mm, "end": v(-43.58, -32.85) * mm});
            skLineSegment(sketch, "E682", {"start": v(-43.58, -32.85) * mm, "end": v(-40.02, -32.85) * mm});
            skArc(sketch, "E683", {"start": v(-40.02, -32.85) * mm, "mid": v(-39.94, -32.77) * mm, "end": v(-40.02, -32.7) * mm});
            skLineSegment(sketch, "E684", {"start": v(-40.07, -34.6) * mm, "end": v(-39.95, -34.73) * mm});
            skArc(sketch, "E685", {"start": v(-39.95, -34.73) * mm, "mid": v(-39.84, -34.73) * mm, "end": v(-39.84, -34.62) * mm});
            skLineSegment(sketch, "E686", {"start": v(-39.84, -34.62) * mm, "end": v(-39.97, -34.5) * mm});
            skArc(sketch, "E687", {"start": v(-39.97, -34.5) * mm, "mid": v(-40.07, -34.5) * mm, "end": v(-40.07, -34.6) * mm});
            skLineSegment(sketch, "E688", {"start": v(-40.02, -34.47) * mm, "end": v(-43.58, -34.47) * mm});
            skArc(sketch, "E689", {"start": v(-43.58, -34.47) * mm, "mid": v(-43.65, -34.55) * mm, "end": v(-43.58, -34.62) * mm});
            skLineSegment(sketch, "E690", {"start": v(-43.58, -34.62) * mm, "end": v(-40.02, -34.62) * mm});
            skArc(sketch, "E691", {"start": v(-40.02, -34.62) * mm, "mid": v(-39.94, -34.55) * mm, "end": v(-40.02, -34.47) * mm});
            skLineSegment(sketch, "E692", {"start": v(-39.51, -32.57) * mm, "end": v(-39.9, -32.57) * mm});
            skArc(sketch, "E693", {"start": v(-39.9, -32.57) * mm, "mid": v(-39.97, -32.64) * mm, "end": v(-39.9, -32.72) * mm});
            skLineSegment(sketch, "E694", {"start": v(-39.9, -32.72) * mm, "end": v(-39.51, -32.72) * mm});
            skArc(sketch, "E695", {"start": v(-39.51, -32.72) * mm, "mid": v(-39.44, -32.64) * mm, "end": v(-39.51, -32.57) * mm});
            skLineSegment(sketch, "E696", {"start": v(-39.51, -34.6) * mm, "end": v(-39.9, -34.6) * mm});
            skArc(sketch, "E697", {"start": v(-39.9, -34.6) * mm, "mid": v(-39.97, -34.67) * mm, "end": v(-39.9, -34.75) * mm});
            skLineSegment(sketch, "E698", {"start": v(-39.9, -34.75) * mm, "end": v(-39.51, -34.75) * mm});
            skArc(sketch, "E699", {"start": v(-39.51, -34.75) * mm, "mid": v(-39.44, -34.67) * mm, "end": v(-39.51, -34.6) * mm});
            skLineSegment(sketch, "E700", {"start": v(-39.18, -34.42) * mm, "end": v(-39.18, -32.9) * mm});
            skArc(sketch, "E701", {"start": v(-39.18, -32.9) * mm, "mid": v(-39.26, -32.82) * mm, "end": v(-39.33, -32.9) * mm});
            skLineSegment(sketch, "E702", {"start": v(-39.33, -32.9) * mm, "end": v(-39.33, -34.42) * mm});
            skArc(sketch, "E703", {"start": v(-39.33, -34.42) * mm, "mid": v(-39.26, -34.5) * mm, "end": v(-39.18, -34.42) * mm});
            skLineSegment(sketch, "E704", {"start": v(-46.27, -33.93) * mm, "end": v(-46.27, -33.38) * mm});
            skLineSegment(sketch, "E705", {"start": v(-46.27, -33.38) * mm, "end": v(-45.88, -33) * mm});
            skLineSegment(sketch, "E706", {"start": v(-45.88, -33) * mm, "end": v(-45.33, -33) * mm});
            skLineSegment(sketch, "E707", {"start": v(-45.33, -33) * mm, "end": v(-44.95, -33.38) * mm});
            skLineSegment(sketch, "E708", {"start": v(-44.95, -33.38) * mm, "end": v(-44.95, -33.93) * mm});
            skLineSegment(sketch, "E709", {"start": v(-44.95, -33.93) * mm, "end": v(-45.33, -34.32) * mm});
            skLineSegment(sketch, "E710", {"start": v(-45.33, -34.32) * mm, "end": v(-45.88, -34.32) * mm});
            skLineSegment(sketch, "E711", {"start": v(-45.88, -34.32) * mm, "end": v(-46.27, -33.93) * mm});
            skLineSegment(sketch, "E712", {"start": v(-38.65, -33.93) * mm, "end": v(-38.65, -33.38) * mm});
            skLineSegment(sketch, "E713", {"start": v(-38.65, -33.38) * mm, "end": v(-38.26, -33) * mm});
            skLineSegment(sketch, "E714", {"start": v(-38.26, -33) * mm, "end": v(-37.71, -33) * mm});
            skLineSegment(sketch, "E715", {"start": v(-37.71, -33) * mm, "end": v(-37.33, -33.38) * mm});
            skLineSegment(sketch, "E716", {"start": v(-37.33, -33.38) * mm, "end": v(-37.33, -33.93) * mm});
            skLineSegment(sketch, "E717", {"start": v(-37.33, -33.93) * mm, "end": v(-37.71, -34.32) * mm});
            skLineSegment(sketch, "E718", {"start": v(-37.71, -34.32) * mm, "end": v(-38.26, -34.32) * mm});
            skLineSegment(sketch, "E719", {"start": v(-38.26, -34.32) * mm, "end": v(-38.65, -33.93) * mm});
            skLineSegment(sketch, "E720", {"start": v(-59.07, -16.78) * mm, "end": v(-70.25, -16.78) * mm});
            skArc(sketch, "E721", {"start": v(-70.25, -16.78) * mm, "mid": v(-70.35, -16.88) * mm, "end": v(-70.25, -16.98) * mm});
            skLineSegment(sketch, "E722", {"start": v(-70.25, -16.98) * mm, "end": v(-59.07, -16.98) * mm});
            skArc(sketch, "E723", {"start": v(-59.07, -16.98) * mm, "mid": v(-58.97, -16.88) * mm, "end": v(-59.07, -16.78) * mm});
            skLineSegment(sketch, "E724", {"start": v(-59.83, -42.18) * mm, "end": v(-69.48, -42.18) * mm});
            skArc(sketch, "E725", {"start": v(-69.48, -42.18) * mm, "mid": v(-69.59, -42.28) * mm, "end": v(-69.48, -42.38) * mm});
            skLineSegment(sketch, "E726", {"start": v(-69.48, -42.38) * mm, "end": v(-59.83, -42.38) * mm});
            skArc(sketch, "E727", {"start": v(-59.83, -42.38) * mm, "mid": v(-59.73, -42.28) * mm, "end": v(-59.83, -42.18) * mm});
            skLineSegment(sketch, "E728", {"start": v(-59.73, -42.28) * mm, "end": v(-59.73, -39.74) * mm});
            skArc(sketch, "E729", {"start": v(-59.73, -39.74) * mm, "mid": v(-59.83, -39.64) * mm, "end": v(-59.93, -39.74) * mm});
            skLineSegment(sketch, "E730", {"start": v(-59.93, -39.74) * mm, "end": v(-59.93, -42.28) * mm});
            skArc(sketch, "E731", {"start": v(-59.93, -42.28) * mm, "mid": v(-59.83, -42.38) * mm, "end": v(-59.73, -42.28) * mm});
            skLineSegment(sketch, "E732", {"start": v(-69.38, -42.28) * mm, "end": v(-69.38, -39.74) * mm});
            skArc(sketch, "E733", {"start": v(-69.38, -39.74) * mm, "mid": v(-69.48, -39.64) * mm, "end": v(-69.59, -39.74) * mm});
            skLineSegment(sketch, "E734", {"start": v(-69.59, -39.74) * mm, "end": v(-69.59, -42.28) * mm});
            skArc(sketch, "E735", {"start": v(-69.59, -42.28) * mm, "mid": v(-69.48, -42.38) * mm, "end": v(-69.38, -42.28) * mm});
            skLineSegment(sketch, "E736", {"start": v(-59.83, -39.84) * mm, "end": v(-57.04, -39.84) * mm});
            skArc(sketch, "E737", {"start": v(-57.04, -39.84) * mm, "mid": v(-56.94, -39.74) * mm, "end": v(-57.04, -39.64) * mm});
            skLineSegment(sketch, "E738", {"start": v(-57.04, -39.64) * mm, "end": v(-59.83, -39.64) * mm});
            skArc(sketch, "E739", {"start": v(-59.83, -39.64) * mm, "mid": v(-59.93, -39.74) * mm, "end": v(-59.83, -39.84) * mm});
            skLineSegment(sketch, "E740", {"start": v(-69.48, -39.64) * mm, "end": v(-72.28, -39.64) * mm});
            skArc(sketch, "E741", {"start": v(-72.28, -39.64) * mm, "mid": v(-72.38, -39.74) * mm, "end": v(-72.28, -39.84) * mm});
            skLineSegment(sketch, "E742", {"start": v(-72.28, -39.84) * mm, "end": v(-69.48, -39.84) * mm});
            skArc(sketch, "E743", {"start": v(-69.48, -39.84) * mm, "mid": v(-69.38, -39.74) * mm, "end": v(-69.48, -39.64) * mm});
            skLineSegment(sketch, "E744", {"start": v(-55.23, -26.78) * mm, "end": v(-55.23, -34.91) * mm});
            skArc(sketch, "E745", {"start": v(-55.23, -34.91) * mm, "mid": v(-55.13, -35.01) * mm, "end": v(-55.03, -34.91) * mm});
            skLineSegment(sketch, "E746", {"start": v(-55.03, -34.91) * mm, "end": v(-55.03, -26.78) * mm});
            skArc(sketch, "E747", {"start": v(-55.03, -26.78) * mm, "mid": v(-55.13, -26.68) * mm, "end": v(-55.23, -26.78) * mm});
            skLineSegment(sketch, "E748", {"start": v(-56.94, -26.78) * mm, "end": v(-56.94, -23.86) * mm});
            skArc(sketch, "E749", {"start": v(-56.94, -23.86) * mm, "mid": v(-57.04, -23.76) * mm, "end": v(-57.14, -23.86) * mm});
            skLineSegment(sketch, "E750", {"start": v(-57.14, -23.86) * mm, "end": v(-57.14, -26.78) * mm});
            skArc(sketch, "E751", {"start": v(-57.14, -26.78) * mm, "mid": v(-57.04, -26.89) * mm, "end": v(-56.94, -26.78) * mm});
            skLineSegment(sketch, "E752", {"start": v(-57.14, -34.91) * mm, "end": v(-57.14, -39.74) * mm});
            skArc(sketch, "E753", {"start": v(-57.14, -39.74) * mm, "mid": v(-57.04, -39.84) * mm, "end": v(-56.94, -39.74) * mm});
            skLineSegment(sketch, "E754", {"start": v(-56.94, -39.74) * mm, "end": v(-56.94, -34.91) * mm});
            skArc(sketch, "E755", {"start": v(-56.94, -34.91) * mm, "mid": v(-57.04, -34.81) * mm, "end": v(-57.14, -34.91) * mm});
            skLineSegment(sketch, "E756", {"start": v(-57.04, -26.89) * mm, "end": v(-55.13, -26.89) * mm});
            skArc(sketch, "E757", {"start": v(-55.13, -26.89) * mm, "mid": v(-55.03, -26.78) * mm, "end": v(-55.13, -26.68) * mm});
            skLineSegment(sketch, "E758", {"start": v(-55.13, -26.68) * mm, "end": v(-57.04, -26.68) * mm});
            skArc(sketch, "E759", {"start": v(-57.04, -26.68) * mm, "mid": v(-57.14, -26.78) * mm, "end": v(-57.04, -26.89) * mm});
            skLineSegment(sketch, "E760", {"start": v(-57.04, -35.01) * mm, "end": v(-55.13, -35.01) * mm});
            skArc(sketch, "E761", {"start": v(-55.13, -35.01) * mm, "mid": v(-55.03, -34.91) * mm, "end": v(-55.13, -34.81) * mm});
            skLineSegment(sketch, "E762", {"start": v(-55.13, -34.81) * mm, "end": v(-57.04, -34.81) * mm});
            skArc(sketch, "E763", {"start": v(-57.04, -34.81) * mm, "mid": v(-57.14, -34.91) * mm, "end": v(-57.04, -35.01) * mm});
            skLineSegment(sketch, "E764", {"start": v(-57.04, -23.76) * mm, "end": v(-59.07, -23.76) * mm});
            skArc(sketch, "E765", {"start": v(-59.07, -23.76) * mm, "mid": v(-59.17, -23.86) * mm, "end": v(-59.07, -23.97) * mm});
            skLineSegment(sketch, "E766", {"start": v(-59.07, -23.97) * mm, "end": v(-57.04, -23.97) * mm});
            skArc(sketch, "E767", {"start": v(-57.04, -23.97) * mm, "mid": v(-56.94, -23.86) * mm, "end": v(-57.04, -23.76) * mm});
            skLineSegment(sketch, "E768", {"start": v(-70.25, -23.76) * mm, "end": v(-72.28, -23.76) * mm});
            skArc(sketch, "E769", {"start": v(-72.28, -23.76) * mm, "mid": v(-72.38, -23.86) * mm, "end": v(-72.28, -23.97) * mm});
            skLineSegment(sketch, "E770", {"start": v(-72.28, -23.97) * mm, "end": v(-70.25, -23.97) * mm});
            skArc(sketch, "E771", {"start": v(-70.25, -23.97) * mm, "mid": v(-70.14, -23.86) * mm, "end": v(-70.25, -23.76) * mm});
            skLineSegment(sketch, "E772", {"start": v(-59.17, -16.88) * mm, "end": v(-59.17, -23.86) * mm});
            skArc(sketch, "E773", {"start": v(-59.17, -23.86) * mm, "mid": v(-59.07, -23.97) * mm, "end": v(-58.97, -23.86) * mm});
            skLineSegment(sketch, "E774", {"start": v(-58.97, -23.86) * mm, "end": v(-58.97, -16.88) * mm});
            skArc(sketch, "E775", {"start": v(-58.97, -16.88) * mm, "mid": v(-59.07, -16.78) * mm, "end": v(-59.17, -16.88) * mm});
            skLineSegment(sketch, "E776", {"start": v(-70.35, -16.88) * mm, "end": v(-70.35, -23.86) * mm});
            skArc(sketch, "E777", {"start": v(-70.35, -23.86) * mm, "mid": v(-70.25, -23.97) * mm, "end": v(-70.14, -23.86) * mm});
            skLineSegment(sketch, "E778", {"start": v(-70.14, -23.86) * mm, "end": v(-70.14, -16.88) * mm});
            skArc(sketch, "E779", {"start": v(-70.14, -16.88) * mm, "mid": v(-70.25, -16.78) * mm, "end": v(-70.35, -16.88) * mm});
            skLineSegment(sketch, "E780", {"start": v(-72.28, -25.92) * mm, "end": v(-75.83, -25.92) * mm});
            skArc(sketch, "E781", {"start": v(-75.83, -25.92) * mm, "mid": v(-75.94, -26.02) * mm, "end": v(-75.83, -26.12) * mm});
            skLineSegment(sketch, "E782", {"start": v(-75.83, -26.12) * mm, "end": v(-72.28, -26.12) * mm});
            skArc(sketch, "E783", {"start": v(-72.28, -26.12) * mm, "mid": v(-72.18, -26.02) * mm, "end": v(-72.28, -25.92) * mm});
            skLineSegment(sketch, "E784", {"start": v(-72.28, -35.57) * mm, "end": v(-75.83, -35.57) * mm});
            skArc(sketch, "E785", {"start": v(-75.83, -35.57) * mm, "mid": v(-75.94, -35.67) * mm, "end": v(-75.83, -35.78) * mm});
            skLineSegment(sketch, "E786", {"start": v(-75.83, -35.78) * mm, "end": v(-72.28, -35.78) * mm});
            skArc(sketch, "E787", {"start": v(-72.28, -35.78) * mm, "mid": v(-72.18, -35.67) * mm, "end": v(-72.28, -35.57) * mm});
            skLineSegment(sketch, "E788", {"start": v(-75.94, -26.02) * mm, "end": v(-75.94, -35.67) * mm});
            skArc(sketch, "E789", {"start": v(-75.94, -35.67) * mm, "mid": v(-75.83, -35.78) * mm, "end": v(-75.73, -35.67) * mm});
            skLineSegment(sketch, "E790", {"start": v(-75.73, -35.67) * mm, "end": v(-75.73, -26.02) * mm});
            skArc(sketch, "E791", {"start": v(-75.73, -26.02) * mm, "mid": v(-75.83, -25.92) * mm, "end": v(-75.94, -26.02) * mm});
            skLineSegment(sketch, "E792", {"start": v(-72.18, -26.02) * mm, "end": v(-72.18, -23.86) * mm});
            skArc(sketch, "E793", {"start": v(-72.18, -23.86) * mm, "mid": v(-72.28, -23.76) * mm, "end": v(-72.38, -23.86) * mm});
            skLineSegment(sketch, "E794", {"start": v(-72.38, -23.86) * mm, "end": v(-72.38, -26.02) * mm});
            skArc(sketch, "E795", {"start": v(-72.38, -26.02) * mm, "mid": v(-72.28, -26.12) * mm, "end": v(-72.18, -26.02) * mm});
            skLineSegment(sketch, "E796", {"start": v(-72.38, -35.67) * mm, "end": v(-72.38, -39.74) * mm});
            skArc(sketch, "E797", {"start": v(-72.38, -39.74) * mm, "mid": v(-72.28, -39.84) * mm, "end": v(-72.18, -39.74) * mm});
            skLineSegment(sketch, "E798", {"start": v(-72.18, -39.74) * mm, "end": v(-72.18, -35.67) * mm});
            skArc(sketch, "E799", {"start": v(-72.18, -35.67) * mm, "mid": v(-72.28, -35.57) * mm, "end": v(-72.38, -35.67) * mm});
            skLineSegment(sketch, "E800", {"start": v(-66.56, -23.33) * mm, "end": v(-65.3, -23.33) * mm});
            skArc(sketch, "E801", {"start": v(-65.3, -23.33) * mm, "mid": v(-65.2, -23.23) * mm, "end": v(-65.3, -23.13) * mm});
            skLineSegment(sketch, "E802", {"start": v(-65.3, -23.13) * mm, "end": v(-66.56, -23.13) * mm});
            skArc(sketch, "E803", {"start": v(-66.56, -23.13) * mm, "mid": v(-66.67, -23.23) * mm, "end": v(-66.56, -23.33) * mm});
            skLineSegment(sketch, "E804", {"start": v(-65.25, -23.32) * mm, "end": v(-63.98, -22.68) * mm});
            skArc(sketch, "E805", {"start": v(-63.98, -22.68) * mm, "mid": v(-63.93, -22.55) * mm, "end": v(-64.07, -22.5) * mm});
            skLineSegment(sketch, "E806", {"start": v(-64.07, -22.5) * mm, "end": v(-65.34, -23.14) * mm});
            skArc(sketch, "E807", {"start": v(-65.34, -23.14) * mm, "mid": v(-65.38, -23.27) * mm, "end": v(-65.25, -23.32) * mm});
            skLineSegment(sketch, "E808", {"start": v(-64.02, -23.33) * mm, "end": v(-62.75, -23.33) * mm});
            skArc(sketch, "E809", {"start": v(-62.75, -23.33) * mm, "mid": v(-62.65, -23.23) * mm, "end": v(-62.75, -23.13) * mm});
            skLineSegment(sketch, "E810", {"start": v(-62.75, -23.13) * mm, "end": v(-64.02, -23.13) * mm});
            skArc(sketch, "E811", {"start": v(-64.02, -23.13) * mm, "mid": v(-64.12, -23.23) * mm, "end": v(-64.02, -23.33) * mm});
            skCircle(sketch, "E812", {"center": v(-64.66, -30.85) * mm, "radius": 0.53 * mm});
            skCircle(sketch, "E813", {"center": v(-64.66, -30.85) * mm, "radius": 0.74 * mm});
            skCircle(sketch, "E814", {"center": v(-64.66, -30.85) * mm, "radius": 12.6 * mm});
            skCircle(sketch, "E815", {"center": v(-64.66, -30.85) * mm, "radius": 12.8 * mm});
            skCircle(sketch, "E816", {"center": v(-67.83, -18.15) * mm, "radius": 0.5 * mm});
            skCircle(sketch, "E817", {"center": v(-61.48, -18.15) * mm, "radius": 0.5 * mm});
            skCircle(sketch, "E818", {"center": v(-67.83, -23.23) * mm, "radius": 0.5 * mm});
            skCircle(sketch, "E819", {"center": v(-61.48, -23.23) * mm, "radius": 0.5 * mm});
            skCircle(sketch, "E820", {"center": v(-67.2, -41) * mm, "radius": 0.5 * mm});
            skCircle(sketch, "E821", {"center": v(-64.66, -41) * mm, "radius": 0.5 * mm});
            skCircle(sketch, "E822", {"center": v(-62.12, -41) * mm, "radius": 0.5 * mm});
            skCircle(sketch, "E823", {"center": v(-72.28, -24.18) * mm, "radius": 0.5 * mm});
            skCircle(sketch, "E824", {"center": v(-72.28, -37.52) * mm, "radius": 0.5 * mm});
            skCircle(sketch, "E825", {"center": v(-57.04, -37.52) * mm, "radius": 0.5 * mm});
            skCircle(sketch, "E826", {"center": v(-57.04, -24.18) * mm, "radius": 0.5 * mm});
            skCircle(sketch, "E827", {"center": v(-74.82, -28.3) * mm, "radius": 0.5 * mm});
            skCircle(sketch, "E828", {"center": v(-74.82, -30.85) * mm, "radius": 0.5 * mm});
            skCircle(sketch, "E829", {"center": v(-74.82, -33.39) * mm, "radius": 0.5 * mm});
            skLineSegment(sketch, "E830", {"start": v(-43.7, -15.32) * mm, "end": v(-39.9, -15.32) * mm});
            skArc(sketch, "E831", {"start": v(-39.9, -15.32) * mm, "mid": v(-39.82, -15.24) * mm, "end": v(-39.9, -15.17) * mm});
            skLineSegment(sketch, "E832", {"start": v(-39.9, -15.17) * mm, "end": v(-43.7, -15.17) * mm});
            skArc(sketch, "E833", {"start": v(-43.7, -15.17) * mm, "mid": v(-43.78, -15.24) * mm, "end": v(-43.7, -15.32) * mm});
            skLineSegment(sketch, "E834", {"start": v(-39.82, -19.05) * mm, "end": v(-39.82, -15.24) * mm});
            skArc(sketch, "E835", {"start": v(-39.82, -15.24) * mm, "mid": v(-39.9, -15.17) * mm, "end": v(-39.97, -15.24) * mm});
            skLineSegment(sketch, "E836", {"start": v(-39.97, -15.24) * mm, "end": v(-39.97, -19.05) * mm});
            skArc(sketch, "E837", {"start": v(-39.97, -19.05) * mm, "mid": v(-39.9, -19.13) * mm, "end": v(-39.82, -19.05) * mm});
            skLineSegment(sketch, "E838", {"start": v(-39.9, -18.98) * mm, "end": v(-43.7, -18.98) * mm});
            skArc(sketch, "E839", {"start": v(-43.7, -18.98) * mm, "mid": v(-43.78, -19.05) * mm, "end": v(-43.7, -19.13) * mm});
            skLineSegment(sketch, "E840", {"start": v(-43.7, -19.13) * mm, "end": v(-39.9, -19.13) * mm});
            skArc(sketch, "E841", {"start": v(-39.9, -19.13) * mm, "mid": v(-39.82, -19.05) * mm, "end": v(-39.9, -18.98) * mm});
            skLineSegment(sketch, "E842", {"start": v(-43.78, -15.24) * mm, "end": v(-43.78, -19.05) * mm});
            skArc(sketch, "E843", {"start": v(-43.78, -19.05) * mm, "mid": v(-43.7, -19.13) * mm, "end": v(-43.63, -19.05) * mm});
            skLineSegment(sketch, "E844", {"start": v(-43.63, -19.05) * mm, "end": v(-43.63, -15.24) * mm});
            skArc(sketch, "E845", {"start": v(-43.63, -15.24) * mm, "mid": v(-43.7, -15.17) * mm, "end": v(-43.78, -15.24) * mm});
            skLineSegment(sketch, "E846", {"start": v(-43.45, -15.52) * mm, "end": v(-40.15, -15.52) * mm});
            skArc(sketch, "E847", {"start": v(-40.15, -15.52) * mm, "mid": v(-40.12, -15.5) * mm, "end": v(-40.15, -15.47) * mm});
            skLineSegment(sketch, "E848", {"start": v(-40.15, -15.47) * mm, "end": v(-43.45, -15.47) * mm});
            skArc(sketch, "E849", {"start": v(-43.45, -15.47) * mm, "mid": v(-43.47, -15.5) * mm, "end": v(-43.45, -15.52) * mm});
            skLineSegment(sketch, "E850", {"start": v(-40.12, -18.8) * mm, "end": v(-40.12, -15.5) * mm});
            skArc(sketch, "E851", {"start": v(-40.12, -15.5) * mm, "mid": v(-40.15, -15.47) * mm, "end": v(-40.17, -15.5) * mm});
            skLineSegment(sketch, "E852", {"start": v(-40.17, -15.5) * mm, "end": v(-40.17, -18.8) * mm});
            skArc(sketch, "E853", {"start": v(-40.17, -18.8) * mm, "mid": v(-40.15, -18.82) * mm, "end": v(-40.12, -18.8) * mm});
            skLineSegment(sketch, "E854", {"start": v(-40.15, -18.77) * mm, "end": v(-43.45, -18.77) * mm});
            skArc(sketch, "E855", {"start": v(-43.45, -18.77) * mm, "mid": v(-43.47, -18.8) * mm, "end": v(-43.45, -18.82) * mm});
            skLineSegment(sketch, "E856", {"start": v(-43.45, -18.82) * mm, "end": v(-40.15, -18.82) * mm});
            skArc(sketch, "E857", {"start": v(-40.15, -18.82) * mm, "mid": v(-40.12, -18.8) * mm, "end": v(-40.15, -18.77) * mm});
            skLineSegment(sketch, "E858", {"start": v(-43.47, -15.5) * mm, "end": v(-43.47, -18.8) * mm});
            skArc(sketch, "E859", {"start": v(-43.47, -18.8) * mm, "mid": v(-43.45, -18.82) * mm, "end": v(-43.42, -18.8) * mm});
            skLineSegment(sketch, "E860", {"start": v(-43.42, -18.8) * mm, "end": v(-43.42, -15.5) * mm});
            skArc(sketch, "E861", {"start": v(-43.42, -15.5) * mm, "mid": v(-43.45, -15.47) * mm, "end": v(-43.47, -15.5) * mm});
            skLineSegment(sketch, "E862", {"start": v(-42.74, -11.05) * mm, "end": v(-42.74, -10.67) * mm});
            skArc(sketch, "E863", {"start": v(-42.74, -10.67) * mm, "mid": v(-42.81, -10.6) * mm, "end": v(-42.9, -10.67) * mm});
            skLineSegment(sketch, "E864", {"start": v(-42.9, -10.67) * mm, "end": v(-42.9, -11.05) * mm});
            skArc(sketch, "E865", {"start": v(-42.9, -11.05) * mm, "mid": v(-42.81, -11.13) * mm, "end": v(-42.74, -11.05) * mm});
            skLineSegment(sketch, "E866", {"start": v(-42.81, -11.13) * mm, "end": v(-40.78, -11.13) * mm});
            skArc(sketch, "E867", {"start": v(-40.78, -11.13) * mm, "mid": v(-40.7, -11.05) * mm, "end": v(-40.78, -10.98) * mm});
            skLineSegment(sketch, "E868", {"start": v(-40.78, -10.98) * mm, "end": v(-42.81, -10.98) * mm});
            skArc(sketch, "E869", {"start": v(-42.81, -10.98) * mm, "mid": v(-42.9, -11.05) * mm, "end": v(-42.81, -11.13) * mm});
            skLineSegment(sketch, "E870", {"start": v(-42.81, -10.75) * mm, "end": v(-40.78, -10.75) * mm});
            skArc(sketch, "E871", {"start": v(-40.78, -10.75) * mm, "mid": v(-40.7, -10.67) * mm, "end": v(-40.78, -10.6) * mm});
            skLineSegment(sketch, "E872", {"start": v(-40.78, -10.6) * mm, "end": v(-42.81, -10.6) * mm});
            skArc(sketch, "E873", {"start": v(-42.81, -10.6) * mm, "mid": v(-42.9, -10.67) * mm, "end": v(-42.81, -10.75) * mm});
            skLineSegment(sketch, "E874", {"start": v(-40.86, -10.67) * mm, "end": v(-40.86, -11.05) * mm});
            skArc(sketch, "E875", {"start": v(-40.86, -11.05) * mm, "mid": v(-40.78, -11.13) * mm, "end": v(-40.7, -11.05) * mm});
            skLineSegment(sketch, "E876", {"start": v(-40.7, -11.05) * mm, "end": v(-40.7, -10.67) * mm});
            skArc(sketch, "E877", {"start": v(-40.7, -10.67) * mm, "mid": v(-40.78, -10.6) * mm, "end": v(-40.86, -10.67) * mm});
            skLineSegment(sketch, "E878", {"start": v(-35.65, -12.01) * mm, "end": v(-36.66, -11) * mm});
            skArc(sketch, "E879", {"start": v(-36.66, -11) * mm, "mid": v(-36.77, -11) * mm, "end": v(-36.77, -11.1) * mm});
            skLineSegment(sketch, "E880", {"start": v(-36.77, -11.1) * mm, "end": v(-35.76, -12.12) * mm});
            skArc(sketch, "E881", {"start": v(-35.76, -12.12) * mm, "mid": v(-35.65, -12.12) * mm, "end": v(-35.65, -12.01) * mm});
            skLineSegment(sketch, "E882", {"start": v(-36.72, -10.98) * mm, "end": v(-40.02, -10.98) * mm});
            skArc(sketch, "E883", {"start": v(-40.02, -10.98) * mm, "mid": v(-40.1, -11.05) * mm, "end": v(-40.02, -11.13) * mm});
            skLineSegment(sketch, "E884", {"start": v(-40.02, -11.13) * mm, "end": v(-36.72, -11.13) * mm});
            skArc(sketch, "E885", {"start": v(-36.72, -11.13) * mm, "mid": v(-36.64, -11.05) * mm, "end": v(-36.72, -10.98) * mm});
            skLineSegment(sketch, "E886", {"start": v(-35.78, -12.07) * mm, "end": v(-35.78, -13.34) * mm});
            skArc(sketch, "E887", {"start": v(-35.78, -13.34) * mm, "mid": v(-35.7, -13.41) * mm, "end": v(-35.63, -13.34) * mm});
            skLineSegment(sketch, "E888", {"start": v(-35.63, -13.34) * mm, "end": v(-35.63, -12.07) * mm});
            skArc(sketch, "E889", {"start": v(-35.63, -12.07) * mm, "mid": v(-35.7, -12) * mm, "end": v(-35.78, -12.07) * mm});
            skLineSegment(sketch, "E890", {"start": v(-35.63, -16) * mm, "end": v(-35.63, -13.34) * mm});
            skArc(sketch, "E891", {"start": v(-35.63, -13.34) * mm, "mid": v(-35.7, -13.26) * mm, "end": v(-35.78, -13.34) * mm});
            skLineSegment(sketch, "E892", {"start": v(-35.78, -13.34) * mm, "end": v(-35.78, -16) * mm});
            skArc(sketch, "E893", {"start": v(-35.78, -16) * mm, "mid": v(-35.7, -16.08) * mm, "end": v(-35.63, -16) * mm});
            skLineSegment(sketch, "E894", {"start": v(-35.78, -16) * mm, "end": v(-35.78, -18.3) * mm});
            skArc(sketch, "E895", {"start": v(-35.78, -18.3) * mm, "mid": v(-35.7, -18.37) * mm, "end": v(-35.63, -18.3) * mm});
            skLineSegment(sketch, "E896", {"start": v(-35.63, -18.3) * mm, "end": v(-35.63, -16) * mm});
            skArc(sketch, "E897", {"start": v(-35.63, -16) * mm, "mid": v(-35.7, -15.93) * mm, "end": v(-35.78, -16) * mm});
            skLineSegment(sketch, "E898", {"start": v(-35.63, -20.96) * mm, "end": v(-35.63, -18.3) * mm});
            skArc(sketch, "E899", {"start": v(-35.63, -18.3) * mm, "mid": v(-35.7, -18.22) * mm, "end": v(-35.78, -18.3) * mm});
            skLineSegment(sketch, "E900", {"start": v(-35.78, -18.3) * mm, "end": v(-35.78, -20.96) * mm});
            skArc(sketch, "E901", {"start": v(-35.78, -20.96) * mm, "mid": v(-35.7, -21.03) * mm, "end": v(-35.63, -20.96) * mm});
            skLineSegment(sketch, "E902", {"start": v(-36.66, -23.3) * mm, "end": v(-35.65, -22.28) * mm});
            skArc(sketch, "E903", {"start": v(-35.65, -22.28) * mm, "mid": v(-35.65, -22.17) * mm, "end": v(-35.76, -22.17) * mm});
            skLineSegment(sketch, "E904", {"start": v(-35.76, -22.17) * mm, "end": v(-36.77, -23.2) * mm});
            skArc(sketch, "E905", {"start": v(-36.77, -23.2) * mm, "mid": v(-36.77, -23.3) * mm, "end": v(-36.66, -23.3) * mm});
            skLineSegment(sketch, "E906", {"start": v(-35.63, -22.23) * mm, "end": v(-35.63, -20.96) * mm});
            skArc(sketch, "E907", {"start": v(-35.63, -20.96) * mm, "mid": v(-35.7, -20.88) * mm, "end": v(-35.78, -20.96) * mm});
            skLineSegment(sketch, "E908", {"start": v(-35.78, -20.96) * mm, "end": v(-35.78, -22.23) * mm});
            skArc(sketch, "E909", {"start": v(-35.78, -22.23) * mm, "mid": v(-35.7, -22.3) * mm, "end": v(-35.63, -22.23) * mm});
            skLineSegment(sketch, "E910", {"start": v(-47.82, -16) * mm, "end": v(-47.82, -13.34) * mm});
            skArc(sketch, "E911", {"start": v(-47.82, -13.34) * mm, "mid": v(-47.9, -13.26) * mm, "end": v(-47.97, -13.34) * mm});
            skLineSegment(sketch, "E912", {"start": v(-47.97, -13.34) * mm, "end": v(-47.97, -16) * mm});
            skArc(sketch, "E913", {"start": v(-47.97, -16) * mm, "mid": v(-47.9, -16.08) * mm, "end": v(-47.82, -16) * mm});
            skLineSegment(sketch, "E914", {"start": v(-47.97, -16) * mm, "end": v(-47.97, -18.3) * mm});
            skArc(sketch, "E915", {"start": v(-47.97, -18.3) * mm, "mid": v(-47.9, -18.37) * mm, "end": v(-47.82, -18.3) * mm});
            skLineSegment(sketch, "E916", {"start": v(-47.82, -18.3) * mm, "end": v(-47.82, -16) * mm});
            skArc(sketch, "E917", {"start": v(-47.82, -16) * mm, "mid": v(-47.9, -15.93) * mm, "end": v(-47.97, -16) * mm});
            skLineSegment(sketch, "E918", {"start": v(-47.82, -20.96) * mm, "end": v(-47.82, -18.3) * mm});
            skArc(sketch, "E919", {"start": v(-47.82, -18.3) * mm, "mid": v(-47.9, -18.22) * mm, "end": v(-47.97, -18.3) * mm});
            skLineSegment(sketch, "E920", {"start": v(-47.97, -18.3) * mm, "end": v(-47.97, -20.96) * mm});
            skArc(sketch, "E921", {"start": v(-47.97, -20.96) * mm, "mid": v(-47.9, -21.03) * mm, "end": v(-47.82, -20.96) * mm});
            skLineSegment(sketch, "E922", {"start": v(-47.97, -20.96) * mm, "end": v(-47.97, -22.23) * mm});
            skArc(sketch, "E923", {"start": v(-47.97, -22.23) * mm, "mid": v(-47.9, -22.3) * mm, "end": v(-47.82, -22.23) * mm});
            skLineSegment(sketch, "E924", {"start": v(-47.82, -22.23) * mm, "end": v(-47.82, -20.96) * mm});
            skArc(sketch, "E925", {"start": v(-47.82, -20.96) * mm, "mid": v(-47.9, -20.88) * mm, "end": v(-47.97, -20.96) * mm});
            skLineSegment(sketch, "E926", {"start": v(-47.95, -22.28) * mm, "end": v(-46.93, -23.3) * mm});
            skArc(sketch, "E927", {"start": v(-46.93, -23.3) * mm, "mid": v(-46.82, -23.3) * mm, "end": v(-46.82, -23.2) * mm});
            skLineSegment(sketch, "E928", {"start": v(-46.82, -23.2) * mm, "end": v(-47.84, -22.17) * mm});
            skArc(sketch, "E929", {"start": v(-47.84, -22.17) * mm, "mid": v(-47.95, -22.17) * mm, "end": v(-47.95, -22.28) * mm});
            skLineSegment(sketch, "E930", {"start": v(-46.88, -23.32) * mm, "end": v(-43.58, -23.32) * mm});
            skArc(sketch, "E931", {"start": v(-43.58, -23.32) * mm, "mid": v(-43.5, -23.24) * mm, "end": v(-43.58, -23.17) * mm});
            skLineSegment(sketch, "E932", {"start": v(-43.58, -23.17) * mm, "end": v(-46.88, -23.17) * mm});
            skArc(sketch, "E933", {"start": v(-46.88, -23.17) * mm, "mid": v(-46.95, -23.24) * mm, "end": v(-46.88, -23.32) * mm});
            skLineSegment(sketch, "E934", {"start": v(-46.88, -11.13) * mm, "end": v(-43.58, -11.13) * mm});
            skArc(sketch, "E935", {"start": v(-43.58, -11.13) * mm, "mid": v(-43.5, -11.05) * mm, "end": v(-43.58, -10.98) * mm});
            skLineSegment(sketch, "E936", {"start": v(-43.58, -10.98) * mm, "end": v(-46.88, -10.98) * mm});
            skArc(sketch, "E937", {"start": v(-46.88, -10.98) * mm, "mid": v(-46.95, -11.05) * mm, "end": v(-46.88, -11.13) * mm});
            skLineSegment(sketch, "E938", {"start": v(-46.93, -11) * mm, "end": v(-47.95, -12.01) * mm});
            skArc(sketch, "E939", {"start": v(-47.95, -12.01) * mm, "mid": v(-47.95, -12.12) * mm, "end": v(-47.84, -12.12) * mm});
            skLineSegment(sketch, "E940", {"start": v(-47.84, -12.12) * mm, "end": v(-46.82, -11.1) * mm});
            skArc(sketch, "E941", {"start": v(-46.82, -11.1) * mm, "mid": v(-46.82, -11) * mm, "end": v(-46.93, -11) * mm});
            skLineSegment(sketch, "E942", {"start": v(-47.97, -12.07) * mm, "end": v(-47.97, -13.34) * mm});
            skArc(sketch, "E943", {"start": v(-47.97, -13.34) * mm, "mid": v(-47.9, -13.41) * mm, "end": v(-47.82, -13.34) * mm});
            skLineSegment(sketch, "E944", {"start": v(-47.82, -13.34) * mm, "end": v(-47.82, -12.07) * mm});
            skArc(sketch, "E945", {"start": v(-47.82, -12.07) * mm, "mid": v(-47.9, -12) * mm, "end": v(-47.97, -12.07) * mm});
            skLineSegment(sketch, "E946", {"start": v(-42.81, -23.7) * mm, "end": v(-40.78, -23.7) * mm});
            skArc(sketch, "E947", {"start": v(-40.78, -23.7) * mm, "mid": v(-40.7, -23.63) * mm, "end": v(-40.78, -23.55) * mm});
            skLineSegment(sketch, "E948", {"start": v(-40.78, -23.55) * mm, "end": v(-42.81, -23.55) * mm});
            skArc(sketch, "E949", {"start": v(-42.81, -23.55) * mm, "mid": v(-42.9, -23.63) * mm, "end": v(-42.81, -23.7) * mm});
            skLineSegment(sketch, "E950", {"start": v(-42.74, -23.63) * mm, "end": v(-42.74, -23.24) * mm});
            skArc(sketch, "E951", {"start": v(-42.74, -23.24) * mm, "mid": v(-42.81, -23.17) * mm, "end": v(-42.9, -23.24) * mm});
            skLineSegment(sketch, "E952", {"start": v(-42.9, -23.24) * mm, "end": v(-42.9, -23.63) * mm});
            skArc(sketch, "E953", {"start": v(-42.9, -23.63) * mm, "mid": v(-42.81, -23.7) * mm, "end": v(-42.74, -23.63) * mm});
            skLineSegment(sketch, "E954", {"start": v(-40.86, -23.24) * mm, "end": v(-40.86, -23.63) * mm});
            skArc(sketch, "E955", {"start": v(-40.86, -23.63) * mm, "mid": v(-40.78, -23.7) * mm, "end": v(-40.7, -23.63) * mm});
            skLineSegment(sketch, "E956", {"start": v(-40.7, -23.63) * mm, "end": v(-40.7, -23.24) * mm});
            skArc(sketch, "E957", {"start": v(-40.7, -23.24) * mm, "mid": v(-40.78, -23.17) * mm, "end": v(-40.86, -23.24) * mm});
            skLineSegment(sketch, "E958", {"start": v(-36.66, -11) * mm, "end": v(-36.92, -10.74) * mm});
            skArc(sketch, "E959", {"start": v(-36.92, -10.74) * mm, "mid": v(-37.03, -10.74) * mm, "end": v(-37.03, -10.85) * mm});
            skLineSegment(sketch, "E960", {"start": v(-37.03, -10.85) * mm, "end": v(-36.77, -11.1) * mm});
            skArc(sketch, "E961", {"start": v(-36.77, -11.1) * mm, "mid": v(-36.66, -11.1) * mm, "end": v(-36.66, -11) * mm});
            skLineSegment(sketch, "E962", {"start": v(-36.97, -10.72) * mm, "end": v(-40.02, -10.72) * mm});
            skArc(sketch, "E963", {"start": v(-40.02, -10.72) * mm, "mid": v(-40.1, -10.8) * mm, "end": v(-40.02, -10.87) * mm});
            skLineSegment(sketch, "E964", {"start": v(-40.02, -10.87) * mm, "end": v(-36.97, -10.87) * mm});
            skArc(sketch, "E965", {"start": v(-36.97, -10.87) * mm, "mid": v(-36.9, -10.8) * mm, "end": v(-36.97, -10.72) * mm});
            skLineSegment(sketch, "E966", {"start": v(-40.1, -10.8) * mm, "end": v(-40.1, -11.05) * mm});
            skArc(sketch, "E967", {"start": v(-40.1, -11.05) * mm, "mid": v(-40.02, -11.13) * mm, "end": v(-39.94, -11.05) * mm});
            skLineSegment(sketch, "E968", {"start": v(-39.94, -11.05) * mm, "end": v(-39.94, -10.8) * mm});
            skArc(sketch, "E969", {"start": v(-39.94, -10.8) * mm, "mid": v(-40.02, -10.72) * mm, "end": v(-40.1, -10.8) * mm});
            skLineSegment(sketch, "E970", {"start": v(-40.02, -10.98) * mm, "end": v(-40.78, -10.98) * mm});
            skArc(sketch, "E971", {"start": v(-40.78, -10.98) * mm, "mid": v(-40.86, -11.05) * mm, "end": v(-40.78, -11.13) * mm});
            skLineSegment(sketch, "E972", {"start": v(-40.78, -11.13) * mm, "end": v(-40.02, -11.13) * mm});
            skArc(sketch, "E973", {"start": v(-40.02, -11.13) * mm, "mid": v(-39.94, -11.05) * mm, "end": v(-40.02, -10.98) * mm});
            skLineSegment(sketch, "E974", {"start": v(-43.65, -10.8) * mm, "end": v(-43.65, -11.05) * mm});
            skArc(sketch, "E975", {"start": v(-43.65, -11.05) * mm, "mid": v(-43.58, -11.13) * mm, "end": v(-43.5, -11.05) * mm});
            skLineSegment(sketch, "E976", {"start": v(-43.5, -11.05) * mm, "end": v(-43.5, -10.8) * mm});
            skArc(sketch, "E977", {"start": v(-43.5, -10.8) * mm, "mid": v(-43.58, -10.72) * mm, "end": v(-43.65, -10.8) * mm});
            skLineSegment(sketch, "E978", {"start": v(-43.58, -11.13) * mm, "end": v(-42.81, -11.13) * mm});
            skArc(sketch, "E979", {"start": v(-42.81, -11.13) * mm, "mid": v(-42.74, -11.05) * mm, "end": v(-42.81, -10.98) * mm});
            skLineSegment(sketch, "E980", {"start": v(-42.81, -10.98) * mm, "end": v(-43.58, -10.98) * mm});
            skArc(sketch, "E981", {"start": v(-43.58, -10.98) * mm, "mid": v(-43.65, -11.05) * mm, "end": v(-43.58, -11.13) * mm});
            skLineSegment(sketch, "E982", {"start": v(-43.58, -10.72) * mm, "end": v(-46.62, -10.72) * mm});
            skArc(sketch, "E983", {"start": v(-46.62, -10.72) * mm, "mid": v(-46.7, -10.8) * mm, "end": v(-46.62, -10.87) * mm});
            skLineSegment(sketch, "E984", {"start": v(-46.62, -10.87) * mm, "end": v(-43.58, -10.87) * mm});
            skArc(sketch, "E985", {"start": v(-43.58, -10.87) * mm, "mid": v(-43.5, -10.8) * mm, "end": v(-43.58, -10.72) * mm});
            skLineSegment(sketch, "E986", {"start": v(-46.82, -11.1) * mm, "end": v(-46.57, -10.85) * mm});
            skArc(sketch, "E987", {"start": v(-46.57, -10.85) * mm, "mid": v(-46.57, -10.74) * mm, "end": v(-46.68, -10.74) * mm});
            skLineSegment(sketch, "E988", {"start": v(-46.68, -10.74) * mm, "end": v(-46.93, -11) * mm});
            skArc(sketch, "E989", {"start": v(-46.93, -11) * mm, "mid": v(-46.93, -11.1) * mm, "end": v(-46.82, -11.1) * mm});
            skLineSegment(sketch, "E990", {"start": v(-42.81, -23.32) * mm, "end": v(-40.78, -23.32) * mm});
            skArc(sketch, "E991", {"start": v(-40.78, -23.32) * mm, "mid": v(-40.7, -23.24) * mm, "end": v(-40.78, -23.17) * mm});
            skLineSegment(sketch, "E992", {"start": v(-40.78, -23.17) * mm, "end": v(-42.81, -23.17) * mm});
            skArc(sketch, "E993", {"start": v(-42.81, -23.17) * mm, "mid": v(-42.9, -23.24) * mm, "end": v(-42.81, -23.32) * mm});
            skLineSegment(sketch, "E994", {"start": v(-40.78, -23.32) * mm, "end": v(-40.02, -23.32) * mm});
            skArc(sketch, "E995", {"start": v(-40.02, -23.32) * mm, "mid": v(-39.94, -23.24) * mm, "end": v(-40.02, -23.17) * mm});
            skLineSegment(sketch, "E996", {"start": v(-40.02, -23.17) * mm, "end": v(-40.78, -23.17) * mm});
            skArc(sketch, "E997", {"start": v(-40.78, -23.17) * mm, "mid": v(-40.86, -23.24) * mm, "end": v(-40.78, -23.32) * mm});
            skLineSegment(sketch, "E998", {"start": v(-43.65, -23.24) * mm, "end": v(-43.65, -23.5) * mm});
            skArc(sketch, "E999", {"start": v(-43.65, -23.5) * mm, "mid": v(-43.58, -23.57) * mm, "end": v(-43.5, -23.5) * mm});
            skLineSegment(sketch, "E1000", {"start": v(-43.5, -23.5) * mm, "end": v(-43.5, -23.24) * mm});
            skArc(sketch, "E1001", {"start": v(-43.5, -23.24) * mm, "mid": v(-43.58, -23.17) * mm, "end": v(-43.65, -23.24) * mm});
            skLineSegment(sketch, "E1002", {"start": v(-43.58, -23.32) * mm, "end": v(-42.81, -23.32) * mm});
            skArc(sketch, "E1003", {"start": v(-42.81, -23.32) * mm, "mid": v(-42.74, -23.24) * mm, "end": v(-42.81, -23.17) * mm});
            skLineSegment(sketch, "E1004", {"start": v(-42.81, -23.17) * mm, "end": v(-43.58, -23.17) * mm});
            skArc(sketch, "E1005", {"start": v(-43.58, -23.17) * mm, "mid": v(-43.65, -23.24) * mm, "end": v(-43.58, -23.32) * mm});
            skLineSegment(sketch, "E1006", {"start": v(-43.58, -23.42) * mm, "end": v(-46.62, -23.42) * mm});
            skArc(sketch, "E1007", {"start": v(-46.62, -23.42) * mm, "mid": v(-46.7, -23.5) * mm, "end": v(-46.62, -23.57) * mm});
            skLineSegment(sketch, "E1008", {"start": v(-46.62, -23.57) * mm, "end": v(-43.58, -23.57) * mm});
            skArc(sketch, "E1009", {"start": v(-43.58, -23.57) * mm, "mid": v(-43.5, -23.5) * mm, "end": v(-43.58, -23.42) * mm});
            skLineSegment(sketch, "E1010", {"start": v(-46.57, -23.44) * mm, "end": v(-46.82, -23.2) * mm});
            skArc(sketch, "E1011", {"start": v(-46.82, -23.2) * mm, "mid": v(-46.93, -23.2) * mm, "end": v(-46.93, -23.3) * mm});
            skLineSegment(sketch, "E1012", {"start": v(-46.93, -23.3) * mm, "end": v(-46.68, -23.55) * mm});
            skArc(sketch, "E1013", {"start": v(-46.68, -23.55) * mm, "mid": v(-46.57, -23.55) * mm, "end": v(-46.57, -23.44) * mm});
            skLineSegment(sketch, "E1014", {"start": v(-40.1, -23.24) * mm, "end": v(-40.1, -23.5) * mm});
            skArc(sketch, "E1015", {"start": v(-40.1, -23.5) * mm, "mid": v(-40.02, -23.57) * mm, "end": v(-39.94, -23.5) * mm});
            skLineSegment(sketch, "E1016", {"start": v(-39.94, -23.5) * mm, "end": v(-39.94, -23.24) * mm});
            skArc(sketch, "E1017", {"start": v(-39.94, -23.24) * mm, "mid": v(-40.02, -23.17) * mm, "end": v(-40.1, -23.24) * mm});
            skLineSegment(sketch, "E1018", {"start": v(-40.02, -23.32) * mm, "end": v(-36.72, -23.32) * mm});
            skArc(sketch, "E1019", {"start": v(-36.72, -23.32) * mm, "mid": v(-36.64, -23.24) * mm, "end": v(-36.72, -23.17) * mm});
            skLineSegment(sketch, "E1020", {"start": v(-36.72, -23.17) * mm, "end": v(-40.02, -23.17) * mm});
            skArc(sketch, "E1021", {"start": v(-40.02, -23.17) * mm, "mid": v(-40.1, -23.24) * mm, "end": v(-40.02, -23.32) * mm});
            skLineSegment(sketch, "E1022", {"start": v(-36.97, -23.42) * mm, "end": v(-40.02, -23.42) * mm});
            skArc(sketch, "E1023", {"start": v(-40.02, -23.42) * mm, "mid": v(-40.1, -23.5) * mm, "end": v(-40.02, -23.57) * mm});
            skLineSegment(sketch, "E1024", {"start": v(-40.02, -23.57) * mm, "end": v(-36.97, -23.57) * mm});
            skArc(sketch, "E1025", {"start": v(-36.97, -23.57) * mm, "mid": v(-36.9, -23.5) * mm, "end": v(-36.97, -23.42) * mm});
            skLineSegment(sketch, "E1026", {"start": v(-36.77, -23.2) * mm, "end": v(-37.03, -23.44) * mm});
            skArc(sketch, "E1027", {"start": v(-37.03, -23.44) * mm, "mid": v(-37.03, -23.55) * mm, "end": v(-36.92, -23.55) * mm});
            skLineSegment(sketch, "E1028", {"start": v(-36.92, -23.55) * mm, "end": v(-36.66, -23.3) * mm});
            skArc(sketch, "E1029", {"start": v(-36.66, -23.3) * mm, "mid": v(-36.66, -23.2) * mm, "end": v(-36.77, -23.2) * mm});
            skLineSegment(sketch, "E1030", {"start": v(-46.88, -14.68) * mm, "end": v(-46.37, -14.68) * mm});
            skArc(sketch, "E1031", {"start": v(-46.37, -14.68) * mm, "mid": v(-46.3, -14.6) * mm, "end": v(-46.37, -14.53) * mm});
            skLineSegment(sketch, "E1032", {"start": v(-46.37, -14.53) * mm, "end": v(-46.88, -14.53) * mm});
            skArc(sketch, "E1033", {"start": v(-46.88, -14.53) * mm, "mid": v(-46.95, -14.6) * mm, "end": v(-46.88, -14.68) * mm});
            skLineSegment(sketch, "E1034", {"start": v(-38.88, -14.68) * mm, "end": v(-36.72, -14.68) * mm});
            skArc(sketch, "E1035", {"start": v(-36.72, -14.68) * mm, "mid": v(-36.64, -14.6) * mm, "end": v(-36.72, -14.53) * mm});
            skLineSegment(sketch, "E1036", {"start": v(-36.72, -14.53) * mm, "end": v(-38.88, -14.53) * mm});
            skArc(sketch, "E1037", {"start": v(-38.88, -14.53) * mm, "mid": v(-38.95, -14.6) * mm, "end": v(-38.88, -14.68) * mm});
            skLineSegment(sketch, "E1038", {"start": v(-46.88, -19.76) * mm, "end": v(-46.37, -19.76) * mm});
            skArc(sketch, "E1039", {"start": v(-46.37, -19.76) * mm, "mid": v(-46.3, -19.69) * mm, "end": v(-46.37, -19.61) * mm});
            skLineSegment(sketch, "E1040", {"start": v(-46.37, -19.61) * mm, "end": v(-46.88, -19.61) * mm});
            skArc(sketch, "E1041", {"start": v(-46.88, -19.61) * mm, "mid": v(-46.95, -19.69) * mm, "end": v(-46.88, -19.76) * mm});
            skLineSegment(sketch, "E1042", {"start": v(-38.88, -19.76) * mm, "end": v(-36.72, -19.76) * mm});
            skArc(sketch, "E1043", {"start": v(-36.72, -19.76) * mm, "mid": v(-36.64, -19.69) * mm, "end": v(-36.72, -19.61) * mm});
            skLineSegment(sketch, "E1044", {"start": v(-36.72, -19.61) * mm, "end": v(-38.88, -19.61) * mm});
            skArc(sketch, "E1045", {"start": v(-38.88, -19.61) * mm, "mid": v(-38.95, -19.69) * mm, "end": v(-38.88, -19.76) * mm});
            skLineSegment(sketch, "E1046", {"start": v(-46.45, -14.6) * mm, "end": v(-46.45, -16.39) * mm});
            skArc(sketch, "E1047", {"start": v(-46.45, -16.39) * mm, "mid": v(-46.37, -16.46) * mm, "end": v(-46.3, -16.39) * mm});
            skLineSegment(sketch, "E1048", {"start": v(-46.3, -16.39) * mm, "end": v(-46.3, -14.6) * mm});
            skArc(sketch, "E1049", {"start": v(-46.3, -14.6) * mm, "mid": v(-46.37, -14.53) * mm, "end": v(-46.45, -14.6) * mm});
            skLineSegment(sketch, "E1050", {"start": v(-46.37, -14.68) * mm, "end": v(-44.72, -14.68) * mm});
            skArc(sketch, "E1051", {"start": v(-44.72, -14.68) * mm, "mid": v(-44.64, -14.6) * mm, "end": v(-44.72, -14.53) * mm});
            skLineSegment(sketch, "E1052", {"start": v(-44.72, -14.53) * mm, "end": v(-46.37, -14.53) * mm});
            skArc(sketch, "E1053", {"start": v(-46.37, -14.53) * mm, "mid": v(-46.45, -14.6) * mm, "end": v(-46.37, -14.68) * mm});
            skLineSegment(sketch, "E1054", {"start": v(-46.44, -16.36) * mm, "end": v(-46.95, -17.89) * mm});
            skArc(sketch, "E1055", {"start": v(-46.95, -17.89) * mm, "mid": v(-46.9, -17.98) * mm, "end": v(-46.8, -17.93) * mm});
            skLineSegment(sketch, "E1056", {"start": v(-46.8, -17.93) * mm, "end": v(-46.3, -16.41) * mm});
            skArc(sketch, "E1057", {"start": v(-46.3, -16.41) * mm, "mid": v(-46.35, -16.31) * mm, "end": v(-46.44, -16.36) * mm});
            skLineSegment(sketch, "E1058", {"start": v(-46.45, -17.91) * mm, "end": v(-46.45, -19.69) * mm});
            skArc(sketch, "E1059", {"start": v(-46.45, -19.69) * mm, "mid": v(-46.37, -19.76) * mm, "end": v(-46.3, -19.69) * mm});
            skLineSegment(sketch, "E1060", {"start": v(-46.3, -19.69) * mm, "end": v(-46.3, -17.91) * mm});
            skArc(sketch, "E1061", {"start": v(-46.3, -17.91) * mm, "mid": v(-46.37, -17.83) * mm, "end": v(-46.45, -17.91) * mm});
            skLineSegment(sketch, "E1062", {"start": v(-46.37, -19.76) * mm, "end": v(-44.72, -19.76) * mm});
            skArc(sketch, "E1063", {"start": v(-44.72, -19.76) * mm, "mid": v(-44.64, -19.69) * mm, "end": v(-44.72, -19.61) * mm});
            skLineSegment(sketch, "E1064", {"start": v(-44.72, -19.61) * mm, "end": v(-46.37, -19.61) * mm});
            skArc(sketch, "E1065", {"start": v(-46.37, -19.61) * mm, "mid": v(-46.45, -19.69) * mm, "end": v(-46.37, -19.76) * mm});
            skLineSegment(sketch, "E1066", {"start": v(-47.15, -12.56) * mm, "end": v(-46.77, -12.18) * mm});
            skArc(sketch, "E1067", {"start": v(-46.77, -12.18) * mm, "mid": v(-46.77, -12.09) * mm, "end": v(-46.86, -12.09) * mm});
            skLineSegment(sketch, "E1068", {"start": v(-46.86, -12.09) * mm, "end": v(-47.24, -12.47) * mm});
            skArc(sketch, "E1069", {"start": v(-47.24, -12.47) * mm, "mid": v(-47.24, -12.56) * mm, "end": v(-47.15, -12.56) * mm});
            skLineSegment(sketch, "E1070", {"start": v(-46.88, -12.13) * mm, "end": v(-46.88, -13.27) * mm});
            skArc(sketch, "E1071", {"start": v(-46.88, -13.27) * mm, "mid": v(-46.81, -13.34) * mm, "end": v(-46.75, -13.27) * mm});
            skLineSegment(sketch, "E1072", {"start": v(-46.75, -13.27) * mm, "end": v(-46.75, -12.13) * mm});
            skArc(sketch, "E1073", {"start": v(-46.75, -12.13) * mm, "mid": v(-46.81, -12.07) * mm, "end": v(-46.88, -12.13) * mm});
            skLineSegment(sketch, "E1074", {"start": v(-47.2, -13.34) * mm, "end": v(-46.43, -13.34) * mm});
            skArc(sketch, "E1075", {"start": v(-46.43, -13.34) * mm, "mid": v(-46.37, -13.27) * mm, "end": v(-46.43, -13.21) * mm});
            skLineSegment(sketch, "E1076", {"start": v(-46.43, -13.21) * mm, "end": v(-47.2, -13.21) * mm});
            skArc(sketch, "E1077", {"start": v(-47.2, -13.21) * mm, "mid": v(-47.26, -13.27) * mm, "end": v(-47.2, -13.34) * mm});
            skLineSegment(sketch, "E1078", {"start": v(-36.78, -13.21) * mm, "end": v(-37.54, -13.21) * mm});
            skArc(sketch, "E1079", {"start": v(-37.54, -13.21) * mm, "mid": v(-37.6, -13.27) * mm, "end": v(-37.54, -13.34) * mm});
            skLineSegment(sketch, "E1080", {"start": v(-37.54, -13.34) * mm, "end": v(-36.78, -13.34) * mm});
            skArc(sketch, "E1081", {"start": v(-36.78, -13.34) * mm, "mid": v(-36.72, -13.27) * mm, "end": v(-36.78, -13.21) * mm});
            skLineSegment(sketch, "E1082", {"start": v(-37.5, -13.32) * mm, "end": v(-36.74, -12.56) * mm});
            skArc(sketch, "E1083", {"start": v(-36.74, -12.56) * mm, "mid": v(-36.74, -12.47) * mm, "end": v(-36.83, -12.47) * mm});
            skLineSegment(sketch, "E1084", {"start": v(-36.83, -12.47) * mm, "end": v(-37.59, -13.23) * mm});
            skArc(sketch, "E1085", {"start": v(-37.59, -13.23) * mm, "mid": v(-37.59, -13.32) * mm, "end": v(-37.5, -13.32) * mm});
            skLineSegment(sketch, "E1086", {"start": v(-36.72, -12.51) * mm, "end": v(-36.72, -12.32) * mm});
            skArc(sketch, "E1087", {"start": v(-36.72, -12.32) * mm, "mid": v(-36.78, -12.26) * mm, "end": v(-36.84, -12.32) * mm});
            skLineSegment(sketch, "E1088", {"start": v(-36.84, -12.32) * mm, "end": v(-36.84, -12.51) * mm});
            skArc(sketch, "E1089", {"start": v(-36.84, -12.51) * mm, "mid": v(-36.78, -12.58) * mm, "end": v(-36.72, -12.51) * mm});
            skLineSegment(sketch, "E1090", {"start": v(-36.74, -12.28) * mm, "end": v(-36.93, -12.09) * mm});
            skArc(sketch, "E1091", {"start": v(-36.93, -12.09) * mm, "mid": v(-37.02, -12.09) * mm, "end": v(-37.02, -12.18) * mm});
            skLineSegment(sketch, "E1092", {"start": v(-37.02, -12.18) * mm, "end": v(-36.83, -12.37) * mm});
            skArc(sketch, "E1093", {"start": v(-36.83, -12.37) * mm, "mid": v(-36.74, -12.37) * mm, "end": v(-36.74, -12.28) * mm});
            skLineSegment(sketch, "E1094", {"start": v(-36.97, -12.07) * mm, "end": v(-37.35, -12.07) * mm});
            skArc(sketch, "E1095", {"start": v(-37.35, -12.07) * mm, "mid": v(-37.42, -12.13) * mm, "end": v(-37.35, -12.2) * mm});
            skLineSegment(sketch, "E1096", {"start": v(-37.35, -12.2) * mm, "end": v(-36.97, -12.2) * mm});
            skArc(sketch, "E1097", {"start": v(-36.97, -12.2) * mm, "mid": v(-36.9, -12.13) * mm, "end": v(-36.97, -12.07) * mm});
            skLineSegment(sketch, "E1098", {"start": v(-37.4, -12.09) * mm, "end": v(-37.59, -12.28) * mm});
            skArc(sketch, "E1099", {"start": v(-37.59, -12.28) * mm, "mid": v(-37.59, -12.37) * mm, "end": v(-37.5, -12.37) * mm});
            skLineSegment(sketch, "E1100", {"start": v(-37.5, -12.37) * mm, "end": v(-37.3, -12.18) * mm});
            skArc(sketch, "E1101", {"start": v(-37.3, -12.18) * mm, "mid": v(-37.3, -12.09) * mm, "end": v(-37.4, -12.09) * mm});
            skLineSegment(sketch, "E1102", {"start": v(-47.15, -21.26) * mm, "end": v(-46.96, -21.07) * mm});
            skArc(sketch, "E1103", {"start": v(-46.96, -21.07) * mm, "mid": v(-46.96, -20.98) * mm, "end": v(-47.05, -20.98) * mm});
            skLineSegment(sketch, "E1104", {"start": v(-47.05, -20.98) * mm, "end": v(-47.24, -21.17) * mm});
            skArc(sketch, "E1105", {"start": v(-47.24, -21.17) * mm, "mid": v(-47.24, -21.26) * mm, "end": v(-47.15, -21.26) * mm});
            skLineSegment(sketch, "E1106", {"start": v(-47, -21.08) * mm, "end": v(-46.62, -21.08) * mm});
            skArc(sketch, "E1107", {"start": v(-46.62, -21.08) * mm, "mid": v(-46.56, -21.02) * mm, "end": v(-46.62, -20.96) * mm});
            skLineSegment(sketch, "E1108", {"start": v(-46.62, -20.96) * mm, "end": v(-47, -20.96) * mm});
            skArc(sketch, "E1109", {"start": v(-47, -20.96) * mm, "mid": v(-47.07, -21.02) * mm, "end": v(-47, -21.08) * mm});
            skLineSegment(sketch, "E1110", {"start": v(-46.67, -21.07) * mm, "end": v(-46.48, -21.26) * mm});
            skArc(sketch, "E1111", {"start": v(-46.48, -21.26) * mm, "mid": v(-46.39, -21.26) * mm, "end": v(-46.39, -21.17) * mm});
            skLineSegment(sketch, "E1112", {"start": v(-46.39, -21.17) * mm, "end": v(-46.58, -20.98) * mm});
            skArc(sketch, "E1113", {"start": v(-46.58, -20.98) * mm, "mid": v(-46.67, -20.98) * mm, "end": v(-46.67, -21.07) * mm});
            skLineSegment(sketch, "E1114", {"start": v(-46.5, -21.21) * mm, "end": v(-46.5, -21.4) * mm});
            skArc(sketch, "E1115", {"start": v(-46.5, -21.4) * mm, "mid": v(-46.43, -21.47) * mm, "end": v(-46.37, -21.4) * mm});
            skLineSegment(sketch, "E1116", {"start": v(-46.37, -21.4) * mm, "end": v(-46.37, -21.21) * mm});
            skArc(sketch, "E1117", {"start": v(-46.37, -21.21) * mm, "mid": v(-46.43, -21.15) * mm, "end": v(-46.5, -21.21) * mm});
            skLineSegment(sketch, "E1118", {"start": v(-46.48, -21.36) * mm, "end": v(-46.67, -21.55) * mm});
            skArc(sketch, "E1119", {"start": v(-46.67, -21.55) * mm, "mid": v(-46.67, -21.64) * mm, "end": v(-46.58, -21.64) * mm});
            skLineSegment(sketch, "E1120", {"start": v(-46.58, -21.64) * mm, "end": v(-46.39, -21.45) * mm});
            skArc(sketch, "E1121", {"start": v(-46.39, -21.45) * mm, "mid": v(-46.39, -21.36) * mm, "end": v(-46.48, -21.36) * mm});
            skLineSegment(sketch, "E1122", {"start": v(-46.62, -21.53) * mm, "end": v(-46.81, -21.53) * mm});
            skArc(sketch, "E1123", {"start": v(-46.81, -21.53) * mm, "mid": v(-46.88, -21.6) * mm, "end": v(-46.81, -21.66) * mm});
            skLineSegment(sketch, "E1124", {"start": v(-46.81, -21.66) * mm, "end": v(-46.62, -21.66) * mm});
            skArc(sketch, "E1125", {"start": v(-46.62, -21.66) * mm, "mid": v(-46.56, -21.6) * mm, "end": v(-46.62, -21.53) * mm});
            skLineSegment(sketch, "E1126", {"start": v(-46.67, -21.64) * mm, "end": v(-46.48, -21.83) * mm});
            skArc(sketch, "E1127", {"start": v(-46.48, -21.83) * mm, "mid": v(-46.39, -21.83) * mm, "end": v(-46.39, -21.74) * mm});
            skLineSegment(sketch, "E1128", {"start": v(-46.39, -21.74) * mm, "end": v(-46.58, -21.55) * mm});
            skArc(sketch, "E1129", {"start": v(-46.58, -21.55) * mm, "mid": v(-46.67, -21.55) * mm, "end": v(-46.67, -21.64) * mm});
            skLineSegment(sketch, "E1130", {"start": v(-46.5, -21.78) * mm, "end": v(-46.5, -21.97) * mm});
            skArc(sketch, "E1131", {"start": v(-46.5, -21.97) * mm, "mid": v(-46.43, -22.04) * mm, "end": v(-46.37, -21.97) * mm});
            skLineSegment(sketch, "E1132", {"start": v(-46.37, -21.97) * mm, "end": v(-46.37, -21.78) * mm});
            skArc(sketch, "E1133", {"start": v(-46.37, -21.78) * mm, "mid": v(-46.43, -21.72) * mm, "end": v(-46.5, -21.78) * mm});
            skLineSegment(sketch, "E1134", {"start": v(-46.48, -21.93) * mm, "end": v(-46.67, -22.12) * mm});
            skArc(sketch, "E1135", {"start": v(-46.67, -22.12) * mm, "mid": v(-46.67, -22.2) * mm, "end": v(-46.58, -22.2) * mm});
            skLineSegment(sketch, "E1136", {"start": v(-46.58, -22.2) * mm, "end": v(-46.39, -22.02) * mm});
            skArc(sketch, "E1137", {"start": v(-46.39, -22.02) * mm, "mid": v(-46.39, -21.93) * mm, "end": v(-46.48, -21.93) * mm});
            skLineSegment(sketch, "E1138", {"start": v(-46.62, -22.1) * mm, "end": v(-47, -22.1) * mm});
            skArc(sketch, "E1139", {"start": v(-47, -22.1) * mm, "mid": v(-47.07, -22.16) * mm, "end": v(-47, -22.23) * mm});
            skLineSegment(sketch, "E1140", {"start": v(-47, -22.23) * mm, "end": v(-46.62, -22.23) * mm});
            skArc(sketch, "E1141", {"start": v(-46.62, -22.23) * mm, "mid": v(-46.56, -22.16) * mm, "end": v(-46.62, -22.1) * mm});
            skLineSegment(sketch, "E1142", {"start": v(-46.96, -22.12) * mm, "end": v(-47.15, -21.93) * mm});
            skArc(sketch, "E1143", {"start": v(-47.15, -21.93) * mm, "mid": v(-47.24, -21.93) * mm, "end": v(-47.24, -22.02) * mm});
            skLineSegment(sketch, "E1144", {"start": v(-47.24, -22.02) * mm, "end": v(-47.05, -22.2) * mm});
            skArc(sketch, "E1145", {"start": v(-47.05, -22.2) * mm, "mid": v(-46.96, -22.2) * mm, "end": v(-46.96, -22.12) * mm});
            skLineSegment(sketch, "E1146", {"start": v(-36.78, -22.16) * mm, "end": v(-36.78, -21.02) * mm});
            skArc(sketch, "E1147", {"start": v(-36.78, -21.02) * mm, "mid": v(-36.84, -20.96) * mm, "end": v(-36.9, -21.02) * mm});
            skLineSegment(sketch, "E1148", {"start": v(-36.9, -21.02) * mm, "end": v(-36.9, -22.16) * mm});
            skArc(sketch, "E1149", {"start": v(-36.9, -22.16) * mm, "mid": v(-36.84, -22.23) * mm, "end": v(-36.78, -22.16) * mm});
            skLineSegment(sketch, "E1150", {"start": v(-36.89, -20.98) * mm, "end": v(-37.46, -21.55) * mm});
            skArc(sketch, "E1151", {"start": v(-37.46, -21.55) * mm, "mid": v(-37.46, -21.64) * mm, "end": v(-37.37, -21.64) * mm});
            skLineSegment(sketch, "E1152", {"start": v(-37.37, -21.64) * mm, "end": v(-36.8, -21.07) * mm});
            skArc(sketch, "E1153", {"start": v(-36.8, -21.07) * mm, "mid": v(-36.8, -20.98) * mm, "end": v(-36.89, -20.98) * mm});
            skLineSegment(sketch, "E1154", {"start": v(-37.42, -21.66) * mm, "end": v(-36.65, -21.66) * mm});
            skArc(sketch, "E1155", {"start": v(-36.65, -21.66) * mm, "mid": v(-36.6, -21.6) * mm, "end": v(-36.65, -21.53) * mm});
            skLineSegment(sketch, "E1156", {"start": v(-36.65, -21.53) * mm, "end": v(-37.42, -21.53) * mm});
            skArc(sketch, "E1157", {"start": v(-37.42, -21.53) * mm, "mid": v(-37.48, -21.6) * mm, "end": v(-37.42, -21.66) * mm});
            skCircle(sketch, "E1158", {"center": v(-41.8, -17.15) * mm, "radius": 3.48 * mm});
            skCircle(sketch, "E1159", {"center": v(-41.8, -17.15) * mm, "radius": 3.63 * mm});
            skCircle(sketch, "E1160", {"center": v(-41.8, -17.15) * mm, "radius": 1 * mm});
            skCircle(sketch, "E1161", {"center": v(-41.8, -17.15) * mm, "radius": 1.04 * mm});
            skCircle(sketch, "E1162", {"center": v(-41.8, -17.15) * mm, "radius": 0.74 * mm});
            skCircle(sketch, "E1163", {"center": v(-41.8, -17.15) * mm, "radius": 0.79 * mm});
            skCircle(sketch, "E1164", {"center": v(-46.37, -14.6) * mm, "radius": 0.05 * mm});
            skCircle(sketch, "E1165", {"center": v(-46.37, -14.6) * mm, "radius": 0.2 * mm});
            skCircle(sketch, "E1166", {"center": v(-46.37, -19.69) * mm, "radius": 0.05 * mm});
            skCircle(sketch, "E1167", {"center": v(-46.37, -19.69) * mm, "radius": 0.2 * mm});
            skLineSegment(sketch, "E1168", {"start": v(-48.94, -15.55) * mm, "end": v(-47.15, -15.55) * mm});
            skArc(sketch, "E1169", {"start": v(-47.15, -15.16) * mm, "mid": v(-46.65, -14.66) * mm, "end": v(-47.15, -14.16) * mm});
            skLineSegment(sketch, "E1170", {"start": v(-47.15, -13.76) * mm, "end": v(-48.94, -13.76) * mm});
            skArc(sketch, "E1171", {"start": v(-48.94, -14.16) * mm, "mid": v(-49.44, -14.66) * mm, "end": v(-48.94, -15.16) * mm});
            skLineSegment(sketch, "E1172", {"start": v(-36.45, -15.55) * mm, "end": v(-34.65, -15.55) * mm});
            skArc(sketch, "E1173", {"start": v(-34.65, -15.16) * mm, "mid": v(-34.15, -14.66) * mm, "end": v(-34.65, -14.16) * mm});
            skLineSegment(sketch, "E1174", {"start": v(-34.65, -13.76) * mm, "end": v(-36.45, -13.76) * mm});
            skArc(sketch, "E1175", {"start": v(-36.45, -14.16) * mm, "mid": v(-36.95, -14.66) * mm, "end": v(-36.45, -15.16) * mm});
            skLineSegment(sketch, "E1176", {"start": v(-48.94, -20.53) * mm, "end": v(-47.15, -20.53) * mm});
            skArc(sketch, "E1177", {"start": v(-47.15, -20.14) * mm, "mid": v(-46.65, -19.64) * mm, "end": v(-47.15, -19.14) * mm});
            skLineSegment(sketch, "E1178", {"start": v(-47.15, -18.74) * mm, "end": v(-48.94, -18.74) * mm});
            skArc(sketch, "E1179", {"start": v(-48.94, -19.14) * mm, "mid": v(-49.44, -19.64) * mm, "end": v(-48.94, -20.14) * mm});
            skLineSegment(sketch, "E1180", {"start": v(-36.45, -20.53) * mm, "end": v(-34.65, -20.53) * mm});
            skArc(sketch, "E1181", {"start": v(-34.65, -20.14) * mm, "mid": v(-34.15, -19.64) * mm, "end": v(-34.65, -19.14) * mm});
            skLineSegment(sketch, "E1182", {"start": v(-34.65, -18.74) * mm, "end": v(-36.45, -18.74) * mm});
            skArc(sketch, "E1183", {"start": v(-36.45, -19.14) * mm, "mid": v(-36.95, -19.64) * mm, "end": v(-36.45, -20.14) * mm});
            skLineSegment(sketch, "E1184", {"start": v(-43.7, -40.72) * mm, "end": v(-39.9, -40.72) * mm});
            skArc(sketch, "E1185", {"start": v(-39.9, -40.72) * mm, "mid": v(-39.82, -40.64) * mm, "end": v(-39.9, -40.57) * mm});
            skLineSegment(sketch, "E1186", {"start": v(-39.9, -40.57) * mm, "end": v(-43.7, -40.57) * mm});
            skArc(sketch, "E1187", {"start": v(-43.7, -40.57) * mm, "mid": v(-43.78, -40.64) * mm, "end": v(-43.7, -40.72) * mm});
            skLineSegment(sketch, "E1188", {"start": v(-39.82, -44.45) * mm, "end": v(-39.82, -40.64) * mm});
            skArc(sketch, "E1189", {"start": v(-39.82, -40.64) * mm, "mid": v(-39.9, -40.57) * mm, "end": v(-39.97, -40.64) * mm});
            skLineSegment(sketch, "E1190", {"start": v(-39.97, -40.64) * mm, "end": v(-39.97, -44.45) * mm});
            skArc(sketch, "E1191", {"start": v(-39.97, -44.45) * mm, "mid": v(-39.9, -44.53) * mm, "end": v(-39.82, -44.45) * mm});
            skLineSegment(sketch, "E1192", {"start": v(-39.9, -44.38) * mm, "end": v(-43.7, -44.38) * mm});
            skArc(sketch, "E1193", {"start": v(-43.7, -44.38) * mm, "mid": v(-43.78, -44.45) * mm, "end": v(-43.7, -44.53) * mm});
            skLineSegment(sketch, "E1194", {"start": v(-43.7, -44.53) * mm, "end": v(-39.9, -44.53) * mm});
            skArc(sketch, "E1195", {"start": v(-39.9, -44.53) * mm, "mid": v(-39.82, -44.45) * mm, "end": v(-39.9, -44.38) * mm});
            skLineSegment(sketch, "E1196", {"start": v(-43.78, -40.64) * mm, "end": v(-43.78, -44.45) * mm});
            skArc(sketch, "E1197", {"start": v(-43.78, -44.45) * mm, "mid": v(-43.7, -44.53) * mm, "end": v(-43.63, -44.45) * mm});
            skLineSegment(sketch, "E1198", {"start": v(-43.63, -44.45) * mm, "end": v(-43.63, -40.64) * mm});
            skArc(sketch, "E1199", {"start": v(-43.63, -40.64) * mm, "mid": v(-43.7, -40.57) * mm, "end": v(-43.78, -40.64) * mm});
            skLineSegment(sketch, "E1200", {"start": v(-43.45, -40.92) * mm, "end": v(-40.15, -40.92) * mm});
            skArc(sketch, "E1201", {"start": v(-40.15, -40.92) * mm, "mid": v(-40.12, -40.9) * mm, "end": v(-40.15, -40.87) * mm});
            skLineSegment(sketch, "E1202", {"start": v(-40.15, -40.87) * mm, "end": v(-43.45, -40.87) * mm});
            skArc(sketch, "E1203", {"start": v(-43.45, -40.87) * mm, "mid": v(-43.47, -40.9) * mm, "end": v(-43.45, -40.92) * mm});
            skLineSegment(sketch, "E1204", {"start": v(-40.12, -44.2) * mm, "end": v(-40.12, -40.9) * mm});
            skArc(sketch, "E1205", {"start": v(-40.12, -40.9) * mm, "mid": v(-40.15, -40.87) * mm, "end": v(-40.17, -40.9) * mm});
            skLineSegment(sketch, "E1206", {"start": v(-40.17, -40.9) * mm, "end": v(-40.17, -44.2) * mm});
            skArc(sketch, "E1207", {"start": v(-40.17, -44.2) * mm, "mid": v(-40.15, -44.22) * mm, "end": v(-40.12, -44.2) * mm});
            skLineSegment(sketch, "E1208", {"start": v(-40.15, -44.17) * mm, "end": v(-43.45, -44.17) * mm});
            skArc(sketch, "E1209", {"start": v(-43.45, -44.17) * mm, "mid": v(-43.47, -44.2) * mm, "end": v(-43.45, -44.22) * mm});
            skLineSegment(sketch, "E1210", {"start": v(-43.45, -44.22) * mm, "end": v(-40.15, -44.22) * mm});
            skArc(sketch, "E1211", {"start": v(-40.15, -44.22) * mm, "mid": v(-40.12, -44.2) * mm, "end": v(-40.15, -44.17) * mm});
            skLineSegment(sketch, "E1212", {"start": v(-43.47, -40.9) * mm, "end": v(-43.47, -44.2) * mm});
            skArc(sketch, "E1213", {"start": v(-43.47, -44.2) * mm, "mid": v(-43.45, -44.22) * mm, "end": v(-43.42, -44.2) * mm});
            skLineSegment(sketch, "E1214", {"start": v(-43.42, -44.2) * mm, "end": v(-43.42, -40.9) * mm});
            skArc(sketch, "E1215", {"start": v(-43.42, -40.9) * mm, "mid": v(-43.45, -40.87) * mm, "end": v(-43.47, -40.9) * mm});
            skLineSegment(sketch, "E1216", {"start": v(-42.74, -36.45) * mm, "end": v(-42.74, -36.07) * mm});
            skArc(sketch, "E1217", {"start": v(-42.74, -36.07) * mm, "mid": v(-42.81, -36) * mm, "end": v(-42.9, -36.07) * mm});
            skLineSegment(sketch, "E1218", {"start": v(-42.9, -36.07) * mm, "end": v(-42.9, -36.45) * mm});
            skArc(sketch, "E1219", {"start": v(-42.9, -36.45) * mm, "mid": v(-42.81, -36.53) * mm, "end": v(-42.74, -36.45) * mm});
            skLineSegment(sketch, "E1220", {"start": v(-42.81, -36.53) * mm, "end": v(-40.78, -36.53) * mm});
            skArc(sketch, "E1221", {"start": v(-40.78, -36.53) * mm, "mid": v(-40.7, -36.45) * mm, "end": v(-40.78, -36.38) * mm});
            skLineSegment(sketch, "E1222", {"start": v(-40.78, -36.38) * mm, "end": v(-42.81, -36.38) * mm});
            skArc(sketch, "E1223", {"start": v(-42.81, -36.38) * mm, "mid": v(-42.9, -36.45) * mm, "end": v(-42.81, -36.53) * mm});
            skLineSegment(sketch, "E1224", {"start": v(-42.81, -36.15) * mm, "end": v(-40.78, -36.15) * mm});
            skArc(sketch, "E1225", {"start": v(-40.78, -36.15) * mm, "mid": v(-40.7, -36.07) * mm, "end": v(-40.78, -36) * mm});
            skLineSegment(sketch, "E1226", {"start": v(-40.78, -36) * mm, "end": v(-42.81, -36) * mm});
            skArc(sketch, "E1227", {"start": v(-42.81, -36) * mm, "mid": v(-42.9, -36.07) * mm, "end": v(-42.81, -36.15) * mm});
            skLineSegment(sketch, "E1228", {"start": v(-40.86, -36.07) * mm, "end": v(-40.86, -36.45) * mm});
            skArc(sketch, "E1229", {"start": v(-40.86, -36.45) * mm, "mid": v(-40.78, -36.53) * mm, "end": v(-40.7, -36.45) * mm});
            skLineSegment(sketch, "E1230", {"start": v(-40.7, -36.45) * mm, "end": v(-40.7, -36.07) * mm});
            skArc(sketch, "E1231", {"start": v(-40.7, -36.07) * mm, "mid": v(-40.78, -36) * mm, "end": v(-40.86, -36.07) * mm});
            skLineSegment(sketch, "E1232", {"start": v(-35.65, -37.41) * mm, "end": v(-36.66, -36.4) * mm});
            skArc(sketch, "E1233", {"start": v(-36.66, -36.4) * mm, "mid": v(-36.77, -36.4) * mm, "end": v(-36.77, -36.5) * mm});
            skLineSegment(sketch, "E1234", {"start": v(-36.77, -36.5) * mm, "end": v(-35.76, -37.52) * mm});
            skArc(sketch, "E1235", {"start": v(-35.76, -37.52) * mm, "mid": v(-35.65, -37.52) * mm, "end": v(-35.65, -37.41) * mm});
            skLineSegment(sketch, "E1236", {"start": v(-36.72, -36.38) * mm, "end": v(-40.02, -36.38) * mm});
            skArc(sketch, "E1237", {"start": v(-40.02, -36.38) * mm, "mid": v(-40.1, -36.45) * mm, "end": v(-40.02, -36.53) * mm});
            skLineSegment(sketch, "E1238", {"start": v(-40.02, -36.53) * mm, "end": v(-36.72, -36.53) * mm});
            skArc(sketch, "E1239", {"start": v(-36.72, -36.53) * mm, "mid": v(-36.64, -36.45) * mm, "end": v(-36.72, -36.38) * mm});
            skLineSegment(sketch, "E1240", {"start": v(-35.78, -37.47) * mm, "end": v(-35.78, -38.74) * mm});
            skArc(sketch, "E1241", {"start": v(-35.78, -38.74) * mm, "mid": v(-35.7, -38.81) * mm, "end": v(-35.63, -38.74) * mm});
            skLineSegment(sketch, "E1242", {"start": v(-35.63, -38.74) * mm, "end": v(-35.63, -37.47) * mm});
            skArc(sketch, "E1243", {"start": v(-35.63, -37.47) * mm, "mid": v(-35.7, -37.4) * mm, "end": v(-35.78, -37.47) * mm});
            skLineSegment(sketch, "E1244", {"start": v(-35.63, -41.4) * mm, "end": v(-35.63, -38.74) * mm});
            skArc(sketch, "E1245", {"start": v(-35.63, -38.74) * mm, "mid": v(-35.7, -38.66) * mm, "end": v(-35.78, -38.74) * mm});
            skLineSegment(sketch, "E1246", {"start": v(-35.78, -38.74) * mm, "end": v(-35.78, -41.4) * mm});
            skArc(sketch, "E1247", {"start": v(-35.78, -41.4) * mm, "mid": v(-35.7, -41.48) * mm, "end": v(-35.63, -41.4) * mm});
            skLineSegment(sketch, "E1248", {"start": v(-35.78, -41.4) * mm, "end": v(-35.78, -43.7) * mm});
            skArc(sketch, "E1249", {"start": v(-35.78, -43.7) * mm, "mid": v(-35.7, -43.77) * mm, "end": v(-35.63, -43.7) * mm});
            skLineSegment(sketch, "E1250", {"start": v(-35.63, -43.7) * mm, "end": v(-35.63, -41.4) * mm});
            skArc(sketch, "E1251", {"start": v(-35.63, -41.4) * mm, "mid": v(-35.7, -41.33) * mm, "end": v(-35.78, -41.4) * mm});
            skLineSegment(sketch, "E1252", {"start": v(-35.63, -46.36) * mm, "end": v(-35.63, -43.7) * mm});
            skArc(sketch, "E1253", {"start": v(-35.63, -43.7) * mm, "mid": v(-35.7, -43.62) * mm, "end": v(-35.78, -43.7) * mm});
            skLineSegment(sketch, "E1254", {"start": v(-35.78, -43.7) * mm, "end": v(-35.78, -46.36) * mm});
            skArc(sketch, "E1255", {"start": v(-35.78, -46.36) * mm, "mid": v(-35.7, -46.43) * mm, "end": v(-35.63, -46.36) * mm});
            skLineSegment(sketch, "E1256", {"start": v(-36.66, -48.7) * mm, "end": v(-35.65, -47.68) * mm});
            skArc(sketch, "E1257", {"start": v(-35.65, -47.68) * mm, "mid": v(-35.65, -47.57) * mm, "end": v(-35.76, -47.57) * mm});
            skLineSegment(sketch, "E1258", {"start": v(-35.76, -47.57) * mm, "end": v(-36.77, -48.6) * mm});
            skArc(sketch, "E1259", {"start": v(-36.77, -48.6) * mm, "mid": v(-36.77, -48.7) * mm, "end": v(-36.66, -48.7) * mm});
            skLineSegment(sketch, "E1260", {"start": v(-35.63, -47.63) * mm, "end": v(-35.63, -46.36) * mm});
            skArc(sketch, "E1261", {"start": v(-35.63, -46.36) * mm, "mid": v(-35.7, -46.28) * mm, "end": v(-35.78, -46.36) * mm});
            skLineSegment(sketch, "E1262", {"start": v(-35.78, -46.36) * mm, "end": v(-35.78, -47.63) * mm});
            skArc(sketch, "E1263", {"start": v(-35.78, -47.63) * mm, "mid": v(-35.7, -47.7) * mm, "end": v(-35.63, -47.63) * mm});
            skLineSegment(sketch, "E1264", {"start": v(-47.82, -41.4) * mm, "end": v(-47.82, -38.74) * mm});
            skArc(sketch, "E1265", {"start": v(-47.82, -38.74) * mm, "mid": v(-47.9, -38.66) * mm, "end": v(-47.97, -38.74) * mm});
            skLineSegment(sketch, "E1266", {"start": v(-47.97, -38.74) * mm, "end": v(-47.97, -41.4) * mm});
            skArc(sketch, "E1267", {"start": v(-47.97, -41.4) * mm, "mid": v(-47.9, -41.48) * mm, "end": v(-47.82, -41.4) * mm});
            skLineSegment(sketch, "E1268", {"start": v(-47.97, -41.4) * mm, "end": v(-47.97, -43.7) * mm});
            skArc(sketch, "E1269", {"start": v(-47.97, -43.7) * mm, "mid": v(-47.9, -43.77) * mm, "end": v(-47.82, -43.7) * mm});
            skLineSegment(sketch, "E1270", {"start": v(-47.82, -43.7) * mm, "end": v(-47.82, -41.4) * mm});
            skArc(sketch, "E1271", {"start": v(-47.82, -41.4) * mm, "mid": v(-47.9, -41.33) * mm, "end": v(-47.97, -41.4) * mm});
            skLineSegment(sketch, "E1272", {"start": v(-47.82, -46.36) * mm, "end": v(-47.82, -43.7) * mm});
            skArc(sketch, "E1273", {"start": v(-47.82, -43.7) * mm, "mid": v(-47.9, -43.62) * mm, "end": v(-47.97, -43.7) * mm});
            skLineSegment(sketch, "E1274", {"start": v(-47.97, -43.7) * mm, "end": v(-47.97, -46.36) * mm});
            skArc(sketch, "E1275", {"start": v(-47.97, -46.36) * mm, "mid": v(-47.9, -46.43) * mm, "end": v(-47.82, -46.36) * mm});
            skLineSegment(sketch, "E1276", {"start": v(-47.97, -46.36) * mm, "end": v(-47.97, -47.63) * mm});
            skArc(sketch, "E1277", {"start": v(-47.97, -47.63) * mm, "mid": v(-47.9, -47.7) * mm, "end": v(-47.82, -47.63) * mm});
            skLineSegment(sketch, "E1278", {"start": v(-47.82, -47.63) * mm, "end": v(-47.82, -46.36) * mm});
            skArc(sketch, "E1279", {"start": v(-47.82, -46.36) * mm, "mid": v(-47.9, -46.28) * mm, "end": v(-47.97, -46.36) * mm});
            skLineSegment(sketch, "E1280", {"start": v(-47.95, -47.68) * mm, "end": v(-46.93, -48.7) * mm});
            skArc(sketch, "E1281", {"start": v(-46.93, -48.7) * mm, "mid": v(-46.82, -48.7) * mm, "end": v(-46.82, -48.6) * mm});
            skLineSegment(sketch, "E1282", {"start": v(-46.82, -48.6) * mm, "end": v(-47.84, -47.57) * mm});
            skArc(sketch, "E1283", {"start": v(-47.84, -47.57) * mm, "mid": v(-47.95, -47.57) * mm, "end": v(-47.95, -47.68) * mm});
            skLineSegment(sketch, "E1284", {"start": v(-46.88, -48.72) * mm, "end": v(-43.58, -48.72) * mm});
            skArc(sketch, "E1285", {"start": v(-43.58, -48.72) * mm, "mid": v(-43.5, -48.64) * mm, "end": v(-43.58, -48.57) * mm});
            skLineSegment(sketch, "E1286", {"start": v(-43.58, -48.57) * mm, "end": v(-46.88, -48.57) * mm});
            skArc(sketch, "E1287", {"start": v(-46.88, -48.57) * mm, "mid": v(-46.95, -48.64) * mm, "end": v(-46.88, -48.72) * mm});
            skLineSegment(sketch, "E1288", {"start": v(-46.88, -36.53) * mm, "end": v(-43.58, -36.53) * mm});
            skArc(sketch, "E1289", {"start": v(-43.58, -36.53) * mm, "mid": v(-43.5, -36.45) * mm, "end": v(-43.58, -36.38) * mm});
            skLineSegment(sketch, "E1290", {"start": v(-43.58, -36.38) * mm, "end": v(-46.88, -36.38) * mm});
            skArc(sketch, "E1291", {"start": v(-46.88, -36.38) * mm, "mid": v(-46.95, -36.45) * mm, "end": v(-46.88, -36.53) * mm});
            skLineSegment(sketch, "E1292", {"start": v(-46.93, -36.4) * mm, "end": v(-47.95, -37.41) * mm});
            skArc(sketch, "E1293", {"start": v(-47.95, -37.41) * mm, "mid": v(-47.95, -37.52) * mm, "end": v(-47.84, -37.52) * mm});
            skLineSegment(sketch, "E1294", {"start": v(-47.84, -37.52) * mm, "end": v(-46.82, -36.5) * mm});
            skArc(sketch, "E1295", {"start": v(-46.82, -36.5) * mm, "mid": v(-46.82, -36.4) * mm, "end": v(-46.93, -36.4) * mm});
            skLineSegment(sketch, "E1296", {"start": v(-47.97, -37.47) * mm, "end": v(-47.97, -38.74) * mm});
            skArc(sketch, "E1297", {"start": v(-47.97, -38.74) * mm, "mid": v(-47.9, -38.81) * mm, "end": v(-47.82, -38.74) * mm});
            skLineSegment(sketch, "E1298", {"start": v(-47.82, -38.74) * mm, "end": v(-47.82, -37.47) * mm});
            skArc(sketch, "E1299", {"start": v(-47.82, -37.47) * mm, "mid": v(-47.9, -37.4) * mm, "end": v(-47.97, -37.47) * mm});
            skLineSegment(sketch, "E1300", {"start": v(-42.81, -49.1) * mm, "end": v(-40.78, -49.1) * mm});
            skArc(sketch, "E1301", {"start": v(-40.78, -49.1) * mm, "mid": v(-40.7, -49.03) * mm, "end": v(-40.78, -48.95) * mm});
            skLineSegment(sketch, "E1302", {"start": v(-40.78, -48.95) * mm, "end": v(-42.81, -48.95) * mm});
            skArc(sketch, "E1303", {"start": v(-42.81, -48.95) * mm, "mid": v(-42.9, -49.03) * mm, "end": v(-42.81, -49.1) * mm});
            skLineSegment(sketch, "E1304", {"start": v(-42.74, -49.03) * mm, "end": v(-42.74, -48.64) * mm});
            skArc(sketch, "E1305", {"start": v(-42.74, -48.64) * mm, "mid": v(-42.81, -48.57) * mm, "end": v(-42.9, -48.64) * mm});
            skLineSegment(sketch, "E1306", {"start": v(-42.9, -48.64) * mm, "end": v(-42.9, -49.03) * mm});
            skArc(sketch, "E1307", {"start": v(-42.9, -49.03) * mm, "mid": v(-42.81, -49.1) * mm, "end": v(-42.74, -49.03) * mm});
            skLineSegment(sketch, "E1308", {"start": v(-40.86, -48.64) * mm, "end": v(-40.86, -49.03) * mm});
            skArc(sketch, "E1309", {"start": v(-40.86, -49.03) * mm, "mid": v(-40.78, -49.1) * mm, "end": v(-40.7, -49.03) * mm});
            skLineSegment(sketch, "E1310", {"start": v(-40.7, -49.03) * mm, "end": v(-40.7, -48.64) * mm});
            skArc(sketch, "E1311", {"start": v(-40.7, -48.64) * mm, "mid": v(-40.78, -48.57) * mm, "end": v(-40.86, -48.64) * mm});
            skLineSegment(sketch, "E1312", {"start": v(-36.66, -36.4) * mm, "end": v(-36.92, -36.14) * mm});
            skArc(sketch, "E1313", {"start": v(-36.92, -36.14) * mm, "mid": v(-37.03, -36.14) * mm, "end": v(-37.03, -36.25) * mm});
            skLineSegment(sketch, "E1314", {"start": v(-37.03, -36.25) * mm, "end": v(-36.77, -36.5) * mm});
            skArc(sketch, "E1315", {"start": v(-36.77, -36.5) * mm, "mid": v(-36.66, -36.5) * mm, "end": v(-36.66, -36.4) * mm});
            skLineSegment(sketch, "E1316", {"start": v(-36.97, -36.12) * mm, "end": v(-40.02, -36.12) * mm});
            skArc(sketch, "E1317", {"start": v(-40.02, -36.12) * mm, "mid": v(-40.1, -36.2) * mm, "end": v(-40.02, -36.27) * mm});
            skLineSegment(sketch, "E1318", {"start": v(-40.02, -36.27) * mm, "end": v(-36.97, -36.27) * mm});
            skArc(sketch, "E1319", {"start": v(-36.97, -36.27) * mm, "mid": v(-36.9, -36.2) * mm, "end": v(-36.97, -36.12) * mm});
            skLineSegment(sketch, "E1320", {"start": v(-40.1, -36.2) * mm, "end": v(-40.1, -36.45) * mm});
            skArc(sketch, "E1321", {"start": v(-40.1, -36.45) * mm, "mid": v(-40.02, -36.53) * mm, "end": v(-39.94, -36.45) * mm});
            skLineSegment(sketch, "E1322", {"start": v(-39.94, -36.45) * mm, "end": v(-39.94, -36.2) * mm});
            skArc(sketch, "E1323", {"start": v(-39.94, -36.2) * mm, "mid": v(-40.02, -36.12) * mm, "end": v(-40.1, -36.2) * mm});
            skLineSegment(sketch, "E1324", {"start": v(-40.02, -36.38) * mm, "end": v(-40.78, -36.38) * mm});
            skArc(sketch, "E1325", {"start": v(-40.78, -36.38) * mm, "mid": v(-40.86, -36.45) * mm, "end": v(-40.78, -36.53) * mm});
            skLineSegment(sketch, "E1326", {"start": v(-40.78, -36.53) * mm, "end": v(-40.02, -36.53) * mm});
            skArc(sketch, "E1327", {"start": v(-40.02, -36.53) * mm, "mid": v(-39.94, -36.45) * mm, "end": v(-40.02, -36.38) * mm});
            skLineSegment(sketch, "E1328", {"start": v(-43.65, -36.2) * mm, "end": v(-43.65, -36.45) * mm});
            skArc(sketch, "E1329", {"start": v(-43.65, -36.45) * mm, "mid": v(-43.58, -36.53) * mm, "end": v(-43.5, -36.45) * mm});
            skLineSegment(sketch, "E1330", {"start": v(-43.5, -36.45) * mm, "end": v(-43.5, -36.2) * mm});
            skArc(sketch, "E1331", {"start": v(-43.5, -36.2) * mm, "mid": v(-43.58, -36.12) * mm, "end": v(-43.65, -36.2) * mm});
            skLineSegment(sketch, "E1332", {"start": v(-43.58, -36.53) * mm, "end": v(-42.81, -36.53) * mm});
            skArc(sketch, "E1333", {"start": v(-42.81, -36.53) * mm, "mid": v(-42.74, -36.45) * mm, "end": v(-42.81, -36.38) * mm});
            skLineSegment(sketch, "E1334", {"start": v(-42.81, -36.38) * mm, "end": v(-43.58, -36.38) * mm});
            skArc(sketch, "E1335", {"start": v(-43.58, -36.38) * mm, "mid": v(-43.65, -36.45) * mm, "end": v(-43.58, -36.53) * mm});
            skLineSegment(sketch, "E1336", {"start": v(-43.58, -36.12) * mm, "end": v(-46.62, -36.12) * mm});
            skArc(sketch, "E1337", {"start": v(-46.62, -36.12) * mm, "mid": v(-46.7, -36.2) * mm, "end": v(-46.62, -36.27) * mm});
            skLineSegment(sketch, "E1338", {"start": v(-46.62, -36.27) * mm, "end": v(-43.58, -36.27) * mm});
            skArc(sketch, "E1339", {"start": v(-43.58, -36.27) * mm, "mid": v(-43.5, -36.2) * mm, "end": v(-43.58, -36.12) * mm});
            skLineSegment(sketch, "E1340", {"start": v(-46.82, -36.5) * mm, "end": v(-46.57, -36.25) * mm});
            skArc(sketch, "E1341", {"start": v(-46.57, -36.25) * mm, "mid": v(-46.57, -36.14) * mm, "end": v(-46.68, -36.14) * mm});
            skLineSegment(sketch, "E1342", {"start": v(-46.68, -36.14) * mm, "end": v(-46.93, -36.4) * mm});
            skArc(sketch, "E1343", {"start": v(-46.93, -36.4) * mm, "mid": v(-46.93, -36.5) * mm, "end": v(-46.82, -36.5) * mm});
            skLineSegment(sketch, "E1344", {"start": v(-42.81, -48.72) * mm, "end": v(-40.78, -48.72) * mm});
            skArc(sketch, "E1345", {"start": v(-40.78, -48.72) * mm, "mid": v(-40.7, -48.64) * mm, "end": v(-40.78, -48.57) * mm});
            skLineSegment(sketch, "E1346", {"start": v(-40.78, -48.57) * mm, "end": v(-42.81, -48.57) * mm});
            skArc(sketch, "E1347", {"start": v(-42.81, -48.57) * mm, "mid": v(-42.9, -48.64) * mm, "end": v(-42.81, -48.72) * mm});
            skLineSegment(sketch, "E1348", {"start": v(-40.78, -48.72) * mm, "end": v(-40.02, -48.72) * mm});
            skArc(sketch, "E1349", {"start": v(-40.02, -48.72) * mm, "mid": v(-39.94, -48.64) * mm, "end": v(-40.02, -48.57) * mm});
            skLineSegment(sketch, "E1350", {"start": v(-40.02, -48.57) * mm, "end": v(-40.78, -48.57) * mm});
            skArc(sketch, "E1351", {"start": v(-40.78, -48.57) * mm, "mid": v(-40.86, -48.64) * mm, "end": v(-40.78, -48.72) * mm});
            skLineSegment(sketch, "E1352", {"start": v(-43.65, -48.64) * mm, "end": v(-43.65, -48.9) * mm});
            skArc(sketch, "E1353", {"start": v(-43.65, -48.9) * mm, "mid": v(-43.58, -48.97) * mm, "end": v(-43.5, -48.9) * mm});
            skLineSegment(sketch, "E1354", {"start": v(-43.5, -48.9) * mm, "end": v(-43.5, -48.64) * mm});
            skArc(sketch, "E1355", {"start": v(-43.5, -48.64) * mm, "mid": v(-43.58, -48.57) * mm, "end": v(-43.65, -48.64) * mm});
            skLineSegment(sketch, "E1356", {"start": v(-43.58, -48.72) * mm, "end": v(-42.81, -48.72) * mm});
            skArc(sketch, "E1357", {"start": v(-42.81, -48.72) * mm, "mid": v(-42.74, -48.64) * mm, "end": v(-42.81, -48.57) * mm});
            skLineSegment(sketch, "E1358", {"start": v(-42.81, -48.57) * mm, "end": v(-43.58, -48.57) * mm});
            skArc(sketch, "E1359", {"start": v(-43.58, -48.57) * mm, "mid": v(-43.65, -48.64) * mm, "end": v(-43.58, -48.72) * mm});
            skLineSegment(sketch, "E1360", {"start": v(-43.58, -48.82) * mm, "end": v(-46.62, -48.82) * mm});
            skArc(sketch, "E1361", {"start": v(-46.62, -48.82) * mm, "mid": v(-46.7, -48.9) * mm, "end": v(-46.62, -48.97) * mm});
            skLineSegment(sketch, "E1362", {"start": v(-46.62, -48.97) * mm, "end": v(-43.58, -48.97) * mm});
            skArc(sketch, "E1363", {"start": v(-43.58, -48.97) * mm, "mid": v(-43.5, -48.9) * mm, "end": v(-43.58, -48.82) * mm});
            skLineSegment(sketch, "E1364", {"start": v(-46.57, -48.84) * mm, "end": v(-46.82, -48.6) * mm});
            skArc(sketch, "E1365", {"start": v(-46.82, -48.6) * mm, "mid": v(-46.93, -48.6) * mm, "end": v(-46.93, -48.7) * mm});
            skLineSegment(sketch, "E1366", {"start": v(-46.93, -48.7) * mm, "end": v(-46.68, -48.95) * mm});
            skArc(sketch, "E1367", {"start": v(-46.68, -48.95) * mm, "mid": v(-46.57, -48.95) * mm, "end": v(-46.57, -48.84) * mm});
            skLineSegment(sketch, "E1368", {"start": v(-40.1, -48.64) * mm, "end": v(-40.1, -48.9) * mm});
            skArc(sketch, "E1369", {"start": v(-40.1, -48.9) * mm, "mid": v(-40.02, -48.97) * mm, "end": v(-39.94, -48.9) * mm});
            skLineSegment(sketch, "E1370", {"start": v(-39.94, -48.9) * mm, "end": v(-39.94, -48.64) * mm});
            skArc(sketch, "E1371", {"start": v(-39.94, -48.64) * mm, "mid": v(-40.02, -48.57) * mm, "end": v(-40.1, -48.64) * mm});
            skLineSegment(sketch, "E1372", {"start": v(-40.02, -48.72) * mm, "end": v(-36.72, -48.72) * mm});
            skArc(sketch, "E1373", {"start": v(-36.72, -48.72) * mm, "mid": v(-36.64, -48.64) * mm, "end": v(-36.72, -48.57) * mm});
            skLineSegment(sketch, "E1374", {"start": v(-36.72, -48.57) * mm, "end": v(-40.02, -48.57) * mm});
            skArc(sketch, "E1375", {"start": v(-40.02, -48.57) * mm, "mid": v(-40.1, -48.64) * mm, "end": v(-40.02, -48.72) * mm});
            skLineSegment(sketch, "E1376", {"start": v(-36.97, -48.82) * mm, "end": v(-40.02, -48.82) * mm});
            skArc(sketch, "E1377", {"start": v(-40.02, -48.82) * mm, "mid": v(-40.1, -48.9) * mm, "end": v(-40.02, -48.97) * mm});
            skLineSegment(sketch, "E1378", {"start": v(-40.02, -48.97) * mm, "end": v(-36.97, -48.97) * mm});
            skArc(sketch, "E1379", {"start": v(-36.97, -48.97) * mm, "mid": v(-36.9, -48.9) * mm, "end": v(-36.97, -48.82) * mm});
            skLineSegment(sketch, "E1380", {"start": v(-36.77, -48.6) * mm, "end": v(-37.03, -48.84) * mm});
            skArc(sketch, "E1381", {"start": v(-37.03, -48.84) * mm, "mid": v(-37.03, -48.95) * mm, "end": v(-36.92, -48.95) * mm});
            skLineSegment(sketch, "E1382", {"start": v(-36.92, -48.95) * mm, "end": v(-36.66, -48.7) * mm});
            skArc(sketch, "E1383", {"start": v(-36.66, -48.7) * mm, "mid": v(-36.66, -48.6) * mm, "end": v(-36.77, -48.6) * mm});
            skLineSegment(sketch, "E1384", {"start": v(-46.88, -40.08) * mm, "end": v(-46.37, -40.08) * mm});
            skArc(sketch, "E1385", {"start": v(-46.37, -40.08) * mm, "mid": v(-46.3, -40) * mm, "end": v(-46.37, -39.93) * mm});
            skLineSegment(sketch, "E1386", {"start": v(-46.37, -39.93) * mm, "end": v(-46.88, -39.93) * mm});
            skArc(sketch, "E1387", {"start": v(-46.88, -39.93) * mm, "mid": v(-46.95, -40) * mm, "end": v(-46.88, -40.08) * mm});
            skLineSegment(sketch, "E1388", {"start": v(-38.88, -40.08) * mm, "end": v(-36.72, -40.08) * mm});
            skArc(sketch, "E1389", {"start": v(-36.72, -40.08) * mm, "mid": v(-36.64, -40) * mm, "end": v(-36.72, -39.93) * mm});
            skLineSegment(sketch, "E1390", {"start": v(-36.72, -39.93) * mm, "end": v(-38.88, -39.93) * mm});
            skArc(sketch, "E1391", {"start": v(-38.88, -39.93) * mm, "mid": v(-38.95, -40) * mm, "end": v(-38.88, -40.08) * mm});
            skLineSegment(sketch, "E1392", {"start": v(-46.88, -45.16) * mm, "end": v(-46.37, -45.16) * mm});
            skArc(sketch, "E1393", {"start": v(-46.37, -45.16) * mm, "mid": v(-46.3, -45.09) * mm, "end": v(-46.37, -45.01) * mm});
            skLineSegment(sketch, "E1394", {"start": v(-46.37, -45.01) * mm, "end": v(-46.88, -45.01) * mm});
            skArc(sketch, "E1395", {"start": v(-46.88, -45.01) * mm, "mid": v(-46.95, -45.09) * mm, "end": v(-46.88, -45.16) * mm});
            skLineSegment(sketch, "E1396", {"start": v(-38.88, -45.16) * mm, "end": v(-36.72, -45.16) * mm});
            skArc(sketch, "E1397", {"start": v(-36.72, -45.16) * mm, "mid": v(-36.64, -45.09) * mm, "end": v(-36.72, -45.01) * mm});
            skLineSegment(sketch, "E1398", {"start": v(-36.72, -45.01) * mm, "end": v(-38.88, -45.01) * mm});
            skArc(sketch, "E1399", {"start": v(-38.88, -45.01) * mm, "mid": v(-38.95, -45.09) * mm, "end": v(-38.88, -45.16) * mm});
            skLineSegment(sketch, "E1400", {"start": v(-46.45, -40) * mm, "end": v(-46.45, -41.79) * mm});
            skArc(sketch, "E1401", {"start": v(-46.45, -41.79) * mm, "mid": v(-46.37, -41.86) * mm, "end": v(-46.3, -41.79) * mm});
            skLineSegment(sketch, "E1402", {"start": v(-46.3, -41.79) * mm, "end": v(-46.3, -40) * mm});
            skArc(sketch, "E1403", {"start": v(-46.3, -40) * mm, "mid": v(-46.37, -39.93) * mm, "end": v(-46.45, -40) * mm});
            skLineSegment(sketch, "E1404", {"start": v(-46.37, -40.08) * mm, "end": v(-44.72, -40.08) * mm});
            skArc(sketch, "E1405", {"start": v(-44.72, -40.08) * mm, "mid": v(-44.64, -40) * mm, "end": v(-44.72, -39.93) * mm});
            skLineSegment(sketch, "E1406", {"start": v(-44.72, -39.93) * mm, "end": v(-46.37, -39.93) * mm});
            skArc(sketch, "E1407", {"start": v(-46.37, -39.93) * mm, "mid": v(-46.45, -40) * mm, "end": v(-46.37, -40.08) * mm});
            skLineSegment(sketch, "E1408", {"start": v(-46.44, -41.76) * mm, "end": v(-46.95, -43.29) * mm});
            skArc(sketch, "E1409", {"start": v(-46.95, -43.29) * mm, "mid": v(-46.9, -43.38) * mm, "end": v(-46.8, -43.33) * mm});
            skLineSegment(sketch, "E1410", {"start": v(-46.8, -43.33) * mm, "end": v(-46.3, -41.81) * mm});
            skArc(sketch, "E1411", {"start": v(-46.3, -41.81) * mm, "mid": v(-46.35, -41.71) * mm, "end": v(-46.44, -41.76) * mm});
            skLineSegment(sketch, "E1412", {"start": v(-46.45, -43.31) * mm, "end": v(-46.45, -45.09) * mm});
            skArc(sketch, "E1413", {"start": v(-46.45, -45.09) * mm, "mid": v(-46.37, -45.16) * mm, "end": v(-46.3, -45.09) * mm});
            skLineSegment(sketch, "E1414", {"start": v(-46.3, -45.09) * mm, "end": v(-46.3, -43.31) * mm});
            skArc(sketch, "E1415", {"start": v(-46.3, -43.31) * mm, "mid": v(-46.37, -43.23) * mm, "end": v(-46.45, -43.31) * mm});
            skLineSegment(sketch, "E1416", {"start": v(-46.37, -45.16) * mm, "end": v(-44.72, -45.16) * mm});
            skArc(sketch, "E1417", {"start": v(-44.72, -45.16) * mm, "mid": v(-44.64, -45.09) * mm, "end": v(-44.72, -45.01) * mm});
            skLineSegment(sketch, "E1418", {"start": v(-44.72, -45.01) * mm, "end": v(-46.37, -45.01) * mm});
            skArc(sketch, "E1419", {"start": v(-46.37, -45.01) * mm, "mid": v(-46.45, -45.09) * mm, "end": v(-46.37, -45.16) * mm});
            skLineSegment(sketch, "E1420", {"start": v(-47.15, -37.96) * mm, "end": v(-46.77, -37.58) * mm});
            skArc(sketch, "E1421", {"start": v(-46.77, -37.58) * mm, "mid": v(-46.77, -37.49) * mm, "end": v(-46.86, -37.49) * mm});
            skLineSegment(sketch, "E1422", {"start": v(-46.86, -37.49) * mm, "end": v(-47.24, -37.87) * mm});
            skArc(sketch, "E1423", {"start": v(-47.24, -37.87) * mm, "mid": v(-47.24, -37.96) * mm, "end": v(-47.15, -37.96) * mm});
            skLineSegment(sketch, "E1424", {"start": v(-46.88, -37.53) * mm, "end": v(-46.88, -38.67) * mm});
            skArc(sketch, "E1425", {"start": v(-46.88, -38.67) * mm, "mid": v(-46.81, -38.74) * mm, "end": v(-46.75, -38.67) * mm});
            skLineSegment(sketch, "E1426", {"start": v(-46.75, -38.67) * mm, "end": v(-46.75, -37.53) * mm});
            skArc(sketch, "E1427", {"start": v(-46.75, -37.53) * mm, "mid": v(-46.81, -37.47) * mm, "end": v(-46.88, -37.53) * mm});
            skLineSegment(sketch, "E1428", {"start": v(-47.2, -38.74) * mm, "end": v(-46.43, -38.74) * mm});
            skArc(sketch, "E1429", {"start": v(-46.43, -38.74) * mm, "mid": v(-46.37, -38.67) * mm, "end": v(-46.43, -38.61) * mm});
            skLineSegment(sketch, "E1430", {"start": v(-46.43, -38.61) * mm, "end": v(-47.2, -38.61) * mm});
            skArc(sketch, "E1431", {"start": v(-47.2, -38.61) * mm, "mid": v(-47.26, -38.67) * mm, "end": v(-47.2, -38.74) * mm});
            skLineSegment(sketch, "E1432", {"start": v(-36.78, -38.61) * mm, "end": v(-37.54, -38.61) * mm});
            skArc(sketch, "E1433", {"start": v(-37.54, -38.61) * mm, "mid": v(-37.6, -38.67) * mm, "end": v(-37.54, -38.74) * mm});
            skLineSegment(sketch, "E1434", {"start": v(-37.54, -38.74) * mm, "end": v(-36.78, -38.74) * mm});
            skArc(sketch, "E1435", {"start": v(-36.78, -38.74) * mm, "mid": v(-36.72, -38.67) * mm, "end": v(-36.78, -38.61) * mm});
            skLineSegment(sketch, "E1436", {"start": v(-37.5, -38.72) * mm, "end": v(-36.74, -37.96) * mm});
            skArc(sketch, "E1437", {"start": v(-36.74, -37.96) * mm, "mid": v(-36.74, -37.87) * mm, "end": v(-36.83, -37.87) * mm});
            skLineSegment(sketch, "E1438", {"start": v(-36.83, -37.87) * mm, "end": v(-37.59, -38.63) * mm});
            skArc(sketch, "E1439", {"start": v(-37.59, -38.63) * mm, "mid": v(-37.59, -38.72) * mm, "end": v(-37.5, -38.72) * mm});
            skLineSegment(sketch, "E1440", {"start": v(-36.72, -37.91) * mm, "end": v(-36.72, -37.72) * mm});
            skArc(sketch, "E1441", {"start": v(-36.72, -37.72) * mm, "mid": v(-36.78, -37.66) * mm, "end": v(-36.84, -37.72) * mm});
            skLineSegment(sketch, "E1442", {"start": v(-36.84, -37.72) * mm, "end": v(-36.84, -37.91) * mm});
            skArc(sketch, "E1443", {"start": v(-36.84, -37.91) * mm, "mid": v(-36.78, -37.98) * mm, "end": v(-36.72, -37.91) * mm});
            skLineSegment(sketch, "E1444", {"start": v(-36.74, -37.68) * mm, "end": v(-36.93, -37.49) * mm});
            skArc(sketch, "E1445", {"start": v(-36.93, -37.49) * mm, "mid": v(-37.02, -37.49) * mm, "end": v(-37.02, -37.58) * mm});
            skLineSegment(sketch, "E1446", {"start": v(-37.02, -37.58) * mm, "end": v(-36.83, -37.77) * mm});
            skArc(sketch, "E1447", {"start": v(-36.83, -37.77) * mm, "mid": v(-36.74, -37.77) * mm, "end": v(-36.74, -37.68) * mm});
            skLineSegment(sketch, "E1448", {"start": v(-36.97, -37.47) * mm, "end": v(-37.35, -37.47) * mm});
            skArc(sketch, "E1449", {"start": v(-37.35, -37.47) * mm, "mid": v(-37.42, -37.53) * mm, "end": v(-37.35, -37.6) * mm});
            skLineSegment(sketch, "E1450", {"start": v(-37.35, -37.6) * mm, "end": v(-36.97, -37.6) * mm});
            skArc(sketch, "E1451", {"start": v(-36.97, -37.6) * mm, "mid": v(-36.9, -37.53) * mm, "end": v(-36.97, -37.47) * mm});
            skLineSegment(sketch, "E1452", {"start": v(-37.4, -37.49) * mm, "end": v(-37.59, -37.68) * mm});
            skArc(sketch, "E1453", {"start": v(-37.59, -37.68) * mm, "mid": v(-37.59, -37.77) * mm, "end": v(-37.5, -37.77) * mm});
            skLineSegment(sketch, "E1454", {"start": v(-37.5, -37.77) * mm, "end": v(-37.3, -37.58) * mm});
            skArc(sketch, "E1455", {"start": v(-37.3, -37.58) * mm, "mid": v(-37.3, -37.49) * mm, "end": v(-37.4, -37.49) * mm});
            skLineSegment(sketch, "E1456", {"start": v(-47.15, -46.66) * mm, "end": v(-46.96, -46.47) * mm});
            skArc(sketch, "E1457", {"start": v(-46.96, -46.47) * mm, "mid": v(-46.96, -46.38) * mm, "end": v(-47.05, -46.38) * mm});
            skLineSegment(sketch, "E1458", {"start": v(-47.05, -46.38) * mm, "end": v(-47.24, -46.57) * mm});
            skArc(sketch, "E1459", {"start": v(-47.24, -46.57) * mm, "mid": v(-47.24, -46.66) * mm, "end": v(-47.15, -46.66) * mm});
            skLineSegment(sketch, "E1460", {"start": v(-47, -46.48) * mm, "end": v(-46.62, -46.48) * mm});
            skArc(sketch, "E1461", {"start": v(-46.62, -46.48) * mm, "mid": v(-46.56, -46.42) * mm, "end": v(-46.62, -46.36) * mm});
            skLineSegment(sketch, "E1462", {"start": v(-46.62, -46.36) * mm, "end": v(-47, -46.36) * mm});
            skArc(sketch, "E1463", {"start": v(-47, -46.36) * mm, "mid": v(-47.07, -46.42) * mm, "end": v(-47, -46.48) * mm});
            skLineSegment(sketch, "E1464", {"start": v(-46.67, -46.47) * mm, "end": v(-46.48, -46.66) * mm});
            skArc(sketch, "E1465", {"start": v(-46.48, -46.66) * mm, "mid": v(-46.39, -46.66) * mm, "end": v(-46.39, -46.57) * mm});
            skLineSegment(sketch, "E1466", {"start": v(-46.39, -46.57) * mm, "end": v(-46.58, -46.38) * mm});
            skArc(sketch, "E1467", {"start": v(-46.58, -46.38) * mm, "mid": v(-46.67, -46.38) * mm, "end": v(-46.67, -46.47) * mm});
            skLineSegment(sketch, "E1468", {"start": v(-46.5, -46.61) * mm, "end": v(-46.5, -46.8) * mm});
            skArc(sketch, "E1469", {"start": v(-46.5, -46.8) * mm, "mid": v(-46.43, -46.87) * mm, "end": v(-46.37, -46.8) * mm});
            skLineSegment(sketch, "E1470", {"start": v(-46.37, -46.8) * mm, "end": v(-46.37, -46.61) * mm});
            skArc(sketch, "E1471", {"start": v(-46.37, -46.61) * mm, "mid": v(-46.43, -46.55) * mm, "end": v(-46.5, -46.61) * mm});
            skLineSegment(sketch, "E1472", {"start": v(-46.48, -46.76) * mm, "end": v(-46.67, -46.95) * mm});
            skArc(sketch, "E1473", {"start": v(-46.67, -46.95) * mm, "mid": v(-46.67, -47.04) * mm, "end": v(-46.58, -47.04) * mm});
            skLineSegment(sketch, "E1474", {"start": v(-46.58, -47.04) * mm, "end": v(-46.39, -46.85) * mm});
            skArc(sketch, "E1475", {"start": v(-46.39, -46.85) * mm, "mid": v(-46.39, -46.76) * mm, "end": v(-46.48, -46.76) * mm});
            skLineSegment(sketch, "E1476", {"start": v(-46.62, -46.93) * mm, "end": v(-46.81, -46.93) * mm});
            skArc(sketch, "E1477", {"start": v(-46.81, -46.93) * mm, "mid": v(-46.88, -47) * mm, "end": v(-46.81, -47.06) * mm});
            skLineSegment(sketch, "E1478", {"start": v(-46.81, -47.06) * mm, "end": v(-46.62, -47.06) * mm});
            skArc(sketch, "E1479", {"start": v(-46.62, -47.06) * mm, "mid": v(-46.56, -47) * mm, "end": v(-46.62, -46.93) * mm});
            skLineSegment(sketch, "E1480", {"start": v(-46.67, -47.04) * mm, "end": v(-46.48, -47.23) * mm});
            skArc(sketch, "E1481", {"start": v(-46.48, -47.23) * mm, "mid": v(-46.39, -47.23) * mm, "end": v(-46.39, -47.14) * mm});
            skLineSegment(sketch, "E1482", {"start": v(-46.39, -47.14) * mm, "end": v(-46.58, -46.95) * mm});
            skArc(sketch, "E1483", {"start": v(-46.58, -46.95) * mm, "mid": v(-46.67, -46.95) * mm, "end": v(-46.67, -47.04) * mm});
            skLineSegment(sketch, "E1484", {"start": v(-46.5, -47.18) * mm, "end": v(-46.5, -47.37) * mm});
            skArc(sketch, "E1485", {"start": v(-46.5, -47.37) * mm, "mid": v(-46.43, -47.44) * mm, "end": v(-46.37, -47.37) * mm});
            skLineSegment(sketch, "E1486", {"start": v(-46.37, -47.37) * mm, "end": v(-46.37, -47.18) * mm});
            skArc(sketch, "E1487", {"start": v(-46.37, -47.18) * mm, "mid": v(-46.43, -47.12) * mm, "end": v(-46.5, -47.18) * mm});
            skLineSegment(sketch, "E1488", {"start": v(-46.48, -47.33) * mm, "end": v(-46.67, -47.52) * mm});
            skArc(sketch, "E1489", {"start": v(-46.67, -47.52) * mm, "mid": v(-46.67, -47.6) * mm, "end": v(-46.58, -47.6) * mm});
            skLineSegment(sketch, "E1490", {"start": v(-46.58, -47.6) * mm, "end": v(-46.39, -47.42) * mm});
            skArc(sketch, "E1491", {"start": v(-46.39, -47.42) * mm, "mid": v(-46.39, -47.33) * mm, "end": v(-46.48, -47.33) * mm});
            skLineSegment(sketch, "E1492", {"start": v(-46.62, -47.5) * mm, "end": v(-47, -47.5) * mm});
            skArc(sketch, "E1493", {"start": v(-47, -47.5) * mm, "mid": v(-47.07, -47.56) * mm, "end": v(-47, -47.63) * mm});
            skLineSegment(sketch, "E1494", {"start": v(-47, -47.63) * mm, "end": v(-46.62, -47.63) * mm});
            skArc(sketch, "E1495", {"start": v(-46.62, -47.63) * mm, "mid": v(-46.56, -47.56) * mm, "end": v(-46.62, -47.5) * mm});
            skLineSegment(sketch, "E1496", {"start": v(-46.96, -47.52) * mm, "end": v(-47.15, -47.33) * mm});
            skArc(sketch, "E1497", {"start": v(-47.15, -47.33) * mm, "mid": v(-47.24, -47.33) * mm, "end": v(-47.24, -47.42) * mm});
            skLineSegment(sketch, "E1498", {"start": v(-47.24, -47.42) * mm, "end": v(-47.05, -47.6) * mm});
            skArc(sketch, "E1499", {"start": v(-47.05, -47.6) * mm, "mid": v(-46.96, -47.6) * mm, "end": v(-46.96, -47.52) * mm});
            skLineSegment(sketch, "E1500", {"start": v(-36.78, -47.56) * mm, "end": v(-36.78, -46.42) * mm});
            skArc(sketch, "E1501", {"start": v(-36.78, -46.42) * mm, "mid": v(-36.84, -46.36) * mm, "end": v(-36.9, -46.42) * mm});
            skLineSegment(sketch, "E1502", {"start": v(-36.9, -46.42) * mm, "end": v(-36.9, -47.56) * mm});
            skArc(sketch, "E1503", {"start": v(-36.9, -47.56) * mm, "mid": v(-36.84, -47.63) * mm, "end": v(-36.78, -47.56) * mm});
            skLineSegment(sketch, "E1504", {"start": v(-36.89, -46.38) * mm, "end": v(-37.46, -46.95) * mm});
            skArc(sketch, "E1505", {"start": v(-37.46, -46.95) * mm, "mid": v(-37.46, -47.04) * mm, "end": v(-37.37, -47.04) * mm});
            skLineSegment(sketch, "E1506", {"start": v(-37.37, -47.04) * mm, "end": v(-36.8, -46.47) * mm});
            skArc(sketch, "E1507", {"start": v(-36.8, -46.47) * mm, "mid": v(-36.8, -46.38) * mm, "end": v(-36.89, -46.38) * mm});
            skLineSegment(sketch, "E1508", {"start": v(-37.42, -47.06) * mm, "end": v(-36.65, -47.06) * mm});
            skArc(sketch, "E1509", {"start": v(-36.65, -47.06) * mm, "mid": v(-36.6, -47) * mm, "end": v(-36.65, -46.93) * mm});
            skLineSegment(sketch, "E1510", {"start": v(-36.65, -46.93) * mm, "end": v(-37.42, -46.93) * mm});
            skArc(sketch, "E1511", {"start": v(-37.42, -46.93) * mm, "mid": v(-37.48, -47) * mm, "end": v(-37.42, -47.06) * mm});
            skCircle(sketch, "E1512", {"center": v(-41.8, -42.55) * mm, "radius": 3.48 * mm});
            skCircle(sketch, "E1513", {"center": v(-41.8, -42.55) * mm, "radius": 3.63 * mm});
            skCircle(sketch, "E1514", {"center": v(-41.8, -42.55) * mm, "radius": 1 * mm});
            skCircle(sketch, "E1515", {"center": v(-41.8, -42.55) * mm, "radius": 1.04 * mm});
            skCircle(sketch, "E1516", {"center": v(-41.8, -42.55) * mm, "radius": 0.74 * mm});
            skCircle(sketch, "E1517", {"center": v(-41.8, -42.55) * mm, "radius": 0.79 * mm});
            skCircle(sketch, "E1518", {"center": v(-46.37, -40) * mm, "radius": 0.05 * mm});
            skCircle(sketch, "E1519", {"center": v(-46.37, -40) * mm, "radius": 0.2 * mm});
            skCircle(sketch, "E1520", {"center": v(-46.37, -45.09) * mm, "radius": 0.05 * mm});
            skCircle(sketch, "E1521", {"center": v(-46.37, -45.09) * mm, "radius": 0.2 * mm});
            skLineSegment(sketch, "E1522", {"start": v(-48.94, -40.95) * mm, "end": v(-47.15, -40.95) * mm});
            skArc(sketch, "E1523", {"start": v(-47.15, -40.56) * mm, "mid": v(-46.65, -40.06) * mm, "end": v(-47.15, -39.56) * mm});
            skLineSegment(sketch, "E1524", {"start": v(-47.15, -39.16) * mm, "end": v(-48.94, -39.16) * mm});
            skArc(sketch, "E1525", {"start": v(-48.94, -39.56) * mm, "mid": v(-49.44, -40.06) * mm, "end": v(-48.94, -40.56) * mm});
            skLineSegment(sketch, "E1526", {"start": v(-36.45, -40.95) * mm, "end": v(-34.65, -40.95) * mm});
            skArc(sketch, "E1527", {"start": v(-34.65, -40.56) * mm, "mid": v(-34.15, -40.06) * mm, "end": v(-34.65, -39.56) * mm});
            skLineSegment(sketch, "E1528", {"start": v(-34.65, -39.16) * mm, "end": v(-36.45, -39.16) * mm});
            skArc(sketch, "E1529", {"start": v(-36.45, -39.56) * mm, "mid": v(-36.95, -40.06) * mm, "end": v(-36.45, -40.56) * mm});
            skLineSegment(sketch, "E1530", {"start": v(-48.94, -45.93) * mm, "end": v(-47.15, -45.93) * mm});
            skArc(sketch, "E1531", {"start": v(-47.15, -45.54) * mm, "mid": v(-46.65, -45.04) * mm, "end": v(-47.15, -44.54) * mm});
            skLineSegment(sketch, "E1532", {"start": v(-47.15, -44.14) * mm, "end": v(-48.94, -44.14) * mm});
            skArc(sketch, "E1533", {"start": v(-48.94, -44.54) * mm, "mid": v(-49.44, -45.04) * mm, "end": v(-48.94, -45.54) * mm});
            skLineSegment(sketch, "E1534", {"start": v(-36.45, -45.93) * mm, "end": v(-34.65, -45.93) * mm});
            skArc(sketch, "E1535", {"start": v(-34.65, -45.54) * mm, "mid": v(-34.15, -45.04) * mm, "end": v(-34.65, -44.54) * mm});
            skLineSegment(sketch, "E1536", {"start": v(-34.65, -44.14) * mm, "end": v(-36.45, -44.14) * mm});
            skArc(sketch, "E1537", {"start": v(-36.45, -44.54) * mm, "mid": v(-36.95, -45.04) * mm, "end": v(-36.45, -45.54) * mm});
            skLineSegment(sketch, "E1538", {"start": v(-28.24, -32.88) * mm, "end": v(-28.24, -32.63) * mm});
            skArc(sketch, "E1539", {"start": v(-28.24, -32.63) * mm, "mid": v(-28.32, -32.55) * mm, "end": v(-28.4, -32.63) * mm});
            skLineSegment(sketch, "E1540", {"start": v(-28.4, -32.63) * mm, "end": v(-28.4, -32.88) * mm});
            skArc(sketch, "E1541", {"start": v(-28.4, -32.88) * mm, "mid": v(-28.32, -32.96) * mm, "end": v(-28.24, -32.88) * mm});
            skLineSegment(sketch, "E1542", {"start": v(-28.32, -32.96) * mm, "end": v(-26.8, -32.96) * mm});
            skArc(sketch, "E1543", {"start": v(-26.8, -32.96) * mm, "mid": v(-26.72, -32.88) * mm, "end": v(-26.8, -32.8) * mm});
            skLineSegment(sketch, "E1544", {"start": v(-26.8, -32.8) * mm, "end": v(-28.32, -32.8) * mm});
            skArc(sketch, "E1545", {"start": v(-28.32, -32.8) * mm, "mid": v(-28.4, -32.88) * mm, "end": v(-28.32, -32.96) * mm});
            skLineSegment(sketch, "E1546", {"start": v(-26.87, -32.63) * mm, "end": v(-26.87, -32.88) * mm});
            skArc(sketch, "E1547", {"start": v(-26.87, -32.88) * mm, "mid": v(-26.8, -32.96) * mm, "end": v(-26.72, -32.88) * mm});
            skLineSegment(sketch, "E1548", {"start": v(-26.72, -32.88) * mm, "end": v(-26.72, -32.63) * mm});
            skArc(sketch, "E1549", {"start": v(-26.72, -32.63) * mm, "mid": v(-26.8, -32.55) * mm, "end": v(-26.87, -32.63) * mm});
            skLineSegment(sketch, "E1550", {"start": v(-26.54, -32.7) * mm, "end": v(-25.02, -32.7) * mm});
            skArc(sketch, "E1551", {"start": v(-25.02, -32.7) * mm, "mid": v(-24.94, -32.63) * mm, "end": v(-25.02, -32.55) * mm});
            skLineSegment(sketch, "E1552", {"start": v(-25.02, -32.55) * mm, "end": v(-26.54, -32.55) * mm});
            skArc(sketch, "E1553", {"start": v(-26.54, -32.55) * mm, "mid": v(-26.62, -32.63) * mm, "end": v(-26.54, -32.7) * mm});
            skLineSegment(sketch, "E1554", {"start": v(-26.87, -26.28) * mm, "end": v(-26.87, -26.53) * mm});
            skArc(sketch, "E1555", {"start": v(-26.87, -26.53) * mm, "mid": v(-26.8, -26.6) * mm, "end": v(-26.72, -26.53) * mm});
            skLineSegment(sketch, "E1556", {"start": v(-26.72, -26.53) * mm, "end": v(-26.72, -26.28) * mm});
            skArc(sketch, "E1557", {"start": v(-26.72, -26.28) * mm, "mid": v(-26.8, -26.2) * mm, "end": v(-26.87, -26.28) * mm});
            skLineSegment(sketch, "E1558", {"start": v(-26.8, -26.2) * mm, "end": v(-28.32, -26.2) * mm});
            skArc(sketch, "E1559", {"start": v(-28.32, -26.2) * mm, "mid": v(-28.4, -26.28) * mm, "end": v(-28.32, -26.35) * mm});
            skLineSegment(sketch, "E1560", {"start": v(-28.32, -26.35) * mm, "end": v(-26.8, -26.35) * mm});
            skArc(sketch, "E1561", {"start": v(-26.8, -26.35) * mm, "mid": v(-26.72, -26.28) * mm, "end": v(-26.8, -26.2) * mm});
            skLineSegment(sketch, "E1562", {"start": v(-28.24, -26.53) * mm, "end": v(-28.24, -26.28) * mm});
            skArc(sketch, "E1563", {"start": v(-28.24, -26.28) * mm, "mid": v(-28.32, -26.2) * mm, "end": v(-28.4, -26.28) * mm});
            skLineSegment(sketch, "E1564", {"start": v(-28.4, -26.28) * mm, "end": v(-28.4, -26.53) * mm});
            skArc(sketch, "E1565", {"start": v(-28.4, -26.53) * mm, "mid": v(-28.32, -26.6) * mm, "end": v(-28.24, -26.53) * mm});
            skLineSegment(sketch, "E1566", {"start": v(-24.96, -32.68) * mm, "end": v(-24.46, -32.17) * mm});
            skArc(sketch, "E1567", {"start": v(-24.46, -32.17) * mm, "mid": v(-24.46, -32.06) * mm, "end": v(-24.56, -32.06) * mm});
            skLineSegment(sketch, "E1568", {"start": v(-24.56, -32.06) * mm, "end": v(-25.07, -32.57) * mm});
            skArc(sketch, "E1569", {"start": v(-25.07, -32.57) * mm, "mid": v(-25.07, -32.68) * mm, "end": v(-24.96, -32.68) * mm});
            skLineSegment(sketch, "E1570", {"start": v(-30.66, -32.17) * mm, "end": v(-30.15, -32.68) * mm});
            skArc(sketch, "E1571", {"start": v(-30.15, -32.68) * mm, "mid": v(-30.04, -32.68) * mm, "end": v(-30.04, -32.57) * mm});
            skLineSegment(sketch, "E1572", {"start": v(-30.04, -32.57) * mm, "end": v(-30.55, -32.06) * mm});
            skArc(sketch, "E1573", {"start": v(-30.55, -32.06) * mm, "mid": v(-30.66, -32.06) * mm, "end": v(-30.66, -32.17) * mm});
            skLineSegment(sketch, "E1574", {"start": v(-30.1, -32.7) * mm, "end": v(-28.57, -32.7) * mm});
            skArc(sketch, "E1575", {"start": v(-28.57, -32.7) * mm, "mid": v(-28.5, -32.63) * mm, "end": v(-28.57, -32.55) * mm});
            skLineSegment(sketch, "E1576", {"start": v(-28.57, -32.55) * mm, "end": v(-30.1, -32.55) * mm});
            skArc(sketch, "E1577", {"start": v(-30.1, -32.55) * mm, "mid": v(-30.17, -32.63) * mm, "end": v(-30.1, -32.7) * mm});
            skLineSegment(sketch, "E1578", {"start": v(-24.46, -26.98) * mm, "end": v(-24.96, -26.48) * mm});
            skArc(sketch, "E1579", {"start": v(-24.96, -26.48) * mm, "mid": v(-25.07, -26.48) * mm, "end": v(-25.07, -26.58) * mm});
            skLineSegment(sketch, "E1580", {"start": v(-25.07, -26.58) * mm, "end": v(-24.56, -27.1) * mm});
            skArc(sketch, "E1581", {"start": v(-24.56, -27.1) * mm, "mid": v(-24.46, -27.1) * mm, "end": v(-24.46, -26.98) * mm});
            skLineSegment(sketch, "E1582", {"start": v(-25.02, -26.45) * mm, "end": v(-26.54, -26.45) * mm});
            skArc(sketch, "E1583", {"start": v(-26.54, -26.45) * mm, "mid": v(-26.62, -26.53) * mm, "end": v(-26.54, -26.6) * mm});
            skLineSegment(sketch, "E1584", {"start": v(-26.54, -26.6) * mm, "end": v(-25.02, -26.6) * mm});
            skArc(sketch, "E1585", {"start": v(-25.02, -26.6) * mm, "mid": v(-24.94, -26.53) * mm, "end": v(-25.02, -26.45) * mm});
            skLineSegment(sketch, "E1586", {"start": v(-30.55, -27.1) * mm, "end": v(-30.04, -26.58) * mm});
            skArc(sketch, "E1587", {"start": v(-30.04, -26.58) * mm, "mid": v(-30.04, -26.48) * mm, "end": v(-30.15, -26.48) * mm});
            skLineSegment(sketch, "E1588", {"start": v(-30.15, -26.48) * mm, "end": v(-30.66, -26.98) * mm});
            skArc(sketch, "E1589", {"start": v(-30.66, -26.98) * mm, "mid": v(-30.66, -27.1) * mm, "end": v(-30.55, -27.1) * mm});
            skLineSegment(sketch, "E1590", {"start": v(-30.1, -26.6) * mm, "end": v(-28.57, -26.6) * mm});
            skArc(sketch, "E1591", {"start": v(-28.57, -26.6) * mm, "mid": v(-28.5, -26.53) * mm, "end": v(-28.57, -26.45) * mm});
            skLineSegment(sketch, "E1592", {"start": v(-28.57, -26.45) * mm, "end": v(-30.1, -26.45) * mm});
            skArc(sketch, "E1593", {"start": v(-30.1, -26.45) * mm, "mid": v(-30.17, -26.53) * mm, "end": v(-30.1, -26.6) * mm});
            skLineSegment(sketch, "E1594", {"start": v(-26.29, -28.28) * mm, "end": v(-28.83, -28.28) * mm});
            skArc(sketch, "E1595", {"start": v(-28.83, -28.28) * mm, "mid": v(-28.85, -28.3) * mm, "end": v(-28.83, -28.33) * mm});
            skLineSegment(sketch, "E1596", {"start": v(-28.83, -28.33) * mm, "end": v(-26.29, -28.33) * mm});
            skArc(sketch, "E1597", {"start": v(-26.29, -28.33) * mm, "mid": v(-26.26, -28.3) * mm, "end": v(-26.29, -28.28) * mm});
            skLineSegment(sketch, "E1598", {"start": v(-28.8, -30.85) * mm, "end": v(-28.8, -28.3) * mm});
            skArc(sketch, "E1599", {"start": v(-28.8, -28.3) * mm, "mid": v(-28.83, -28.28) * mm, "end": v(-28.85, -28.3) * mm});
            skLineSegment(sketch, "E1600", {"start": v(-28.85, -28.3) * mm, "end": v(-28.85, -30.85) * mm});
            skArc(sketch, "E1601", {"start": v(-28.85, -30.85) * mm, "mid": v(-28.83, -30.87) * mm, "end": v(-28.8, -30.85) * mm});
            skLineSegment(sketch, "E1602", {"start": v(-28.83, -30.87) * mm, "end": v(-26.29, -30.87) * mm});
            skArc(sketch, "E1603", {"start": v(-26.29, -30.87) * mm, "mid": v(-26.26, -30.85) * mm, "end": v(-26.29, -30.82) * mm});
            skLineSegment(sketch, "E1604", {"start": v(-26.29, -30.82) * mm, "end": v(-28.83, -30.82) * mm});
            skArc(sketch, "E1605", {"start": v(-28.83, -30.82) * mm, "mid": v(-28.85, -30.85) * mm, "end": v(-28.83, -30.87) * mm});
            skLineSegment(sketch, "E1606", {"start": v(-26.31, -28.3) * mm, "end": v(-26.31, -30.85) * mm});
            skArc(sketch, "E1607", {"start": v(-26.31, -30.85) * mm, "mid": v(-26.29, -30.87) * mm, "end": v(-26.26, -30.85) * mm});
            skLineSegment(sketch, "E1608", {"start": v(-26.26, -30.85) * mm, "end": v(-26.26, -28.3) * mm});
            skArc(sketch, "E1609", {"start": v(-26.26, -28.3) * mm, "mid": v(-26.29, -28.28) * mm, "end": v(-26.31, -28.3) * mm});
            skLineSegment(sketch, "E1610", {"start": v(-24.51, -28.28) * mm, "end": v(-24.76, -28.28) * mm});
            skArc(sketch, "E1611", {"start": v(-24.76, -28.28) * mm, "mid": v(-24.79, -28.3) * mm, "end": v(-24.76, -28.33) * mm});
            skLineSegment(sketch, "E1612", {"start": v(-24.76, -28.33) * mm, "end": v(-24.51, -28.33) * mm});
            skArc(sketch, "E1613", {"start": v(-24.51, -28.33) * mm, "mid": v(-24.48, -28.3) * mm, "end": v(-24.51, -28.28) * mm});
            skLineSegment(sketch, "E1614", {"start": v(-24.74, -30.85) * mm, "end": v(-24.74, -28.3) * mm});
            skArc(sketch, "E1615", {"start": v(-24.74, -28.3) * mm, "mid": v(-24.76, -28.28) * mm, "end": v(-24.79, -28.3) * mm});
            skLineSegment(sketch, "E1616", {"start": v(-24.79, -28.3) * mm, "end": v(-24.79, -30.85) * mm});
            skArc(sketch, "E1617", {"start": v(-24.79, -30.85) * mm, "mid": v(-24.76, -30.87) * mm, "end": v(-24.74, -30.85) * mm});
            skLineSegment(sketch, "E1618", {"start": v(-24.76, -30.87) * mm, "end": v(-24.51, -30.87) * mm});
            skArc(sketch, "E1619", {"start": v(-24.51, -30.87) * mm, "mid": v(-24.48, -30.85) * mm, "end": v(-24.51, -30.82) * mm});
            skLineSegment(sketch, "E1620", {"start": v(-24.51, -30.82) * mm, "end": v(-24.76, -30.82) * mm});
            skArc(sketch, "E1621", {"start": v(-24.76, -30.82) * mm, "mid": v(-24.79, -30.85) * mm, "end": v(-24.76, -30.87) * mm});
            skLineSegment(sketch, "E1622", {"start": v(-30.33, -30.72) * mm, "end": v(-30.33, -28.3) * mm});
            skArc(sketch, "E1623", {"start": v(-30.33, -28.3) * mm, "mid": v(-30.35, -28.28) * mm, "end": v(-30.38, -28.3) * mm});
            skLineSegment(sketch, "E1624", {"start": v(-30.38, -28.3) * mm, "end": v(-30.38, -30.72) * mm});
            skArc(sketch, "E1625", {"start": v(-30.38, -30.72) * mm, "mid": v(-30.35, -30.75) * mm, "end": v(-30.33, -30.72) * mm});
            skLineSegment(sketch, "E1626", {"start": v(-30.35, -30.7) * mm, "end": v(-30.6, -30.7) * mm});
            skArc(sketch, "E1627", {"start": v(-30.6, -30.7) * mm, "mid": v(-30.63, -30.72) * mm, "end": v(-30.6, -30.75) * mm});
            skLineSegment(sketch, "E1628", {"start": v(-30.6, -30.75) * mm, "end": v(-30.35, -30.75) * mm});
            skArc(sketch, "E1629", {"start": v(-30.35, -30.75) * mm, "mid": v(-30.33, -30.72) * mm, "end": v(-30.35, -30.7) * mm});
            skLineSegment(sketch, "E1630", {"start": v(-30.35, -28.28) * mm, "end": v(-30.6, -28.28) * mm});
            skArc(sketch, "E1631", {"start": v(-30.6, -28.28) * mm, "mid": v(-30.63, -28.3) * mm, "end": v(-30.6, -28.33) * mm});
            skLineSegment(sketch, "E1632", {"start": v(-30.6, -28.33) * mm, "end": v(-30.35, -28.33) * mm});
            skArc(sketch, "E1633", {"start": v(-30.35, -28.33) * mm, "mid": v(-30.33, -28.3) * mm, "end": v(-30.35, -28.28) * mm});
            skLineSegment(sketch, "E1634", {"start": v(-30.53, -32.12) * mm, "end": v(-30.53, -31.74) * mm});
            skArc(sketch, "E1635", {"start": v(-30.53, -31.74) * mm, "mid": v(-30.6, -31.66) * mm, "end": v(-30.68, -31.74) * mm});
            skLineSegment(sketch, "E1636", {"start": v(-30.68, -31.74) * mm, "end": v(-30.68, -32.12) * mm});
            skArc(sketch, "E1637", {"start": v(-30.68, -32.12) * mm, "mid": v(-30.6, -32.2) * mm, "end": v(-30.53, -32.12) * mm});
            skLineSegment(sketch, "E1638", {"start": v(-30.68, -27.04) * mm, "end": v(-30.68, -27.42) * mm});
            skArc(sketch, "E1639", {"start": v(-30.68, -27.42) * mm, "mid": v(-30.6, -27.5) * mm, "end": v(-30.53, -27.42) * mm});
            skLineSegment(sketch, "E1640", {"start": v(-30.53, -27.42) * mm, "end": v(-30.53, -27.04) * mm});
            skArc(sketch, "E1641", {"start": v(-30.53, -27.04) * mm, "mid": v(-30.6, -26.96) * mm, "end": v(-30.68, -27.04) * mm});
            skLineSegment(sketch, "E1642", {"start": v(-30.68, -27.42) * mm, "end": v(-30.68, -28.3) * mm});
            skArc(sketch, "E1643", {"start": v(-30.68, -28.3) * mm, "mid": v(-30.6, -28.38) * mm, "end": v(-30.53, -28.3) * mm});
            skLineSegment(sketch, "E1644", {"start": v(-30.53, -28.3) * mm, "end": v(-30.53, -27.42) * mm});
            skArc(sketch, "E1645", {"start": v(-30.53, -27.42) * mm, "mid": v(-30.6, -27.34) * mm, "end": v(-30.68, -27.42) * mm});
            skLineSegment(sketch, "E1646", {"start": v(-24.59, -27.04) * mm, "end": v(-24.59, -27.42) * mm});
            skArc(sketch, "E1647", {"start": v(-24.59, -27.42) * mm, "mid": v(-24.51, -27.5) * mm, "end": v(-24.43, -27.42) * mm});
            skLineSegment(sketch, "E1648", {"start": v(-24.43, -27.42) * mm, "end": v(-24.43, -27.04) * mm});
            skArc(sketch, "E1649", {"start": v(-24.43, -27.04) * mm, "mid": v(-24.51, -26.96) * mm, "end": v(-24.59, -27.04) * mm});
            skLineSegment(sketch, "E1650", {"start": v(-24.43, -32.12) * mm, "end": v(-24.43, -31.74) * mm});
            skArc(sketch, "E1651", {"start": v(-24.43, -31.74) * mm, "mid": v(-24.51, -31.66) * mm, "end": v(-24.59, -31.74) * mm});
            skLineSegment(sketch, "E1652", {"start": v(-24.59, -31.74) * mm, "end": v(-24.59, -32.12) * mm});
            skArc(sketch, "E1653", {"start": v(-24.59, -32.12) * mm, "mid": v(-24.51, -32.2) * mm, "end": v(-24.43, -32.12) * mm});
            skLineSegment(sketch, "E1654", {"start": v(-24.43, -31.74) * mm, "end": v(-24.43, -30.85) * mm});
            skArc(sketch, "E1655", {"start": v(-24.43, -30.85) * mm, "mid": v(-24.51, -30.77) * mm, "end": v(-24.59, -30.85) * mm});
            skLineSegment(sketch, "E1656", {"start": v(-24.59, -30.85) * mm, "end": v(-24.59, -31.74) * mm});
            skArc(sketch, "E1657", {"start": v(-24.59, -31.74) * mm, "mid": v(-24.51, -31.81) * mm, "end": v(-24.43, -31.74) * mm});
            skLineSegment(sketch, "E1658", {"start": v(-24.43, -30.85) * mm, "end": v(-24.43, -28.3) * mm});
            skArc(sketch, "E1659", {"start": v(-24.43, -28.3) * mm, "mid": v(-24.51, -28.23) * mm, "end": v(-24.59, -28.3) * mm});
            skLineSegment(sketch, "E1660", {"start": v(-24.59, -28.3) * mm, "end": v(-24.59, -30.85) * mm});
            skArc(sketch, "E1661", {"start": v(-24.59, -30.85) * mm, "mid": v(-24.51, -30.92) * mm, "end": v(-24.43, -30.85) * mm});
            skLineSegment(sketch, "E1662", {"start": v(-24.43, -28.3) * mm, "end": v(-24.43, -27.42) * mm});
            skArc(sketch, "E1663", {"start": v(-24.43, -27.42) * mm, "mid": v(-24.51, -27.34) * mm, "end": v(-24.59, -27.42) * mm});
            skLineSegment(sketch, "E1664", {"start": v(-24.59, -27.42) * mm, "end": v(-24.59, -28.3) * mm});
            skArc(sketch, "E1665", {"start": v(-24.59, -28.3) * mm, "mid": v(-24.51, -28.38) * mm, "end": v(-24.43, -28.3) * mm});
            skLineSegment(sketch, "E1666", {"start": v(-30.68, -28.3) * mm, "end": v(-30.68, -30.72) * mm});
            skArc(sketch, "E1667", {"start": v(-30.68, -30.72) * mm, "mid": v(-30.6, -30.8) * mm, "end": v(-30.53, -30.72) * mm});
            skLineSegment(sketch, "E1668", {"start": v(-30.53, -30.72) * mm, "end": v(-30.53, -28.3) * mm});
            skArc(sketch, "E1669", {"start": v(-30.53, -28.3) * mm, "mid": v(-30.6, -28.23) * mm, "end": v(-30.68, -28.3) * mm});
            skLineSegment(sketch, "E1670", {"start": v(-30.68, -30.72) * mm, "end": v(-30.68, -31.74) * mm});
            skArc(sketch, "E1671", {"start": v(-30.68, -31.74) * mm, "mid": v(-30.6, -31.81) * mm, "end": v(-30.53, -31.74) * mm});
            skLineSegment(sketch, "E1672", {"start": v(-30.53, -31.74) * mm, "end": v(-30.53, -30.72) * mm});
            skArc(sketch, "E1673", {"start": v(-30.53, -30.72) * mm, "mid": v(-30.6, -30.65) * mm, "end": v(-30.68, -30.72) * mm});
            skLineSegment(sketch, "E1674", {"start": v(-28.32, -32.55) * mm, "end": v(-28.57, -32.55) * mm});
            skArc(sketch, "E1675", {"start": v(-28.57, -32.55) * mm, "mid": v(-28.65, -32.63) * mm, "end": v(-28.57, -32.7) * mm});
            skLineSegment(sketch, "E1676", {"start": v(-28.57, -32.7) * mm, "end": v(-28.32, -32.7) * mm});
            skArc(sketch, "E1677", {"start": v(-28.32, -32.7) * mm, "mid": v(-28.24, -32.63) * mm, "end": v(-28.32, -32.55) * mm});
            skLineSegment(sketch, "E1678", {"start": v(-26.8, -32.7) * mm, "end": v(-26.54, -32.7) * mm});
            skArc(sketch, "E1679", {"start": v(-26.54, -32.7) * mm, "mid": v(-26.47, -32.63) * mm, "end": v(-26.54, -32.55) * mm});
            skLineSegment(sketch, "E1680", {"start": v(-26.54, -32.55) * mm, "end": v(-26.8, -32.55) * mm});
            skArc(sketch, "E1681", {"start": v(-26.8, -32.55) * mm, "mid": v(-26.87, -32.63) * mm, "end": v(-26.8, -32.7) * mm});
            skLineSegment(sketch, "E1682", {"start": v(-28.32, -26.45) * mm, "end": v(-28.57, -26.45) * mm});
            skArc(sketch, "E1683", {"start": v(-28.57, -26.45) * mm, "mid": v(-28.65, -26.53) * mm, "end": v(-28.57, -26.6) * mm});
            skLineSegment(sketch, "E1684", {"start": v(-28.57, -26.6) * mm, "end": v(-28.32, -26.6) * mm});
            skArc(sketch, "E1685", {"start": v(-28.32, -26.6) * mm, "mid": v(-28.24, -26.53) * mm, "end": v(-28.32, -26.45) * mm});
            skLineSegment(sketch, "E1686", {"start": v(-26.8, -26.6) * mm, "end": v(-26.54, -26.6) * mm});
            skArc(sketch, "E1687", {"start": v(-26.54, -26.6) * mm, "mid": v(-26.47, -26.53) * mm, "end": v(-26.54, -26.45) * mm});
            skLineSegment(sketch, "E1688", {"start": v(-26.54, -26.45) * mm, "end": v(-26.8, -26.45) * mm});
            skArc(sketch, "E1689", {"start": v(-26.8, -26.45) * mm, "mid": v(-26.87, -26.53) * mm, "end": v(-26.8, -26.6) * mm});
            skLineSegment(sketch, "E1690", {"start": v(-29.8, -28.3) * mm, "end": v(-29.8, -30.85) * mm});
            skArc(sketch, "E1691", {"start": v(-29.8, -30.85) * mm, "mid": v(-29.72, -30.92) * mm, "end": v(-29.64, -30.85) * mm});
            skLineSegment(sketch, "E1692", {"start": v(-29.64, -30.85) * mm, "end": v(-29.64, -28.3) * mm});
            skArc(sketch, "E1693", {"start": v(-29.64, -28.3) * mm, "mid": v(-29.72, -28.23) * mm, "end": v(-29.8, -28.3) * mm});
            skLineSegment(sketch, "E1694", {"start": v(-25.2, -30.85) * mm, "end": v(-25.2, -28.3) * mm});
            skArc(sketch, "E1695", {"start": v(-25.2, -28.3) * mm, "mid": v(-25.27, -28.23) * mm, "end": v(-25.35, -28.3) * mm});
            skLineSegment(sketch, "E1696", {"start": v(-25.35, -28.3) * mm, "end": v(-25.35, -30.85) * mm});
            skArc(sketch, "E1697", {"start": v(-25.35, -30.85) * mm, "mid": v(-25.27, -30.92) * mm, "end": v(-25.2, -30.85) * mm});
            skLineSegment(sketch, "E1698", {"start": v(-26.29, -27.09) * mm, "end": v(-27.05, -27.09) * mm});
            skArc(sketch, "E1699", {"start": v(-27.05, -27.09) * mm, "mid": v(-27.13, -27.17) * mm, "end": v(-27.05, -27.24) * mm});
            skLineSegment(sketch, "E1700", {"start": v(-27.05, -27.24) * mm, "end": v(-26.29, -27.24) * mm});
            skArc(sketch, "E1701", {"start": v(-26.29, -27.24) * mm, "mid": v(-26.21, -27.17) * mm, "end": v(-26.29, -27.09) * mm});
            skLineSegment(sketch, "E1702", {"start": v(-28.07, -27.09) * mm, "end": v(-28.83, -27.09) * mm});
            skArc(sketch, "E1703", {"start": v(-28.83, -27.09) * mm, "mid": v(-28.9, -27.17) * mm, "end": v(-28.83, -27.24) * mm});
            skLineSegment(sketch, "E1704", {"start": v(-28.83, -27.24) * mm, "end": v(-28.07, -27.24) * mm});
            skArc(sketch, "E1705", {"start": v(-28.07, -27.24) * mm, "mid": v(-28, -27.17) * mm, "end": v(-28.07, -27.09) * mm});
            skLineSegment(sketch, "E1706", {"start": v(-27.07, -27.1) * mm, "end": v(-27.96, -27.35) * mm});
            skArc(sketch, "E1707", {"start": v(-27.96, -27.35) * mm, "mid": v(-28.01, -27.44) * mm, "end": v(-27.92, -27.5) * mm});
            skLineSegment(sketch, "E1708", {"start": v(-27.92, -27.5) * mm, "end": v(-27.03, -27.24) * mm});
            skArc(sketch, "E1709", {"start": v(-27.03, -27.24) * mm, "mid": v(-26.98, -27.14) * mm, "end": v(-27.07, -27.1) * mm});
            skLineSegment(sketch, "E1710", {"start": v(-25.42, -26.32) * mm, "end": v(-25.8, -25.94) * mm});
            skArc(sketch, "E1711", {"start": v(-25.8, -25.94) * mm, "mid": v(-25.89, -25.94) * mm, "end": v(-25.89, -26.03) * mm});
            skLineSegment(sketch, "E1712", {"start": v(-25.89, -26.03) * mm, "end": v(-25.5, -26.41) * mm});
            skArc(sketch, "E1713", {"start": v(-25.5, -26.41) * mm, "mid": v(-25.42, -26.41) * mm, "end": v(-25.42, -26.32) * mm});
            skLineSegment(sketch, "E1714", {"start": v(-25.84, -26.05) * mm, "end": v(-24.7, -26.05) * mm});
            skArc(sketch, "E1715", {"start": v(-24.7, -26.05) * mm, "mid": v(-24.64, -25.99) * mm, "end": v(-24.7, -25.92) * mm});
            skLineSegment(sketch, "E1716", {"start": v(-24.7, -25.92) * mm, "end": v(-25.84, -25.92) * mm});
            skArc(sketch, "E1717", {"start": v(-25.84, -25.92) * mm, "mid": v(-25.9, -25.99) * mm, "end": v(-25.84, -26.05) * mm});
            skLineSegment(sketch, "E1718", {"start": v(-24.64, -26.37) * mm, "end": v(-24.64, -25.6) * mm});
            skArc(sketch, "E1719", {"start": v(-24.64, -25.6) * mm, "mid": v(-24.7, -25.54) * mm, "end": v(-24.76, -25.6) * mm});
            skLineSegment(sketch, "E1720", {"start": v(-24.76, -25.6) * mm, "end": v(-24.76, -26.37) * mm});
            skArc(sketch, "E1721", {"start": v(-24.76, -26.37) * mm, "mid": v(-24.7, -26.43) * mm, "end": v(-24.64, -26.37) * mm});
            skLineSegment(sketch, "E1722", {"start": v(-24.9, -33.48) * mm, "end": v(-24.9, -34.24) * mm});
            skArc(sketch, "E1723", {"start": v(-24.9, -34.24) * mm, "mid": v(-24.83, -34.3) * mm, "end": v(-24.76, -34.24) * mm});
            skLineSegment(sketch, "E1724", {"start": v(-24.76, -34.24) * mm, "end": v(-24.76, -33.48) * mm});
            skArc(sketch, "E1725", {"start": v(-24.76, -33.48) * mm, "mid": v(-24.83, -33.41) * mm, "end": v(-24.9, -33.48) * mm});
            skLineSegment(sketch, "E1726", {"start": v(-24.78, -34.2) * mm, "end": v(-25.55, -33.43) * mm});
            skArc(sketch, "E1727", {"start": v(-25.55, -33.43) * mm, "mid": v(-25.64, -33.43) * mm, "end": v(-25.64, -33.52) * mm});
            skLineSegment(sketch, "E1728", {"start": v(-25.64, -33.52) * mm, "end": v(-24.87, -34.29) * mm});
            skArc(sketch, "E1729", {"start": v(-24.87, -34.29) * mm, "mid": v(-24.78, -34.29) * mm, "end": v(-24.78, -34.2) * mm});
            skLineSegment(sketch, "E1730", {"start": v(-25.6, -33.41) * mm, "end": v(-25.78, -33.41) * mm});
            skArc(sketch, "E1731", {"start": v(-25.78, -33.41) * mm, "mid": v(-25.84, -33.48) * mm, "end": v(-25.78, -33.54) * mm});
            skLineSegment(sketch, "E1732", {"start": v(-25.78, -33.54) * mm, "end": v(-25.6, -33.54) * mm});
            skArc(sketch, "E1733", {"start": v(-25.6, -33.54) * mm, "mid": v(-25.53, -33.48) * mm, "end": v(-25.6, -33.41) * mm});
            skLineSegment(sketch, "E1734", {"start": v(-25.83, -33.43) * mm, "end": v(-26.02, -33.62) * mm});
            skArc(sketch, "E1735", {"start": v(-26.02, -33.62) * mm, "mid": v(-26.02, -33.71) * mm, "end": v(-25.93, -33.71) * mm});
            skLineSegment(sketch, "E1736", {"start": v(-25.93, -33.71) * mm, "end": v(-25.74, -33.52) * mm});
            skArc(sketch, "E1737", {"start": v(-25.74, -33.52) * mm, "mid": v(-25.74, -33.43) * mm, "end": v(-25.83, -33.43) * mm});
            skLineSegment(sketch, "E1738", {"start": v(-26.04, -33.67) * mm, "end": v(-26.04, -34.05) * mm});
            skArc(sketch, "E1739", {"start": v(-26.04, -34.05) * mm, "mid": v(-25.97, -34.11) * mm, "end": v(-25.9, -34.05) * mm});
            skLineSegment(sketch, "E1740", {"start": v(-25.9, -34.05) * mm, "end": v(-25.9, -33.67) * mm});
            skArc(sketch, "E1741", {"start": v(-25.9, -33.67) * mm, "mid": v(-25.97, -33.6) * mm, "end": v(-26.04, -33.67) * mm});
            skLineSegment(sketch, "E1742", {"start": v(-26.02, -34.1) * mm, "end": v(-25.83, -34.29) * mm});
            skArc(sketch, "E1743", {"start": v(-25.83, -34.29) * mm, "mid": v(-25.74, -34.29) * mm, "end": v(-25.74, -34.2) * mm});
            skLineSegment(sketch, "E1744", {"start": v(-25.74, -34.2) * mm, "end": v(-25.93, -34) * mm});
            skArc(sketch, "E1745", {"start": v(-25.93, -34) * mm, "mid": v(-26.02, -34) * mm, "end": v(-26.02, -34.1) * mm});
            skLineSegment(sketch, "E1746", {"start": v(-30.05, -26.07) * mm, "end": v(-30.24, -25.88) * mm});
            skArc(sketch, "E1747", {"start": v(-30.25, -25.88) * mm, "mid": v(-30.33, -25.88) * mm, "end": v(-30.33, -25.97) * mm});
            skLineSegment(sketch, "E1748", {"start": v(-30.33, -25.97) * mm, "end": v(-30.14, -26.16) * mm});
            skArc(sketch, "E1749", {"start": v(-30.14, -26.16) * mm, "mid": v(-30.05, -26.16) * mm, "end": v(-30.05, -26.07) * mm});
            skLineSegment(sketch, "E1750", {"start": v(-30.23, -25.92) * mm, "end": v(-30.23, -25.54) * mm});
            skArc(sketch, "E1751", {"start": v(-30.23, -25.54) * mm, "mid": v(-30.29, -25.48) * mm, "end": v(-30.35, -25.54) * mm});
            skLineSegment(sketch, "E1752", {"start": v(-30.35, -25.54) * mm, "end": v(-30.35, -25.92) * mm});
            skArc(sketch, "E1753", {"start": v(-30.35, -25.92) * mm, "mid": v(-30.29, -25.99) * mm, "end": v(-30.23, -25.92) * mm});
            skLineSegment(sketch, "E1754", {"start": v(-30.24, -25.59) * mm, "end": v(-30.05, -25.4) * mm});
            skArc(sketch, "E1755", {"start": v(-30.05, -25.4) * mm, "mid": v(-30.05, -25.3) * mm, "end": v(-30.14, -25.3) * mm});
            skLineSegment(sketch, "E1756", {"start": v(-30.14, -25.3) * mm, "end": v(-30.33, -25.5) * mm});
            skArc(sketch, "E1757", {"start": v(-30.33, -25.5) * mm, "mid": v(-30.33, -25.59) * mm, "end": v(-30.25, -25.59) * mm});
            skLineSegment(sketch, "E1758", {"start": v(-30.1, -25.41) * mm, "end": v(-29.9, -25.41) * mm});
            skArc(sketch, "E1759", {"start": v(-29.9, -25.41) * mm, "mid": v(-29.84, -25.35) * mm, "end": v(-29.9, -25.29) * mm});
            skLineSegment(sketch, "E1760", {"start": v(-29.9, -25.29) * mm, "end": v(-30.1, -25.29) * mm});
            skArc(sketch, "E1761", {"start": v(-30.1, -25.29) * mm, "mid": v(-30.16, -25.35) * mm, "end": v(-30.1, -25.41) * mm});
            skLineSegment(sketch, "E1762", {"start": v(-29.95, -25.4) * mm, "end": v(-29.76, -25.59) * mm});
            skArc(sketch, "E1763", {"start": v(-29.76, -25.59) * mm, "mid": v(-29.67, -25.59) * mm, "end": v(-29.67, -25.5) * mm});
            skLineSegment(sketch, "E1764", {"start": v(-29.67, -25.5) * mm, "end": v(-29.86, -25.3) * mm});
            skArc(sketch, "E1765", {"start": v(-29.86, -25.3) * mm, "mid": v(-29.95, -25.3) * mm, "end": v(-29.95, -25.4) * mm});
            skLineSegment(sketch, "E1766", {"start": v(-29.78, -25.54) * mm, "end": v(-29.78, -25.73) * mm});
            skArc(sketch, "E1767", {"start": v(-29.78, -25.73) * mm, "mid": v(-29.72, -25.8) * mm, "end": v(-29.65, -25.73) * mm});
            skLineSegment(sketch, "E1768", {"start": v(-29.65, -25.73) * mm, "end": v(-29.65, -25.54) * mm});
            skArc(sketch, "E1769", {"start": v(-29.65, -25.54) * mm, "mid": v(-29.72, -25.48) * mm, "end": v(-29.78, -25.54) * mm});
            skLineSegment(sketch, "E1770", {"start": v(-29.67, -25.59) * mm, "end": v(-29.48, -25.4) * mm});
            skArc(sketch, "E1771", {"start": v(-29.48, -25.4) * mm, "mid": v(-29.48, -25.3) * mm, "end": v(-29.57, -25.3) * mm});
            skLineSegment(sketch, "E1772", {"start": v(-29.57, -25.3) * mm, "end": v(-29.76, -25.5) * mm});
            skArc(sketch, "E1773", {"start": v(-29.76, -25.5) * mm, "mid": v(-29.76, -25.59) * mm, "end": v(-29.67, -25.59) * mm});
            skLineSegment(sketch, "E1774", {"start": v(-29.53, -25.41) * mm, "end": v(-29.34, -25.41) * mm});
            skArc(sketch, "E1775", {"start": v(-29.34, -25.41) * mm, "mid": v(-29.27, -25.35) * mm, "end": v(-29.34, -25.29) * mm});
            skLineSegment(sketch, "E1776", {"start": v(-29.34, -25.29) * mm, "end": v(-29.53, -25.29) * mm});
            skArc(sketch, "E1777", {"start": v(-29.53, -25.29) * mm, "mid": v(-29.6, -25.35) * mm, "end": v(-29.53, -25.41) * mm});
            skLineSegment(sketch, "E1778", {"start": v(-29.38, -25.4) * mm, "end": v(-29.2, -25.59) * mm});
            skArc(sketch, "E1779", {"start": v(-29.2, -25.59) * mm, "mid": v(-29.1, -25.59) * mm, "end": v(-29.1, -25.5) * mm});
            skLineSegment(sketch, "E1780", {"start": v(-29.1, -25.5) * mm, "end": v(-29.3, -25.3) * mm});
            skArc(sketch, "E1781", {"start": v(-29.3, -25.3) * mm, "mid": v(-29.38, -25.3) * mm, "end": v(-29.38, -25.4) * mm});
            skLineSegment(sketch, "E1782", {"start": v(-29.2, -25.54) * mm, "end": v(-29.2, -25.92) * mm});
            skArc(sketch, "E1783", {"start": v(-29.2, -25.92) * mm, "mid": v(-29.15, -25.99) * mm, "end": v(-29.08, -25.92) * mm});
            skLineSegment(sketch, "E1784", {"start": v(-29.08, -25.92) * mm, "end": v(-29.08, -25.54) * mm});
            skArc(sketch, "E1785", {"start": v(-29.08, -25.54) * mm, "mid": v(-29.15, -25.48) * mm, "end": v(-29.2, -25.54) * mm});
            skLineSegment(sketch, "E1786", {"start": v(-29.2, -25.88) * mm, "end": v(-29.38, -26.07) * mm});
            skArc(sketch, "E1787", {"start": v(-29.38, -26.07) * mm, "mid": v(-29.38, -26.16) * mm, "end": v(-29.3, -26.16) * mm});
            skLineSegment(sketch, "E1788", {"start": v(-29.3, -26.16) * mm, "end": v(-29.1, -25.97) * mm});
            skArc(sketch, "E1789", {"start": v(-29.1, -25.97) * mm, "mid": v(-29.1, -25.88) * mm, "end": v(-29.2, -25.88) * mm});
            skLineSegment(sketch, "E1790", {"start": v(-29.15, -33.6) * mm, "end": v(-30.29, -33.6) * mm});
            skArc(sketch, "E1791", {"start": v(-30.29, -33.6) * mm, "mid": v(-30.35, -33.67) * mm, "end": v(-30.29, -33.73) * mm});
            skLineSegment(sketch, "E1792", {"start": v(-30.29, -33.73) * mm, "end": v(-29.15, -33.73) * mm});
            skArc(sketch, "E1793", {"start": v(-29.15, -33.73) * mm, "mid": v(-29.08, -33.67) * mm, "end": v(-29.15, -33.6) * mm});
            skLineSegment(sketch, "E1794", {"start": v(-30.33, -33.71) * mm, "end": v(-29.76, -34.29) * mm});
            skArc(sketch, "E1795", {"start": v(-29.76, -34.29) * mm, "mid": v(-29.67, -34.29) * mm, "end": v(-29.67, -34.2) * mm});
            skLineSegment(sketch, "E1796", {"start": v(-29.67, -34.2) * mm, "end": v(-30.24, -33.62) * mm});
            skArc(sketch, "E1797", {"start": v(-30.25, -33.62) * mm, "mid": v(-30.33, -33.62) * mm, "end": v(-30.33, -33.71) * mm});
            skLineSegment(sketch, "E1798", {"start": v(-29.65, -34.24) * mm, "end": v(-29.65, -33.48) * mm});
            skArc(sketch, "E1799", {"start": v(-29.65, -33.48) * mm, "mid": v(-29.72, -33.41) * mm, "end": v(-29.78, -33.48) * mm});
            skLineSegment(sketch, "E1800", {"start": v(-29.78, -33.48) * mm, "end": v(-29.78, -34.24) * mm});
            skArc(sketch, "E1801", {"start": v(-29.78, -34.24) * mm, "mid": v(-29.72, -34.3) * mm, "end": v(-29.65, -34.24) * mm});
            skCircle(sketch, "E1802", {"center": v(-27.56, -29.58) * mm, "radius": 1.7 * mm});
            skCircle(sketch, "E1803", {"center": v(-27.56, -29.58) * mm, "radius": 1.85 * mm});
            skCircle(sketch, "E1804", {"center": v(-29.72, -27.42) * mm, "radius": 0.43 * mm});
            skCircle(sketch, "E1805", {"center": v(-29.72, -27.42) * mm, "radius": 0.58 * mm});
            skCircle(sketch, "E1806", {"center": v(-29.6, -31.74) * mm, "radius": 0.43 * mm});
            skCircle(sketch, "E1807", {"center": v(-29.6, -31.74) * mm, "radius": 0.58 * mm});
            skCircle(sketch, "E1808", {"center": v(-25.4, -31.74) * mm, "radius": 0.43 * mm});
            skCircle(sketch, "E1809", {"center": v(-25.4, -31.74) * mm, "radius": 0.58 * mm});
            skCircle(sketch, "E1810", {"center": v(-25.4, -27.42) * mm, "radius": 0.43 * mm});
            skCircle(sketch, "E1811", {"center": v(-25.4, -27.42) * mm, "radius": 0.58 * mm});
            skCircle(sketch, "E1812", {"center": v(-27.56, -29.58) * mm, "radius": 0.6 * mm});
            skCircle(sketch, "E1813", {"center": v(-27.56, -29.58) * mm, "radius": 0.66 * mm});
            skCircle(sketch, "E1814", {"center": v(-27.56, -29.58) * mm, "radius": 0.18 * mm});
            skCircle(sketch, "E1815", {"center": v(-27.56, -29.58) * mm, "radius": 0.33 * mm});
            skLineSegment(sketch, "E1816", {"start": v(-26.06, -25.57) * mm, "end": v(-26.06, -27.09) * mm});
            skArc(sketch, "E1817", {"start": v(-25.8, -27.09) * mm, "mid": v(-25.3, -27.59) * mm, "end": v(-24.8, -27.09) * mm});
            skLineSegment(sketch, "E1818", {"start": v(-24.54, -27.09) * mm, "end": v(-24.54, -25.57) * mm});
            skArc(sketch, "E1819", {"start": v(-24.8, -25.57) * mm, "mid": v(-25.3, -25.07) * mm, "end": v(-25.8, -25.57) * mm});
            skLineSegment(sketch, "E1820", {"start": v(-26.06, -32.07) * mm, "end": v(-26.06, -33.6) * mm});
            skArc(sketch, "E1821", {"start": v(-25.8, -33.6) * mm, "mid": v(-25.3, -34.1) * mm, "end": v(-24.8, -33.6) * mm});
            skLineSegment(sketch, "E1822", {"start": v(-24.54, -33.6) * mm, "end": v(-24.54, -32.07) * mm});
            skArc(sketch, "E1823", {"start": v(-24.8, -32.07) * mm, "mid": v(-25.3, -31.57) * mm, "end": v(-25.8, -32.07) * mm});
            skLineSegment(sketch, "E1824", {"start": v(-30.58, -25.57) * mm, "end": v(-30.58, -27.09) * mm});
            skArc(sketch, "E1825", {"start": v(-30.32, -27.09) * mm, "mid": v(-29.82, -27.59) * mm, "end": v(-29.32, -27.09) * mm});
            skLineSegment(sketch, "E1826", {"start": v(-29.06, -27.09) * mm, "end": v(-29.06, -25.57) * mm});
            skArc(sketch, "E1827", {"start": v(-29.32, -25.57) * mm, "mid": v(-29.82, -25.07) * mm, "end": v(-30.32, -25.57) * mm});
            skLineSegment(sketch, "E1828", {"start": v(-30.58, -32.07) * mm, "end": v(-30.58, -33.6) * mm});
            skArc(sketch, "E1829", {"start": v(-30.32, -33.6) * mm, "mid": v(-29.82, -34.1) * mm, "end": v(-29.32, -33.6) * mm});
            skLineSegment(sketch, "E1830", {"start": v(-29.06, -33.6) * mm, "end": v(-29.06, -32.07) * mm});
            skArc(sketch, "E1831", {"start": v(-29.32, -32.07) * mm, "mid": v(-29.82, -31.57) * mm, "end": v(-30.32, -32.07) * mm});
            skLineSegment(sketch, "E1832", {"start": v(-13.05, -21.77) * mm, "end": v(-13.05, -31.93) * mm});
            skArc(sketch, "E1833", {"start": v(-13.05, -31.93) * mm, "mid": v(-12.92, -32.06) * mm, "end": v(-12.8, -31.93) * mm});
            skLineSegment(sketch, "E1834", {"start": v(-12.8, -31.93) * mm, "end": v(-12.8, -21.77) * mm});
            skArc(sketch, "E1835", {"start": v(-12.8, -21.77) * mm, "mid": v(-12.92, -21.64) * mm, "end": v(-13.05, -21.77) * mm});
            skLineSegment(sketch, "E1836", {"start": v(-12.92, -31.8) * mm, "end": v(-14.83, -31.8) * mm});
            skArc(sketch, "E1837", {"start": v(-14.83, -31.8) * mm, "mid": v(-14.96, -31.93) * mm, "end": v(-14.83, -32.06) * mm});
            skLineSegment(sketch, "E1838", {"start": v(-14.83, -32.06) * mm, "end": v(-12.92, -32.06) * mm});
            skArc(sketch, "E1839", {"start": v(-12.92, -32.06) * mm, "mid": v(-12.8, -31.93) * mm, "end": v(-12.92, -31.8) * mm});
            skLineSegment(sketch, "E1840", {"start": v(-14.83, -31.8) * mm, "end": v(-19.27, -31.8) * mm});
            skArc(sketch, "E1841", {"start": v(-19.27, -31.8) * mm, "mid": v(-19.4, -31.93) * mm, "end": v(-19.27, -32.06) * mm});
            skLineSegment(sketch, "E1842", {"start": v(-19.27, -32.06) * mm, "end": v(-14.83, -32.06) * mm});
            skArc(sketch, "E1843", {"start": v(-14.83, -32.06) * mm, "mid": v(-14.7, -31.93) * mm, "end": v(-14.83, -31.8) * mm});
            skLineSegment(sketch, "E1844", {"start": v(-19.15, -31.93) * mm, "end": v(-19.15, -21.77) * mm});
            skArc(sketch, "E1845", {"start": v(-19.15, -21.77) * mm, "mid": v(-19.27, -21.64) * mm, "end": v(-19.4, -21.77) * mm});
            skLineSegment(sketch, "E1846", {"start": v(-19.4, -21.77) * mm, "end": v(-19.4, -31.93) * mm});
            skArc(sketch, "E1847", {"start": v(-19.4, -31.93) * mm, "mid": v(-19.27, -32.06) * mm, "end": v(-19.15, -31.93) * mm});
            skLineSegment(sketch, "E1848", {"start": v(-19.27, -21.9) * mm, "end": v(-14.83, -21.9) * mm});
            skArc(sketch, "E1849", {"start": v(-14.83, -21.9) * mm, "mid": v(-14.7, -21.77) * mm, "end": v(-14.83, -21.64) * mm});
            skLineSegment(sketch, "E1850", {"start": v(-14.83, -21.64) * mm, "end": v(-19.27, -21.64) * mm});
            skArc(sketch, "E1851", {"start": v(-19.27, -21.64) * mm, "mid": v(-19.4, -21.77) * mm, "end": v(-19.27, -21.9) * mm});
            skLineSegment(sketch, "E1852", {"start": v(-14.83, -21.9) * mm, "end": v(-12.92, -21.9) * mm});
            skArc(sketch, "E1853", {"start": v(-12.92, -21.9) * mm, "mid": v(-12.8, -21.77) * mm, "end": v(-12.92, -21.64) * mm});
            skLineSegment(sketch, "E1854", {"start": v(-12.92, -21.64) * mm, "end": v(-14.83, -21.64) * mm});
            skArc(sketch, "E1855", {"start": v(-14.83, -21.64) * mm, "mid": v(-14.96, -21.77) * mm, "end": v(-14.83, -21.9) * mm});
            skLineSegment(sketch, "E1856", {"start": v(-14.96, -21.77) * mm, "end": v(-14.96, -31.93) * mm});
            skArc(sketch, "E1857", {"start": v(-14.96, -31.93) * mm, "mid": v(-14.83, -32.06) * mm, "end": v(-14.7, -31.93) * mm});
            skLineSegment(sketch, "E1858", {"start": v(-14.7, -31.93) * mm, "end": v(-14.7, -21.77) * mm});
            skArc(sketch, "E1859", {"start": v(-14.7, -21.77) * mm, "mid": v(-14.83, -21.64) * mm, "end": v(-14.96, -21.77) * mm});
            skLineSegment(sketch, "E1860", {"start": v(-16.85, -23.8) * mm, "end": v(-15.34, -23.8) * mm});
            skArc(sketch, "E1861", {"start": v(-15.34, -23.54) * mm, "mid": v(-14.84, -23.04) * mm, "end": v(-15.34, -22.54) * mm});
            skLineSegment(sketch, "E1862", {"start": v(-15.34, -22.28) * mm, "end": v(-16.85, -22.28) * mm});
            skArc(sketch, "E1863", {"start": v(-16.85, -22.54) * mm, "mid": v(-17.35, -23.04) * mm, "end": v(-16.85, -23.54) * mm});
            skLineSegment(sketch, "E1864", {"start": v(-16.85, -26.33) * mm, "end": v(-15.34, -26.33) * mm});
            skArc(sketch, "E1865", {"start": v(-15.34, -26.08) * mm, "mid": v(-14.84, -25.58) * mm, "end": v(-15.34, -25.08) * mm});
            skLineSegment(sketch, "E1866", {"start": v(-15.34, -24.82) * mm, "end": v(-16.85, -24.82) * mm});
            skArc(sketch, "E1867", {"start": v(-16.85, -25.08) * mm, "mid": v(-17.35, -25.58) * mm, "end": v(-16.85, -26.08) * mm});
            skLineSegment(sketch, "E1868", {"start": v(-16.85, -28.87) * mm, "end": v(-15.34, -28.87) * mm});
            skArc(sketch, "E1869", {"start": v(-15.34, -28.62) * mm, "mid": v(-14.84, -28.12) * mm, "end": v(-15.34, -27.62) * mm});
            skLineSegment(sketch, "E1870", {"start": v(-15.34, -27.36) * mm, "end": v(-16.85, -27.36) * mm});
            skArc(sketch, "E1871", {"start": v(-16.85, -27.62) * mm, "mid": v(-17.35, -28.12) * mm, "end": v(-16.85, -28.62) * mm});
            skLineSegment(sketch, "E1872", {"start": v(-16.85, -31.41) * mm, "end": v(-15.34, -31.41) * mm});
            skArc(sketch, "E1873", {"start": v(-15.34, -31.16) * mm, "mid": v(-14.84, -30.66) * mm, "end": v(-15.34, -30.16) * mm});
            skLineSegment(sketch, "E1874", {"start": v(-15.34, -29.9) * mm, "end": v(-16.85, -29.9) * mm});
            skArc(sketch, "E1875", {"start": v(-16.85, -30.16) * mm, "mid": v(-17.35, -30.66) * mm, "end": v(-16.85, -31.16) * mm});
            skLineSegment(sketch, "E1876", {"start": v(-13.05, -32.88) * mm, "end": v(-13.05, -37.96) * mm});
            skArc(sketch, "E1877", {"start": v(-13.05, -37.96) * mm, "mid": v(-12.92, -38.09) * mm, "end": v(-12.8, -37.96) * mm});
            skLineSegment(sketch, "E1878", {"start": v(-12.8, -37.96) * mm, "end": v(-12.8, -32.88) * mm});
            skArc(sketch, "E1879", {"start": v(-12.8, -32.88) * mm, "mid": v(-12.92, -32.75) * mm, "end": v(-13.05, -32.88) * mm});
            skLineSegment(sketch, "E1880", {"start": v(-12.92, -37.83) * mm, "end": v(-14.83, -37.83) * mm});
            skArc(sketch, "E1881", {"start": v(-14.83, -37.83) * mm, "mid": v(-14.96, -37.96) * mm, "end": v(-14.83, -38.09) * mm});
            skLineSegment(sketch, "E1882", {"start": v(-14.83, -38.09) * mm, "end": v(-12.92, -38.09) * mm});
            skArc(sketch, "E1883", {"start": v(-12.92, -38.09) * mm, "mid": v(-12.8, -37.96) * mm, "end": v(-12.92, -37.83) * mm});
            skLineSegment(sketch, "E1884", {"start": v(-14.83, -37.83) * mm, "end": v(-19.27, -37.83) * mm});
            skArc(sketch, "E1885", {"start": v(-19.27, -37.83) * mm, "mid": v(-19.4, -37.96) * mm, "end": v(-19.27, -38.09) * mm});
            skLineSegment(sketch, "E1886", {"start": v(-19.27, -38.09) * mm, "end": v(-14.83, -38.09) * mm});
            skArc(sketch, "E1887", {"start": v(-14.83, -38.09) * mm, "mid": v(-14.7, -37.96) * mm, "end": v(-14.83, -37.83) * mm});
            skLineSegment(sketch, "E1888", {"start": v(-19.15, -37.96) * mm, "end": v(-19.15, -32.88) * mm});
            skArc(sketch, "E1889", {"start": v(-19.15, -32.88) * mm, "mid": v(-19.27, -32.75) * mm, "end": v(-19.4, -32.88) * mm});
            skLineSegment(sketch, "E1890", {"start": v(-19.4, -32.88) * mm, "end": v(-19.4, -37.96) * mm});
            skArc(sketch, "E1891", {"start": v(-19.4, -37.96) * mm, "mid": v(-19.27, -38.09) * mm, "end": v(-19.15, -37.96) * mm});
            skLineSegment(sketch, "E1892", {"start": v(-19.27, -33) * mm, "end": v(-14.83, -33) * mm});
            skArc(sketch, "E1893", {"start": v(-14.83, -33) * mm, "mid": v(-14.7, -32.88) * mm, "end": v(-14.83, -32.75) * mm});
            skLineSegment(sketch, "E1894", {"start": v(-14.83, -32.75) * mm, "end": v(-19.27, -32.75) * mm});
            skArc(sketch, "E1895", {"start": v(-19.27, -32.75) * mm, "mid": v(-19.4, -32.88) * mm, "end": v(-19.27, -33) * mm});
            skLineSegment(sketch, "E1896", {"start": v(-14.83, -33) * mm, "end": v(-12.92, -33) * mm});
            skArc(sketch, "E1897", {"start": v(-12.92, -33) * mm, "mid": v(-12.8, -32.88) * mm, "end": v(-12.92, -32.75) * mm});
            skLineSegment(sketch, "E1898", {"start": v(-12.92, -32.75) * mm, "end": v(-14.83, -32.75) * mm});
            skArc(sketch, "E1899", {"start": v(-14.83, -32.75) * mm, "mid": v(-14.96, -32.88) * mm, "end": v(-14.83, -33) * mm});
            skLineSegment(sketch, "E1900", {"start": v(-14.96, -32.88) * mm, "end": v(-14.96, -37.96) * mm});
            skArc(sketch, "E1901", {"start": v(-14.96, -37.96) * mm, "mid": v(-14.83, -38.09) * mm, "end": v(-14.7, -37.96) * mm});
            skLineSegment(sketch, "E1902", {"start": v(-14.7, -37.96) * mm, "end": v(-14.7, -32.88) * mm});
            skArc(sketch, "E1903", {"start": v(-14.7, -32.88) * mm, "mid": v(-14.83, -32.75) * mm, "end": v(-14.96, -32.88) * mm});
            skLineSegment(sketch, "E1904", {"start": v(-16.85, -34.9) * mm, "end": v(-15.34, -34.9) * mm});
            skArc(sketch, "E1905", {"start": v(-15.34, -34.65) * mm, "mid": v(-14.84, -34.15) * mm, "end": v(-15.34, -33.65) * mm});
            skLineSegment(sketch, "E1906", {"start": v(-15.34, -33.4) * mm, "end": v(-16.85, -33.4) * mm});
            skArc(sketch, "E1907", {"start": v(-16.85, -33.65) * mm, "mid": v(-17.35, -34.15) * mm, "end": v(-16.85, -34.65) * mm});
            skLineSegment(sketch, "E1908", {"start": v(-16.85, -37.44) * mm, "end": v(-15.34, -37.44) * mm});
            skArc(sketch, "E1909", {"start": v(-15.34, -37.19) * mm, "mid": v(-14.84, -36.69) * mm, "end": v(-15.34, -36.19) * mm});
            skLineSegment(sketch, "E1910", {"start": v(-15.34, -35.93) * mm, "end": v(-16.85, -35.93) * mm});
            skArc(sketch, "E1911", {"start": v(-16.85, -36.19) * mm, "mid": v(-17.35, -36.69) * mm, "end": v(-16.85, -37.19) * mm});
            skLineSegment(sketch, "E1912", {"start": v(-50.6, -36.9) * mm, "end": v(-50.6, -15.66) * mm});
            skArc(sketch, "E1913", {"start": v(-50.6, -15.66) * mm, "mid": v(-50.9, -15.36) * mm, "end": v(-51.2, -15.66) * mm});
            skLineSegment(sketch, "E1914", {"start": v(-51.2, -15.66) * mm, "end": v(-51.2, -36.9) * mm});
            skArc(sketch, "E1915", {"start": v(-51.2, -36.9) * mm, "mid": v(-50.9, -37.2) * mm, "end": v(-50.6, -36.9) * mm});
            skLineSegment(sketch, "E1916", {"start": v(-50.69, -15.45) * mm, "end": v(-51.69, -14.45) * mm});
            skArc(sketch, "E1917", {"start": v(-51.69, -14.45) * mm, "mid": v(-52.11, -14.45) * mm, "end": v(-52.11, -14.87) * mm});
            skLineSegment(sketch, "E1918", {"start": v(-52.11, -14.87) * mm, "end": v(-51.11, -15.87) * mm});
            skArc(sketch, "E1919", {"start": v(-51.11, -15.87) * mm, "mid": v(-50.69, -15.87) * mm, "end": v(-50.69, -15.45) * mm});
            skCircle(sketch, "E1920", {"center": v(-50.9, -36.9) * mm, "radius": 0.5 * mm});
            skCircle(sketch, "E1921", {"center": v(-51.9, -14.66) * mm, "radius": 0.5 * mm});
            skLineSegment(sketch, "E1922", {"start": v(-62.9, -45.6) * mm, "end": v(-67.9, -45.6) * mm});
            skArc(sketch, "E1923", {"start": v(-67.9, -45.6) * mm, "mid": v(-68.2, -45.9) * mm, "end": v(-67.9, -46.2) * mm});
            skLineSegment(sketch, "E1924", {"start": v(-67.9, -46.2) * mm, "end": v(-62.9, -46.2) * mm});
            skArc(sketch, "E1925", {"start": v(-62.9, -46.2) * mm, "mid": v(-62.6, -45.9) * mm, "end": v(-62.9, -45.6) * mm});
            skLineSegment(sketch, "E1926", {"start": v(-68.11, -45.69) * mm, "end": v(-69.11, -46.69) * mm});
            skArc(sketch, "E1927", {"start": v(-69.11, -46.69) * mm, "mid": v(-69.11, -47.11) * mm, "end": v(-68.69, -47.11) * mm});
            skLineSegment(sketch, "E1928", {"start": v(-68.69, -47.11) * mm, "end": v(-67.69, -46.11) * mm});
            skArc(sketch, "E1929", {"start": v(-67.69, -46.11) * mm, "mid": v(-67.69, -45.69) * mm, "end": v(-68.11, -45.69) * mm});
            skCircle(sketch, "E1930", {"center": v(-62.9, -45.9) * mm, "radius": 0.5 * mm});
            skCircle(sketch, "E1931", {"center": v(-68.9, -46.9) * mm, "radius": 0.5 * mm});
            skCircle(sketch, "E1932", {"center": v(-74.9, -14.9) * mm, "radius": 0.5 * mm});
            skCircle(sketch, "E1933", {"center": v(-4.9, -14.9) * mm, "radius": 0.5 * mm});
            skCircle(sketch, "E1934", {"center": v(-4.9, -44.9) * mm, "radius": 0.5 * mm});
            skCircle(sketch, "E1935", {"center": v(-74.9, -44.9) * mm, "radius": 0.5 * mm});
            skLineSegment(sketch, "E1936", {"start": v(-79.9, -9.9) * mm, "end": v(0.1, -49.9) * mm, "construction": true});
            skLineSegment(sketch, "E1937", {"start": v(-79.9, -49.9) * mm, "end": v(0.1, -9.9) * mm, "construction": true});
            skPoint(sketch, "E1938", {"position": v(-39.9, -29.9) * mm});
            skSolve(sketch);
        }
        {
            var Q0;
            Q0=qCreatedBy(makeId("Front.planeOp"),FACE);
            var sketch = newSketch(context, id + "F1", { "sketchPlane" : qUnion([Q0])});
            skLineSegment(sketch, "E1939.bottom", {"start": v(0.1, -49.9) * mm, "end": v(-79.9, -49.9) * mm});
            skLineSegment(sketch, "E1939.top", {"start": v(0.1, -9.9) * mm, "end": v(-79.9, -9.9) * mm});
            skLineSegment(sketch, "E1939.left", {"start": v(0.1, -49.9) * mm, "end": v(0.1, -9.9) * mm});
            skLineSegment(sketch, "E1939.right", {"start": v(-79.9, -49.9) * mm, "end": v(-79.9, -9.9) * mm});
            skPoint(sketch, "E1939.middle", {"position": v(-39.9, -29.9) * mm});
            skCircle(sketch, "E1940", {"center": v(-64.66, -30.85) * mm, "radius": 12.8 * mm});
            skLineSegment(sketch, "E1941.bottom", {"start": v(-36.32, -24.15) * mm, "end": v(-47.28, -24.15) * mm});
            skLineSegment(sketch, "E1941.top", {"start": v(-36.32, -10.15) * mm, "end": v(-47.28, -10.15) * mm});
            skLineSegment(sketch, "E1941.left", {"start": v(-35.32, -23.15) * mm, "end": v(-35.32, -11.15) * mm});
            skLineSegment(sketch, "E1941.right", {"start": v(-48.28, -23.15) * mm, "end": v(-48.28, -11.15) * mm});
            skPoint(sketch, "E1941.middle", {"position": v(-41.8, -17.15) * mm});
            skPoint(sketch, "E1942.visualSharp", {"position": v(-48.28, -10.15) * mm});
            skArc(sketch, "E1942.filletArc", {"start": v(-47.28, -10.15) * mm, "mid": v(-47.98, -10.44) * mm, "end": v(-48.28, -11.15) * mm});
            skPoint(sketch, "E1943.visualSharp", {"position": v(-35.32, -10.15) * mm});
            skArc(sketch, "E1943.filletArc", {"start": v(-35.32, -11.15) * mm, "mid": v(-35.61, -10.44) * mm, "end": v(-36.32, -10.15) * mm});
            skPoint(sketch, "E1944.visualSharp", {"position": v(-35.32, -24.15) * mm});
            skArc(sketch, "E1944.filletArc", {"start": v(-36.32, -24.15) * mm, "mid": v(-35.61, -23.86) * mm, "end": v(-35.32, -23.15) * mm});
            skPoint(sketch, "E1945.visualSharp", {"position": v(-48.28, -24.15) * mm});
            skArc(sketch, "E1945.filletArc", {"start": v(-48.28, -23.15) * mm, "mid": v(-47.98, -23.86) * mm, "end": v(-47.28, -24.15) * mm});
            skLineSegment(sketch, "E1946.bottom", {"start": v(-36.32, -49.55) * mm, "end": v(-47.28, -49.55) * mm});
            skLineSegment(sketch, "E1946.top", {"start": v(-36.32, -35.55) * mm, "end": v(-47.28, -35.55) * mm});
            skLineSegment(sketch, "E1946.left", {"start": v(-35.32, -48.55) * mm, "end": v(-35.32, -36.55) * mm});
            skLineSegment(sketch, "E1946.right", {"start": v(-48.28, -48.55) * mm, "end": v(-48.28, -36.55) * mm});
            skPoint(sketch, "E1946.middle", {"position": v(-41.8, -42.55) * mm});
            skPoint(sketch, "E1947.visualSharp", {"position": v(-48.28, -35.55) * mm});
            skArc(sketch, "E1947.filletArc", {"start": v(-47.28, -35.55) * mm, "mid": v(-47.98, -35.84) * mm, "end": v(-48.28, -36.55) * mm});
            skPoint(sketch, "E1948.visualSharp", {"position": v(-35.32, -35.55) * mm});
            skArc(sketch, "E1948.filletArc", {"start": v(-35.32, -36.55) * mm, "mid": v(-35.61, -35.84) * mm, "end": v(-36.32, -35.55) * mm});
            skPoint(sketch, "E1949.visualSharp", {"position": v(-35.32, -49.55) * mm});
            skArc(sketch, "E1949.filletArc", {"start": v(-36.32, -49.55) * mm, "mid": v(-35.61, -49.26) * mm, "end": v(-35.32, -48.55) * mm});
            skPoint(sketch, "E1950.visualSharp", {"position": v(-48.28, -49.55) * mm});
            skArc(sketch, "E1950.filletArc", {"start": v(-48.28, -48.55) * mm, "mid": v(-47.98, -49.26) * mm, "end": v(-47.28, -49.55) * mm});
            skLineSegment(sketch, "E1951.bottom", {"start": v(-25.05, -33.58) * mm, "end": v(-30.07, -33.58) * mm});
            skLineSegment(sketch, "E1951.top", {"start": v(-25.05, -25.58) * mm, "end": v(-30.07, -25.58) * mm});
            skLineSegment(sketch, "E1951.left", {"start": v(-24.05, -32.58) * mm, "end": v(-24.05, -26.58) * mm});
            skLineSegment(sketch, "E1951.right", {"start": v(-31.07, -32.58) * mm, "end": v(-31.07, -26.58) * mm});
            skPoint(sketch, "E1951.middle", {"position": v(-27.56, -29.58) * mm});
            skPoint(sketch, "E1952.visualSharp", {"position": v(-31.07, -25.58) * mm});
            skArc(sketch, "E1952.filletArc", {"start": v(-30.07, -25.58) * mm, "mid": v(-30.77, -25.87) * mm, "end": v(-31.07, -26.58) * mm});
            skPoint(sketch, "E1953.visualSharp", {"position": v(-24.05, -25.58) * mm});
            skArc(sketch, "E1953.filletArc", {"start": v(-24.05, -26.58) * mm, "mid": v(-24.34, -25.87) * mm, "end": v(-25.05, -25.58) * mm});
            skPoint(sketch, "E1954.visualSharp", {"position": v(-24.05, -33.58) * mm});
            skArc(sketch, "E1954.filletArc", {"start": v(-25.05, -33.58) * mm, "mid": v(-24.34, -33.29) * mm, "end": v(-24.05, -32.58) * mm});
            skPoint(sketch, "E1955.visualSharp", {"position": v(-31.07, -33.58) * mm});
            skArc(sketch, "E1955.filletArc", {"start": v(-31.07, -32.58) * mm, "mid": v(-30.77, -33.29) * mm, "end": v(-30.07, -33.58) * mm});
            skLineSegment(sketch, "E1956.bottom", {"start": v(-19.02, -19.96) * mm, "end": v(-13.3, -19.96) * mm});
            skLineSegment(sketch, "E1956.top", {"start": v(-19.02, -39.35) * mm, "end": v(-13.3, -39.35) * mm});
            skLineSegment(sketch, "E1956.left", {"start": v(-20.02, -20.96) * mm, "end": v(-20.02, -38.35) * mm});
            skLineSegment(sketch, "E1956.right", {"start": v(-12.3, -20.96) * mm, "end": v(-12.3, -38.35) * mm});
            skLineSegment(sketch, "E1957", {"start": v(-79.9, -29.9) * mm, "end": v(0.1, -29.9) * mm, "construction": true});
            skPoint(sketch, "E1958.visualSharp", {"position": v(-20.02, -19.96) * mm});
            skArc(sketch, "E1958.filletArc", {"start": v(-19.02, -19.96) * mm, "mid": v(-19.72, -20.26) * mm, "end": v(-20.02, -20.96) * mm});
            skPoint(sketch, "E1959.visualSharp", {"position": v(-12.3, -19.96) * mm});
            skArc(sketch, "E1959.filletArc", {"start": v(-12.3, -20.96) * mm, "mid": v(-12.6, -20.26) * mm, "end": v(-13.3, -19.96) * mm});
            skPoint(sketch, "E1960.visualSharp", {"position": v(-12.3, -39.35) * mm});
            skArc(sketch, "E1960.filletArc", {"start": v(-13.3, -39.35) * mm, "mid": v(-12.6, -39.06) * mm, "end": v(-12.3, -38.35) * mm});
            skPoint(sketch, "E1961.visualSharp", {"position": v(-20.02, -39.35) * mm});
            skArc(sketch, "E1961.filletArc", {"start": v(-20.02, -38.35) * mm, "mid": v(-19.72, -39.06) * mm, "end": v(-19.02, -39.35) * mm});
            skCircle(sketch, "E1962", {"center": v(-74.9, -14.9) * mm, "radius": 1.5 * mm});
            skCircle(sketch, "E1963", {"center": v(-74.9, -44.9) * mm, "radius": 1.5 * mm});
            skCircle(sketch, "E1964", {"center": v(-4.9, -44.9) * mm, "radius": 1.5 * mm});
            skCircle(sketch, "E1965", {"center": v(-4.9, -14.9) * mm, "radius": 1.5 * mm});
            skLineSegment(sketch, "E1966.bottom", {"start": v(5.1, -54.9) * mm, "end": v(-84.9, -54.9) * mm});
            skLineSegment(sketch, "E1966.top", {"start": v(5.1, -4.9) * mm, "end": v(-84.9, -4.9) * mm});
            skLineSegment(sketch, "E1966.left", {"start": v(10.1, -49.9) * mm, "end": v(10.1, -9.9) * mm});
            skLineSegment(sketch, "E1966.right", {"start": v(-89.9, -49.9) * mm, "end": v(-89.9, -9.9) * mm});
            skPoint(sketch, "E1967.visualSharp", {"position": v(-89.9, -4.9) * mm});
            skArc(sketch, "E1967.filletArc", {"start": v(-84.9, -4.9) * mm, "mid": v(-88.43, -6.36) * mm, "end": v(-89.9, -9.9) * mm});
            skPoint(sketch, "E1968.visualSharp", {"position": v(-89.9, -54.9) * mm});
            skArc(sketch, "E1968.filletArc", {"start": v(-89.9, -49.9) * mm, "mid": v(-88.43, -53.43) * mm, "end": v(-84.9, -54.9) * mm});
            skPoint(sketch, "E1969.visualSharp", {"position": v(10.1, -54.9) * mm});
            skArc(sketch, "E1969.filletArc", {"start": v(5.1, -54.9) * mm, "mid": v(8.64, -53.43) * mm, "end": v(10.1, -49.9) * mm});
            skPoint(sketch, "E1970.visualSharp", {"position": v(10.1, -4.9) * mm});
            skArc(sketch, "E1970.filletArc", {"start": v(10.1, -9.9) * mm, "mid": v(8.64, -6.36) * mm, "end": v(5.1, -4.9) * mm});
            skCircle(sketch, "E1971", {"center": v(-79.9, -9.9) * mm, "radius": 1.5 * mm});
            skCircle(sketch, "E1972", {"center": v(0.1, -9.9) * mm, "radius": 1.5 * mm});
            skCircle(sketch, "E1973", {"center": v(0.1, -49.9) * mm, "radius": 1.5 * mm});
            skCircle(sketch, "E1974", {"center": v(-79.9, -49.9) * mm, "radius": 1.5 * mm});
            skLineSegment(sketch, "E1975.MirrorCS", {"start": v(-79.9, -6.9) * mm, "end": v(0.1, -6.9) * mm});
            skLineSegment(sketch, "E1976", {"start": v(0.1, -9.9) * mm, "end": v(0.1, -6.9) * mm});
            skPoint(sketch, "E1977.orphan", {"position": v(5.1, -6.9) * mm});
            skLineSegment(sketch, "E1978", {"start": v(-79.9, -9.9) * mm, "end": v(-79.9, -6.9) * mm});
            skPoint(sketch, "E1979.orphan", {"position": v(-84.9, -6.9) * mm});
            skLineSegment(sketch, "E1980.trimOffspring", {"start": v(-79.9, -9.9) * mm, "end": v(0.1, -9.9) * mm});
            skLineSegment(sketch, "E1981.MirrorCS", {"start": v(-79.9, -52.9) * mm, "end": v(0.1, -52.9) * mm});
            skLineSegment(sketch, "E1982.MirrorCS", {"start": v(-79.9, -49.9) * mm, "end": v(-79.9, -52.9) * mm});
            skLineSegment(sketch, "E1983.MirrorCS", {"start": v(0.1, -49.9) * mm, "end": v(0.1, -52.9) * mm});
            skSolve(sketch);
        }
        {
            var Q0;
            Q0=makeQuery(id+"F1.imprint","IMPRINT",FACE,{"disambiguationData":[TD([[makeQuery(id+"F1.imprint","IMPRINT",EDGE,{"derivedFrom":sQuery(id+"F1.wireOp",EDGE,"E1940")}),-1.0]])]});
            var Q1;
            Q1=makeQuery(id+"F1.imprint","IMPRINT",FACE,{"disambiguationData":[TD([[makeQuery(id+"F1.imprint","IMPRINT",EDGE,{"derivedFrom":sQuery(id+"F1.wireOp",EDGE,"E1975.MirrorCS")}),-1.0]])]});
            var Q2;
            Q2=makeQuery(id+"F1.imprint","IMPRINT",FACE,{"disambiguationData":[TD([[makeQuery(id+"F1.imprint","IMPRINT",EDGE,{"derivedFrom":sQuery(id+"F1.wireOp",EDGE,"Fhooj3GX-pErk-XnKH-y7UU-3gvhcBIvkp4r.top")}),1.0]])]});
            var Q3;
            {var subQ0=sQuery(id+"F1.wireOp",EDGE,"E1981.MirrorCS");Q3=makeQuery(id+"F1.imprint","IMPRINT",FACE,{"disambiguationData":[TD([[makeQuery(id+"F1.imprint","IMPRINT",EDGE,{"derivedFrom":subQ0}),1.0]])]});}
            extrude(context, id + "F2", {"entities" : qUnion([Q0, Q1, Q2, Q3]), "depth" : 3 * mm, "offsetDistance" : 25 * mm});
        }
        {
            var Q0;
            Q0=makeQuery(id+"F1.imprint","IMPRINT",FACE,{"disambiguationData":[TD([[makeQuery(id+"F1.imprint","IMPRINT",EDGE,{"derivedFrom":sQuery(id+"F1.wireOp",EDGE,"E1966.bottom")}),-1.0]])]});
            var Q1;
            Q1=makeQuery(id+"F1.imprint","IMPRINT",FACE,{"disambiguationData":[TD([[makeQuery(id+"F1.imprint","IMPRINT",EDGE,{"derivedFrom":sQuery(id+"F1.wireOp",EDGE,"E1940")}),1.0]])]});
            var Q2;
            Q2=makeQuery(id+"F1.imprint","IMPRINT",FACE,{"disambiguationData":[TD([[makeQuery(id+"F1.imprint","IMPRINT",EDGE,{"derivedFrom":sQuery(id+"F1.wireOp",EDGE,"E1951.bottom")}),-1.0]])]});
            var Q3;
            Q3=makeQuery(id+"F1.imprint","IMPRINT",FACE,{"disambiguationData":[TD([[makeQuery(id+"F1.imprint","IMPRINT",EDGE,{"derivedFrom":sQuery(id+"F1.wireOp",EDGE,"E1941.bottom")}),-1.0]])]});
            var Q4;
            Q4=makeQuery(id+"F1.imprint","IMPRINT",FACE,{"disambiguationData":[TD([[makeQuery(id+"F1.imprint","IMPRINT",EDGE,{"derivedFrom":sQuery(id+"F1.wireOp",EDGE,"E1956.bottom")}),-1.0]])]});
            var Q5;
            Q5=makeQuery(id+"F1.imprint","IMPRINT",FACE,{"disambiguationData":[TD([[makeQuery(id+"F1.imprint","IMPRINT",EDGE,{"derivedFrom":sQuery(id+"F1.wireOp",EDGE,"E1940")}),-1.0]])]});
            var Q6;
            Q6=makeQuery(id+"F1.imprint","IMPRINT",FACE,{"disambiguationData":[TD([[makeQuery(id+"F1.imprint","IMPRINT",EDGE,{"derivedFrom":sQuery(id+"F1.wireOp",EDGE,"E1946.bottom")}),-1.0]])]});
            var Q7;
            Q7=makeQuery(id+"F1.imprint","IMPRINT",FACE,{"disambiguationData":[TD([[makeQuery(id+"F1.imprint","IMPRINT",EDGE,{"derivedFrom":sQuery(id+"F1.wireOp",EDGE,"E1975.MirrorCS")}),-1.0]])]});
            var Q8;
            Q8=makeQuery(id+"F1.imprint","IMPRINT",FACE,{"disambiguationData":[TD([[makeQuery(id+"F1.imprint","IMPRINT",EDGE,{"derivedFrom":sQuery(id+"F1.wireOp",EDGE,"Fhooj3GX-pErk-XnKH-y7UU-3gvhcBIvkp4r.top")}),1.0]])]});
            var Q9;
            {var subQ0=sQuery(id+"F1.wireOp",EDGE,"E1981.MirrorCS");Q9=makeQuery(id+"F1.imprint","IMPRINT",FACE,{"disambiguationData":[TD([[makeQuery(id+"F1.imprint","IMPRINT",EDGE,{"derivedFrom":subQ0}),1.0]])]});}
            extrude(context, id + "F3", {"entities" : qUnion([Q0, Q1, Q2, Q3, Q4, Q5, Q6, Q7, Q8, Q9]), "depth" : 3 * mm, "offsetDistance" : 25 * mm});
        }
    });
